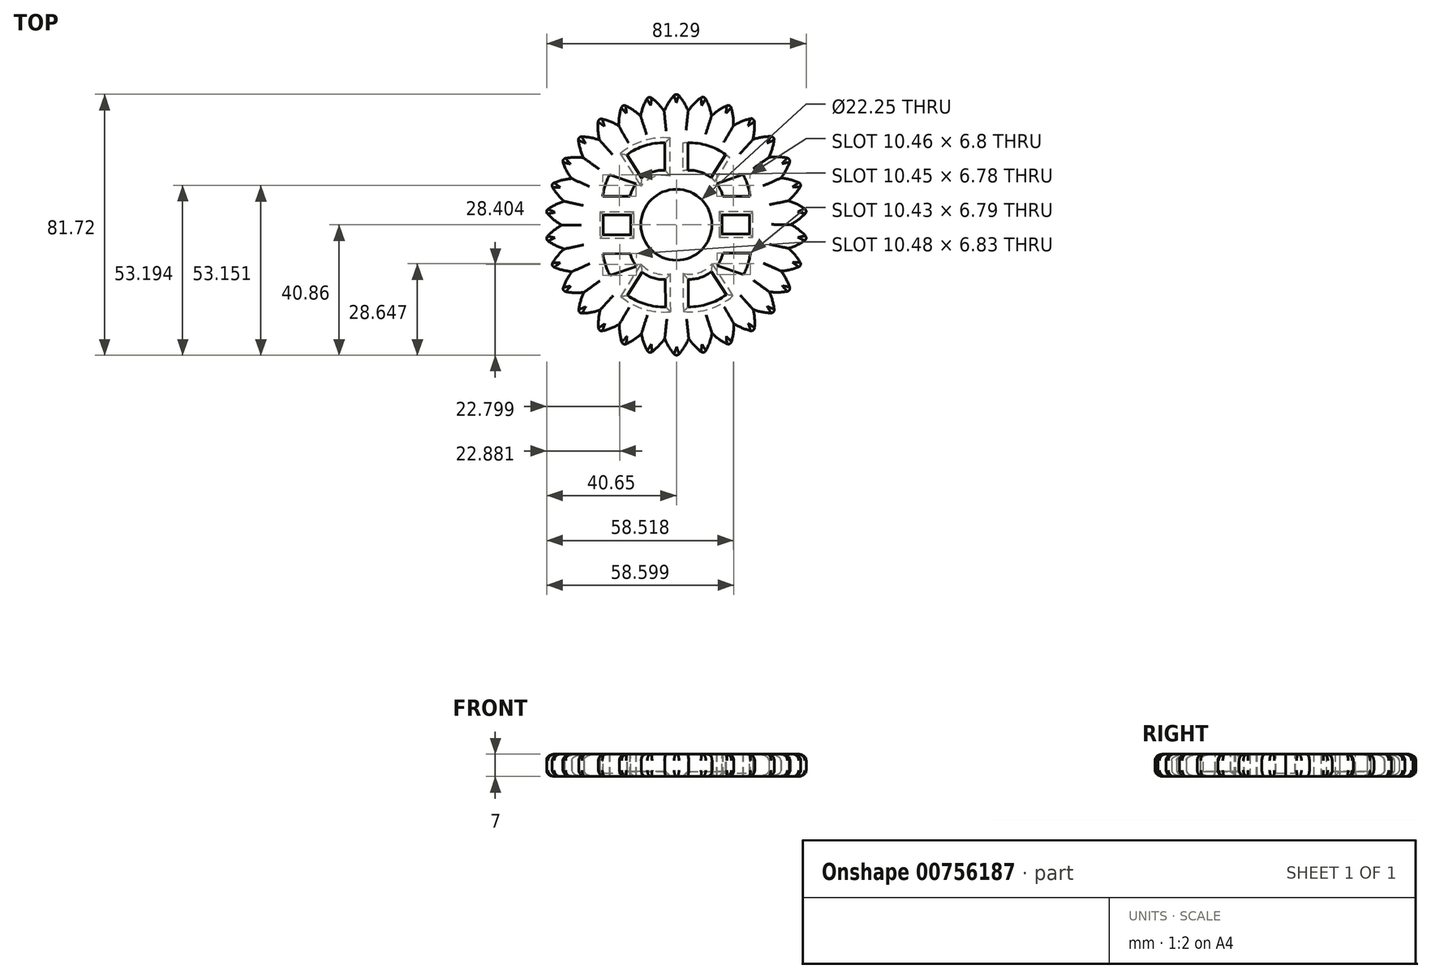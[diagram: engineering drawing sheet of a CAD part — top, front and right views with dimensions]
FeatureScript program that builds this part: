
annotation { "Feature Type Name" : "Feature", "Feature Type Description" : "" }
export const myFeature = defineFeature(function(context is Context, id is Id, definition is map)
    precondition{}
    {
        {
            var Q0;
            Q0=qCreatedBy(makeId("Top.planeOp"),FACE);
            var sketch = newSketch(context, id + "F0", { "sketchPlane" : qUnion([Q0])});
            skCircle(sketch, "E0", {"center": v(0, 0) * mm, "radius": 11.13 * mm});
            skCircle(sketch, "E1", {"center": v(0, 0) * mm, "radius": 28.07 * mm});
            skArc(sketch, "E2", {"start": v(0, 41.34) * mm, "mid": v(-4.06, 35.01) * mm, "end": v(-5.18, 27.59) * mm});
            skArc(sketch, "E3", {"start": v(5.02, 27.62) * mm, "mid": v(3.95, 35) * mm, "end": v(0, 41.34) * mm});
            skArc(sketch, "E4.1.0", {"start": v(8.6, 40.44) * mm, "mid": v(3.31, 35.1) * mm, "end": v(0.67, 28.06) * mm});
            skArc(sketch, "E4.1.1", {"start": v(10.65, 25.97) * mm, "mid": v(11.13, 33.42) * mm, "end": v(8.6, 40.44) * mm});
            skArc(sketch, "E4.2.0", {"start": v(16.8, 37.77) * mm, "mid": v(10.53, 33.64) * mm, "end": v(6.49, 27.3) * mm});
            skArc(sketch, "E4.2.1", {"start": v(15.81, 23.19) * mm, "mid": v(17.84, 30.37) * mm, "end": v(16.8, 37.77) * mm});
            skArc(sketch, "E4.3.0", {"start": v(24.3, 33.45) * mm, "mid": v(17.3, 30.71) * mm, "end": v(12.02, 25.36) * mm});
            skArc(sketch, "E4.3.1", {"start": v(20.29, 19.4) * mm, "mid": v(23.76, 26) * mm, "end": v(24.3, 33.45) * mm});
            skArc(sketch, "E4.4.0", {"start": v(30.71, 27.67) * mm, "mid": v(23.3, 26.45) * mm, "end": v(17.03, 22.31) * mm});
            skArc(sketch, "E4.4.1", {"start": v(23.88, 14.76) * mm, "mid": v(28.65, 20.5) * mm, "end": v(30.71, 27.67) * mm});
            skArc(sketch, "E4.5.0", {"start": v(35.8, 20.68) * mm, "mid": v(28.29, 21.03) * mm, "end": v(21.3, 18.29) * mm});
            skArc(sketch, "E4.5.1", {"start": v(26.42, 9.47) * mm, "mid": v(32.28, 14.1) * mm, "end": v(35.8, 20.68) * mm});
            skArc(sketch, "E4.6.0", {"start": v(39.3, 12.8) * mm, "mid": v(32.04, 14.7) * mm, "end": v(24.63, 13.46) * mm});
            skArc(sketch, "E4.6.1", {"start": v(27.81, 3.77) * mm, "mid": v(34.5, 7.08) * mm, "end": v(39.3, 12.8) * mm});
            skArc(sketch, "E4.7.0", {"start": v(41.1, 4.34) * mm, "mid": v(34.4, 7.71) * mm, "end": v(26.89, 8.05) * mm});
            skArc(sketch, "E4.7.1", {"start": v(27.99, -2.09) * mm, "mid": v(35.22, -0.25) * mm, "end": v(41.1, 4.34) * mm});
            skArc(sketch, "E4.8.0", {"start": v(41.11, -4.3) * mm, "mid": v(35.25, 0.4) * mm, "end": v(27.97, 2.28) * mm});
            skArc(sketch, "E4.8.1", {"start": v(26.94, -7.86) * mm, "mid": v(34.4, -7.56) * mm, "end": v(41.11, -4.3) * mm});
            skArc(sketch, "E4.9.0", {"start": v(39.32, -12.75) * mm, "mid": v(34.56, -6.94) * mm, "end": v(27.84, -3.58) * mm});
            skArc(sketch, "E4.9.1", {"start": v(24.72, -13.29) * mm, "mid": v(32.08, -14.55) * mm, "end": v(39.32, -12.75) * mm});
            skArc(sketch, "E4.10.0", {"start": v(35.82, -20.64) * mm, "mid": v(32.36, -13.97) * mm, "end": v(26.49, -9.29) * mm});
            skArc(sketch, "E4.10.1", {"start": v(21.42, -18.14) * mm, "mid": v(28.36, -20.9) * mm, "end": v(35.82, -20.64) * mm});
            skArc(sketch, "E4.11.0", {"start": v(30.74, -27.64) * mm, "mid": v(28.75, -20.4) * mm, "end": v(23.98, -14.6) * mm});
            skArc(sketch, "E4.11.1", {"start": v(17.18, -22.2) * mm, "mid": v(23.4, -26.33) * mm, "end": v(30.74, -27.64) * mm});
            skArc(sketch, "E4.12.0", {"start": v(24.33, -33.42) * mm, "mid": v(23.89, -25.92) * mm, "end": v(20.42, -19.26) * mm});
            skArc(sketch, "E4.12.1", {"start": v(12.2, -25.28) * mm, "mid": v(17.4, -30.62) * mm, "end": v(24.33, -33.42) * mm});
            skArc(sketch, "E4.13.0", {"start": v(16.85, -37.75) * mm, "mid": v(17.98, -30.32) * mm, "end": v(15.97, -23.08) * mm});
            skArc(sketch, "E4.13.1", {"start": v(6.67, -27.26) * mm, "mid": v(10.67, -33.57) * mm, "end": v(16.85, -37.75) * mm});
            skArc(sketch, "E4.14.0", {"start": v(8.64, -40.43) * mm, "mid": v(11.28, -33.4) * mm, "end": v(10.83, -25.9) * mm});
            skArc(sketch, "E4.14.1", {"start": v(0.86, -28.05) * mm, "mid": v(3.46, -35.05) * mm, "end": v(8.64, -40.43) * mm});
            skArc(sketch, "E4.15.0", {"start": v(0.05, -41.34) * mm, "mid": v(4.1, -35) * mm, "end": v(5.2, -27.58) * mm});
            skArc(sketch, "E4.15.1", {"start": v(-4.99, -27.62) * mm, "mid": v(-3.9, -35) * mm, "end": v(0.05, -41.34) * mm});
            skArc(sketch, "E4.16.0", {"start": v(-8.55, -40.45) * mm, "mid": v(-3.27, -35.1) * mm, "end": v(-0.64, -28.06) * mm});
            skArc(sketch, "E4.16.1", {"start": v(-10.62, -25.98) * mm, "mid": v(-11.1, -33.43) * mm, "end": v(-8.55, -40.45) * mm});
            skArc(sketch, "E4.17.0", {"start": v(-16.77, -37.79) * mm, "mid": v(-10.5, -33.65) * mm, "end": v(-6.45, -27.32) * mm});
            skArc(sketch, "E4.17.1", {"start": v(-15.79, -23.2) * mm, "mid": v(-17.8, -30.4) * mm, "end": v(-16.77, -37.79) * mm});
            skArc(sketch, "E4.18.0", {"start": v(-24.25, -33.48) * mm, "mid": v(-17.26, -30.73) * mm, "end": v(-12, -25.38) * mm});
            skArc(sketch, "E4.18.1", {"start": v(-20.27, -19.42) * mm, "mid": v(-23.73, -26.03) * mm, "end": v(-24.25, -33.48) * mm});
            skArc(sketch, "E4.19.0", {"start": v(-30.68, -27.7) * mm, "mid": v(-23.27, -26.48) * mm, "end": v(-17, -22.33) * mm});
            skArc(sketch, "E4.19.1", {"start": v(-23.86, -14.78) * mm, "mid": v(-28.62, -20.53) * mm, "end": v(-30.68, -27.7) * mm});
            skArc(sketch, "E4.20.0", {"start": v(-35.77, -20.72) * mm, "mid": v(-28.26, -21.06) * mm, "end": v(-21.27, -18.3) * mm});
            skArc(sketch, "E4.20.1", {"start": v(-26.41, -9.5) * mm, "mid": v(-32.26, -14.13) * mm, "end": v(-35.77, -20.72) * mm});
            skArc(sketch, "E4.21.0", {"start": v(-39.3, -12.84) * mm, "mid": v(-32.02, -14.73) * mm, "end": v(-24.61, -13.49) * mm});
            skArc(sketch, "E4.21.1", {"start": v(-27.8, -3.8) * mm, "mid": v(-34.5, -7.12) * mm, "end": v(-39.3, -12.84) * mm});
            skArc(sketch, "E4.22.0", {"start": v(-41.1, -4.39) * mm, "mid": v(-34.39, -7.75) * mm, "end": v(-26.88, -8.08) * mm});
            skArc(sketch, "E4.22.1", {"start": v(-28, 2.06) * mm, "mid": v(-35.22, 0.2) * mm, "end": v(-41.1, -4.39) * mm});
            skArc(sketch, "E4.23.0", {"start": v(-41.12, 4.25) * mm, "mid": v(-35.25, -0.43) * mm, "end": v(-27.97, -2.32) * mm});
            skArc(sketch, "E4.23.1", {"start": v(-26.95, 7.83) * mm, "mid": v(-34.41, 7.52) * mm, "end": v(-41.12, 4.25) * mm});
            skArc(sketch, "E4.24.0", {"start": v(-39.34, 12.7) * mm, "mid": v(-34.57, 6.9) * mm, "end": v(-27.84, 3.55) * mm});
            skArc(sketch, "E4.24.1", {"start": v(-24.74, 13.26) * mm, "mid": v(-32.1, 14.51) * mm, "end": v(-39.34, 12.7) * mm});
            skArc(sketch, "E4.25.0", {"start": v(-35.84, 20.6) * mm, "mid": v(-32.38, 13.93) * mm, "end": v(-26.5, 9.26) * mm});
            skArc(sketch, "E4.25.1", {"start": v(-21.44, 18.11) * mm, "mid": v(-28.38, 20.86) * mm, "end": v(-35.84, 20.6) * mm});
            skArc(sketch, "E4.26.0", {"start": v(-30.77, 27.6) * mm, "mid": v(-28.77, 20.36) * mm, "end": v(-24, 14.56) * mm});
            skArc(sketch, "E4.26.1", {"start": v(-17.2, 22.17) * mm, "mid": v(-23.42, 26.3) * mm, "end": v(-30.77, 27.6) * mm});
            skArc(sketch, "E4.27.0", {"start": v(-24.37, 33.4) * mm, "mid": v(-23.91, 25.9) * mm, "end": v(-20.44, 19.23) * mm});
            skArc(sketch, "E4.27.1", {"start": v(-12.22, 25.27) * mm, "mid": v(-17.44, 30.6) * mm, "end": v(-24.37, 33.4) * mm});
            skArc(sketch, "E4.28.0", {"start": v(-16.9, 37.73) * mm, "mid": v(-18.01, 30.3) * mm, "end": v(-16, 23.06) * mm});
            skArc(sketch, "E4.28.1", {"start": v(-6.7, 27.25) * mm, "mid": v(-10.7, 33.56) * mm, "end": v(-16.9, 37.73) * mm});
            skArc(sketch, "E4.29.0", {"start": v(-8.68, 40.42) * mm, "mid": v(-11.32, 33.38) * mm, "end": v(-10.86, 25.88) * mm});
            skArc(sketch, "E4.29.1", {"start": v(-0.9, 28.05) * mm, "mid": v(-3.5, 35.05) * mm, "end": v(-8.68, 40.42) * mm});
            skLineSegment(sketch, "E4.anchor1", {"start": v(0, 0) * mm, "end": v(-5.18, 27.59) * mm, "construction": true});
            skLineSegment(sketch, "E4.anchor2", {"start": v(0, 0) * mm, "end": v(-10.86, 25.88) * mm, "construction": true});
            skSolve(sketch);
        }
        {
            var Q0;
            Q0 = qSketchRegion(id + "F0", true);
            var Q1;
            Q1=makeQuery(id+"F0.imprint","IMPRINT",FACE,{"disambiguationData":[TD([[makeQuery(id+"F0.imprint","IMPRINT",EDGE,{"derivedFrom":sQuery(id+"F0.wireOp",EDGE,"E0")}),-1.0]])]});
            extrude(context, id + "F1", {"entities" : qUnion([Q0, Q1]), "depth" : 7 * mm, "offsetDistance" : 25 * mm});
        }
        {
            var Q0;
            Q0=makeQuery(id+"F1.opExtrude","CAP_EDGE",EDGE,{"disambiguationData":[OSD([sQuery(id+"F0.wireOp",EDGE,"E4.25.0")])],"isStart":false});
            var Q1;
            Q1=makeQuery(id+"F1.opExtrude","CAP_EDGE",EDGE,{"disambiguationData":[OSD([sQuery(id+"F0.wireOp",EDGE,"E4.25.1")])],"isStart":false});
            var Q2;
            Q2=makeQuery(id+"F1.opExtrude","CAP_EDGE",EDGE,{"disambiguationData":[OSD([sQuery(id+"F0.wireOp",EDGE,"E4.26.0")])],"isStart":false});
            var Q3;
            Q3=makeQuery(id+"F1.opExtrude","CAP_EDGE",EDGE,{"disambiguationData":[OSD([sQuery(id+"F0.wireOp",EDGE,"E4.26.1")])],"isStart":false});
            var Q4;
            Q4=makeQuery(id+"F1.opExtrude","CAP_EDGE",EDGE,{"disambiguationData":[OSD([sQuery(id+"F0.wireOp",EDGE,"E4.27.0")])],"isStart":false});
            var Q5;
            Q5=makeQuery(id+"F1.opExtrude","CAP_EDGE",EDGE,{"disambiguationData":[OSD([sQuery(id+"F0.wireOp",EDGE,"E4.27.1")])],"isStart":false});
            var Q6;
            Q6=makeQuery(id+"F1.opExtrude","CAP_EDGE",EDGE,{"disambiguationData":[OSD([sQuery(id+"F0.wireOp",EDGE,"E4.28.0")])],"isStart":false});
            var Q7;
            Q7=makeQuery(id+"F1.opExtrude","CAP_EDGE",EDGE,{"disambiguationData":[OSD([sQuery(id+"F0.wireOp",EDGE,"E4.28.1")])],"isStart":false});
            var Q8;
            Q8=makeQuery(id+"F1.opExtrude","CAP_EDGE",EDGE,{"disambiguationData":[OSD([sQuery(id+"F0.wireOp",EDGE,"E4.29.0")])],"isStart":false});
            var Q9;
            Q9=makeQuery(id+"F1.opExtrude","CAP_EDGE",EDGE,{"disambiguationData":[OSD([sQuery(id+"F0.wireOp",EDGE,"E4.29.1")])],"isStart":false});
            var Q10;
            Q10=makeQuery(id+"F1.opExtrude","CAP_EDGE",EDGE,{"disambiguationData":[OSD([sQuery(id+"F0.wireOp",EDGE,"E2")])],"isStart":false});
            var Q11;
            Q11=makeQuery(id+"F1.opExtrude","CAP_EDGE",EDGE,{"disambiguationData":[OSD([sQuery(id+"F0.wireOp",EDGE,"E3")])],"isStart":false});
            var Q12;
            Q12=makeQuery(id+"F1.opExtrude","CAP_EDGE",EDGE,{"disambiguationData":[OSD([sQuery(id+"F0.wireOp",EDGE,"E4.1.0")])],"isStart":false});
            var Q13;
            Q13=makeQuery(id+"F1.opExtrude","CAP_EDGE",EDGE,{"disambiguationData":[OSD([sQuery(id+"F0.wireOp",EDGE,"E4.1.1")])],"isStart":false});
            var Q14;
            Q14=makeQuery(id+"F1.opExtrude","CAP_EDGE",EDGE,{"disambiguationData":[OSD([sQuery(id+"F0.wireOp",EDGE,"E4.2.0")])],"isStart":false});
            var Q15;
            Q15=makeQuery(id+"F1.opExtrude","CAP_EDGE",EDGE,{"disambiguationData":[OSD([sQuery(id+"F0.wireOp",EDGE,"E4.2.1")])],"isStart":false});
            var Q16;
            Q16=makeQuery(id+"F1.opExtrude","CAP_EDGE",EDGE,{"disambiguationData":[OSD([sQuery(id+"F0.wireOp",EDGE,"E4.3.0")])],"isStart":false});
            var Q17;
            Q17=makeQuery(id+"F1.opExtrude","CAP_EDGE",EDGE,{"disambiguationData":[OSD([sQuery(id+"F0.wireOp",EDGE,"E4.3.1")])],"isStart":false});
            var Q18;
            Q18=makeQuery(id+"F1.opExtrude","CAP_EDGE",EDGE,{"disambiguationData":[OSD([sQuery(id+"F0.wireOp",EDGE,"E4.4.0")])],"isStart":false});
            var Q19;
            Q19=makeQuery(id+"F1.opExtrude","CAP_EDGE",EDGE,{"disambiguationData":[OSD([sQuery(id+"F0.wireOp",EDGE,"E4.4.1")])],"isStart":false});
            var Q20;
            Q20=makeQuery(id+"F1.opExtrude","CAP_EDGE",EDGE,{"disambiguationData":[OSD([sQuery(id+"F0.wireOp",EDGE,"E4.5.0")])],"isStart":false});
            var Q21;
            Q21=makeQuery(id+"F1.opExtrude","CAP_EDGE",EDGE,{"disambiguationData":[OSD([sQuery(id+"F0.wireOp",EDGE,"E4.5.1")])],"isStart":false});
            var Q22;
            Q22=makeQuery(id+"F1.opExtrude","CAP_EDGE",EDGE,{"disambiguationData":[OSD([sQuery(id+"F0.wireOp",EDGE,"E4.6.0")])],"isStart":false});
            var Q23;
            Q23=makeQuery(id+"F1.opExtrude","CAP_EDGE",EDGE,{"disambiguationData":[OSD([sQuery(id+"F0.wireOp",EDGE,"E4.6.1")])],"isStart":false});
            var Q24;
            Q24=makeQuery(id+"F1.opExtrude","CAP_EDGE",EDGE,{"disambiguationData":[OSD([sQuery(id+"F0.wireOp",EDGE,"E4.7.0")])],"isStart":false});
            var Q25;
            Q25=makeQuery(id+"F1.opExtrude","CAP_EDGE",EDGE,{"disambiguationData":[OSD([sQuery(id+"F0.wireOp",EDGE,"E4.7.1")])],"isStart":false});
            var Q26;
            Q26=makeQuery(id+"F1.opExtrude","CAP_EDGE",EDGE,{"disambiguationData":[OSD([sQuery(id+"F0.wireOp",EDGE,"E4.8.0")])],"isStart":false});
            var Q27;
            Q27=makeQuery(id+"F1.opExtrude","CAP_EDGE",EDGE,{"disambiguationData":[OSD([sQuery(id+"F0.wireOp",EDGE,"E4.8.1")])],"isStart":false});
            var Q28;
            Q28=makeQuery(id+"F1.opExtrude","CAP_EDGE",EDGE,{"disambiguationData":[OSD([sQuery(id+"F0.wireOp",EDGE,"E4.9.0")])],"isStart":false});
            var Q29;
            Q29=makeQuery(id+"F1.opExtrude","CAP_EDGE",EDGE,{"disambiguationData":[OSD([sQuery(id+"F0.wireOp",EDGE,"E4.9.1")])],"isStart":false});
            var Q30;
            Q30=makeQuery(id+"F1.opExtrude","CAP_EDGE",EDGE,{"disambiguationData":[OSD([sQuery(id+"F0.wireOp",EDGE,"E4.10.0")])],"isStart":false});
            var Q31;
            Q31=makeQuery(id+"F1.opExtrude","CAP_EDGE",EDGE,{"disambiguationData":[OSD([sQuery(id+"F0.wireOp",EDGE,"E4.10.1")])],"isStart":false});
            var Q32;
            Q32=makeQuery(id+"F1.opExtrude","CAP_EDGE",EDGE,{"disambiguationData":[OSD([sQuery(id+"F0.wireOp",EDGE,"E4.11.0")])],"isStart":false});
            var Q33;
            Q33=makeQuery(id+"F1.opExtrude","CAP_EDGE",EDGE,{"disambiguationData":[OSD([sQuery(id+"F0.wireOp",EDGE,"E4.11.1")])],"isStart":false});
            var Q34;
            Q34=makeQuery(id+"F1.opExtrude","CAP_EDGE",EDGE,{"disambiguationData":[OSD([sQuery(id+"F0.wireOp",EDGE,"E4.12.0")])],"isStart":false});
            var Q35;
            Q35=makeQuery(id+"F1.opExtrude","CAP_EDGE",EDGE,{"disambiguationData":[OSD([sQuery(id+"F0.wireOp",EDGE,"E4.12.1")])],"isStart":false});
            var Q36;
            Q36=makeQuery(id+"F1.opExtrude","CAP_EDGE",EDGE,{"disambiguationData":[OSD([sQuery(id+"F0.wireOp",EDGE,"E4.13.0")])],"isStart":false});
            var Q37;
            Q37=makeQuery(id+"F1.opExtrude","CAP_EDGE",EDGE,{"disambiguationData":[OSD([sQuery(id+"F0.wireOp",EDGE,"E4.13.1")])],"isStart":false});
            var Q38;
            Q38=makeQuery(id+"F1.opExtrude","CAP_EDGE",EDGE,{"disambiguationData":[OSD([sQuery(id+"F0.wireOp",EDGE,"E4.14.0")])],"isStart":false});
            var Q39;
            Q39=makeQuery(id+"F1.opExtrude","CAP_EDGE",EDGE,{"disambiguationData":[OSD([sQuery(id+"F0.wireOp",EDGE,"E4.14.1")])],"isStart":false});
            var Q40;
            Q40=makeQuery(id+"F1.opExtrude","CAP_EDGE",EDGE,{"disambiguationData":[OSD([sQuery(id+"F0.wireOp",EDGE,"E4.15.0")])],"isStart":false});
            var Q41;
            Q41=makeQuery(id+"F1.opExtrude","CAP_EDGE",EDGE,{"disambiguationData":[OSD([sQuery(id+"F0.wireOp",EDGE,"E4.15.1")])],"isStart":false});
            var Q42;
            Q42=makeQuery(id+"F1.opExtrude","CAP_EDGE",EDGE,{"disambiguationData":[OSD([sQuery(id+"F0.wireOp",EDGE,"E4.16.1")])],"isStart":false});
            var Q43;
            Q43=makeQuery(id+"F1.opExtrude","CAP_EDGE",EDGE,{"disambiguationData":[OSD([sQuery(id+"F0.wireOp",EDGE,"E4.17.0")])],"isStart":false});
            var Q44;
            Q44=makeQuery(id+"F1.opExtrude","CAP_EDGE",EDGE,{"disambiguationData":[OSD([sQuery(id+"F0.wireOp",EDGE,"E4.17.1")])],"isStart":false});
            var Q45;
            Q45=makeQuery(id+"F1.opExtrude","CAP_EDGE",EDGE,{"disambiguationData":[OSD([sQuery(id+"F0.wireOp",EDGE,"E4.18.0")])],"isStart":false});
            var Q46;
            Q46=makeQuery(id+"F1.opExtrude","CAP_EDGE",EDGE,{"disambiguationData":[OSD([sQuery(id+"F0.wireOp",EDGE,"E4.18.1")])],"isStart":false});
            var Q47;
            Q47=makeQuery(id+"F1.opExtrude","CAP_EDGE",EDGE,{"disambiguationData":[OSD([sQuery(id+"F0.wireOp",EDGE,"E4.19.0")])],"isStart":false});
            var Q48;
            Q48=makeQuery(id+"F1.opExtrude","CAP_EDGE",EDGE,{"disambiguationData":[OSD([sQuery(id+"F0.wireOp",EDGE,"E4.19.1")])],"isStart":false});
            var Q49;
            Q49=makeQuery(id+"F1.opExtrude","CAP_EDGE",EDGE,{"disambiguationData":[OSD([sQuery(id+"F0.wireOp",EDGE,"E4.20.0")])],"isStart":false});
            var Q50;
            Q50=makeQuery(id+"F1.opExtrude","CAP_EDGE",EDGE,{"disambiguationData":[OSD([sQuery(id+"F0.wireOp",EDGE,"E4.20.1")])],"isStart":false});
            var Q51;
            Q51=makeQuery(id+"F1.opExtrude","CAP_EDGE",EDGE,{"disambiguationData":[OSD([sQuery(id+"F0.wireOp",EDGE,"E4.21.0")])],"isStart":false});
            var Q52;
            Q52=makeQuery(id+"F1.opExtrude","CAP_EDGE",EDGE,{"disambiguationData":[OSD([sQuery(id+"F0.wireOp",EDGE,"E4.22.0")])],"isStart":false});
            var Q53;
            Q53=makeQuery(id+"F1.opExtrude","CAP_EDGE",EDGE,{"disambiguationData":[OSD([sQuery(id+"F0.wireOp",EDGE,"E4.22.1")])],"isStart":false});
            var Q54;
            Q54=makeQuery(id+"F1.opExtrude","CAP_EDGE",EDGE,{"disambiguationData":[OSD([sQuery(id+"F0.wireOp",EDGE,"E4.23.0")])],"isStart":false});
            var Q55;
            Q55=makeQuery(id+"F1.opExtrude","CAP_EDGE",EDGE,{"disambiguationData":[OSD([sQuery(id+"F0.wireOp",EDGE,"E4.23.1")])],"isStart":false});
            var Q56;
            Q56=makeQuery(id+"F1.opExtrude","CAP_EDGE",EDGE,{"disambiguationData":[OSD([sQuery(id+"F0.wireOp",EDGE,"E4.24.1")])],"isStart":false});
            var Q57;
            Q57=makeQuery(id+"F1.opExtrude","CAP_EDGE",EDGE,{"disambiguationData":[OSD([sQuery(id+"F0.wireOp",EDGE,"E4.24.0")])],"isStart":false});
            var Q58;
            Q58=makeQuery(id+"F1.opExtrude","CAP_EDGE",EDGE,{"disambiguationData":[OSD([sQuery(id+"F0.wireOp",EDGE,"E4.21.1")])],"isStart":false});
            var Q59;
            Q59=makeQuery(id+"F1.opExtrude","CAP_EDGE",EDGE,{"disambiguationData":[OSD([sQuery(id+"F0.wireOp",EDGE,"E4.16.0")])],"isStart":false});
            fillet(context, id + "F2", {"entities" : qUnion([Q0, Q1, Q2, Q3, Q4, Q5, Q6, Q7, Q8, Q9, Q10, Q11, Q12, Q13, Q14, Q15, Q16, Q17, Q18, Q19, Q20, Q21, Q22, Q23, Q24, Q25, Q26, Q27, Q28, Q29, Q30, Q31, Q32, Q33, Q34, Q35, Q36, Q37, Q38, Q39, Q40, Q41, Q42, Q43, Q44, Q45, Q46, Q47, Q48, Q49, Q50, Q51, Q52, Q53, Q54, Q55, Q56, Q57, Q58, Q59]), "radius" : 2 * mm, "tangentPropagation" : true, "allowEdgeOverflow" : false});
        }
        {
            var Q0;
            Q0=makeQuery(id+"F1.opExtrude","CAP_EDGE",EDGE,{"disambiguationData":[OSD([sQuery(id+"F0.wireOp",EDGE,"E4.17.0")])],"isStart":true});
            var Q1;
            Q1=makeQuery(id+"F1.opExtrude","CAP_EDGE",EDGE,{"disambiguationData":[OSD([sQuery(id+"F0.wireOp",EDGE,"E4.16.1")])],"isStart":true});
            var Q2;
            Q2=makeQuery(id+"F1.opExtrude","CAP_EDGE",EDGE,{"disambiguationData":[OSD([sQuery(id+"F0.wireOp",EDGE,"E4.16.0")])],"isStart":true});
            var Q3;
            Q3=makeQuery(id+"F1.opExtrude","CAP_EDGE",EDGE,{"disambiguationData":[OSD([sQuery(id+"F0.wireOp",EDGE,"E4.15.1")])],"isStart":true});
            var Q4;
            Q4=makeQuery(id+"F1.opExtrude","CAP_EDGE",EDGE,{"disambiguationData":[OSD([sQuery(id+"F0.wireOp",EDGE,"E4.15.0")])],"isStart":true});
            var Q5;
            Q5=makeQuery(id+"F1.opExtrude","CAP_EDGE",EDGE,{"disambiguationData":[OSD([sQuery(id+"F0.wireOp",EDGE,"E4.14.1")])],"isStart":true});
            var Q6;
            Q6=makeQuery(id+"F1.opExtrude","CAP_EDGE",EDGE,{"disambiguationData":[OSD([sQuery(id+"F0.wireOp",EDGE,"E4.14.0")])],"isStart":true});
            var Q7;
            Q7=makeQuery(id+"F1.opExtrude","CAP_EDGE",EDGE,{"disambiguationData":[OSD([sQuery(id+"F0.wireOp",EDGE,"E4.13.1")])],"isStart":true});
            var Q8;
            Q8=makeQuery(id+"F1.opExtrude","CAP_EDGE",EDGE,{"disambiguationData":[OSD([sQuery(id+"F0.wireOp",EDGE,"E4.13.0")])],"isStart":true});
            var Q9;
            Q9=makeQuery(id+"F1.opExtrude","CAP_EDGE",EDGE,{"disambiguationData":[OSD([sQuery(id+"F0.wireOp",EDGE,"E4.12.1")])],"isStart":true});
            var Q10;
            Q10=makeQuery(id+"F1.opExtrude","CAP_EDGE",EDGE,{"disambiguationData":[OSD([sQuery(id+"F0.wireOp",EDGE,"E4.12.0")])],"isStart":true});
            var Q11;
            Q11=makeQuery(id+"F1.opExtrude","CAP_EDGE",EDGE,{"disambiguationData":[OSD([sQuery(id+"F0.wireOp",EDGE,"E4.11.1")])],"isStart":true});
            var Q12;
            Q12=makeQuery(id+"F1.opExtrude","CAP_EDGE",EDGE,{"disambiguationData":[OSD([sQuery(id+"F0.wireOp",EDGE,"E4.11.0")])],"isStart":true});
            var Q13;
            Q13=makeQuery(id+"F1.opExtrude","CAP_EDGE",EDGE,{"disambiguationData":[OSD([sQuery(id+"F0.wireOp",EDGE,"E4.10.1")])],"isStart":true});
            var Q14;
            Q14=makeQuery(id+"F1.opExtrude","CAP_EDGE",EDGE,{"disambiguationData":[OSD([sQuery(id+"F0.wireOp",EDGE,"E4.10.0")])],"isStart":true});
            var Q15;
            Q15=makeQuery(id+"F1.opExtrude","CAP_EDGE",EDGE,{"disambiguationData":[OSD([sQuery(id+"F0.wireOp",EDGE,"E4.9.1")])],"isStart":true});
            var Q16;
            Q16=makeQuery(id+"F1.opExtrude","CAP_EDGE",EDGE,{"disambiguationData":[OSD([sQuery(id+"F0.wireOp",EDGE,"E4.9.0")])],"isStart":true});
            var Q17;
            Q17=makeQuery(id+"F1.opExtrude","CAP_EDGE",EDGE,{"disambiguationData":[OSD([sQuery(id+"F0.wireOp",EDGE,"E4.8.1")])],"isStart":true});
            var Q18;
            Q18=makeQuery(id+"F1.opExtrude","CAP_EDGE",EDGE,{"disambiguationData":[OSD([sQuery(id+"F0.wireOp",EDGE,"E4.8.0")])],"isStart":true});
            var Q19;
            Q19=makeQuery(id+"F1.opExtrude","CAP_EDGE",EDGE,{"disambiguationData":[OSD([sQuery(id+"F0.wireOp",EDGE,"E4.7.1")])],"isStart":true});
            var Q20;
            Q20=makeQuery(id+"F1.opExtrude","CAP_EDGE",EDGE,{"disambiguationData":[OSD([sQuery(id+"F0.wireOp",EDGE,"E4.7.0")])],"isStart":true});
            var Q21;
            Q21=makeQuery(id+"F1.opExtrude","CAP_EDGE",EDGE,{"disambiguationData":[OSD([sQuery(id+"F0.wireOp",EDGE,"E4.6.1")])],"isStart":true});
            var Q22;
            Q22=makeQuery(id+"F1.opExtrude","CAP_EDGE",EDGE,{"disambiguationData":[OSD([sQuery(id+"F0.wireOp",EDGE,"E4.6.0")])],"isStart":true});
            var Q23;
            Q23=makeQuery(id+"F1.opExtrude","CAP_EDGE",EDGE,{"disambiguationData":[OSD([sQuery(id+"F0.wireOp",EDGE,"E4.5.1")])],"isStart":true});
            var Q24;
            Q24=makeQuery(id+"F1.opExtrude","CAP_EDGE",EDGE,{"disambiguationData":[OSD([sQuery(id+"F0.wireOp",EDGE,"E4.5.0")])],"isStart":true});
            var Q25;
            Q25=makeQuery(id+"F1.opExtrude","CAP_EDGE",EDGE,{"disambiguationData":[OSD([sQuery(id+"F0.wireOp",EDGE,"E4.4.1")])],"isStart":true});
            var Q26;
            Q26=makeQuery(id+"F1.opExtrude","CAP_EDGE",EDGE,{"disambiguationData":[OSD([sQuery(id+"F0.wireOp",EDGE,"E4.4.0")])],"isStart":true});
            var Q27;
            Q27=makeQuery(id+"F1.opExtrude","CAP_EDGE",EDGE,{"disambiguationData":[OSD([sQuery(id+"F0.wireOp",EDGE,"E4.3.1")])],"isStart":true});
            var Q28;
            Q28=makeQuery(id+"F1.opExtrude","CAP_EDGE",EDGE,{"disambiguationData":[OSD([sQuery(id+"F0.wireOp",EDGE,"E4.3.0")])],"isStart":true});
            var Q29;
            Q29=makeQuery(id+"F1.opExtrude","CAP_EDGE",EDGE,{"disambiguationData":[OSD([sQuery(id+"F0.wireOp",EDGE,"E4.2.1")])],"isStart":true});
            var Q30;
            Q30=makeQuery(id+"F1.opExtrude","CAP_EDGE",EDGE,{"disambiguationData":[OSD([sQuery(id+"F0.wireOp",EDGE,"E4.2.0")])],"isStart":true});
            var Q31;
            Q31=makeQuery(id+"F1.opExtrude","CAP_EDGE",EDGE,{"disambiguationData":[OSD([sQuery(id+"F0.wireOp",EDGE,"E4.1.1")])],"isStart":true});
            var Q32;
            Q32=makeQuery(id+"F1.opExtrude","CAP_EDGE",EDGE,{"disambiguationData":[OSD([sQuery(id+"F0.wireOp",EDGE,"E4.1.0")])],"isStart":true});
            var Q33;
            Q33=makeQuery(id+"F1.opExtrude","CAP_EDGE",EDGE,{"disambiguationData":[OSD([sQuery(id+"F0.wireOp",EDGE,"E3")])],"isStart":true});
            var Q34;
            Q34=makeQuery(id+"F1.opExtrude","CAP_EDGE",EDGE,{"disambiguationData":[OSD([sQuery(id+"F0.wireOp",EDGE,"E2")])],"isStart":true});
            var Q35;
            Q35=makeQuery(id+"F1.opExtrude","CAP_EDGE",EDGE,{"disambiguationData":[OSD([sQuery(id+"F0.wireOp",EDGE,"E4.29.1")])],"isStart":true});
            var Q36;
            Q36=makeQuery(id+"F1.opExtrude","CAP_EDGE",EDGE,{"disambiguationData":[OSD([sQuery(id+"F0.wireOp",EDGE,"E4.29.0")])],"isStart":true});
            var Q37;
            Q37=makeQuery(id+"F1.opExtrude","CAP_EDGE",EDGE,{"disambiguationData":[OSD([sQuery(id+"F0.wireOp",EDGE,"E4.28.1")])],"isStart":true});
            var Q38;
            Q38=makeQuery(id+"F1.opExtrude","CAP_EDGE",EDGE,{"disambiguationData":[OSD([sQuery(id+"F0.wireOp",EDGE,"E4.28.0")])],"isStart":true});
            var Q39;
            Q39=makeQuery(id+"F1.opExtrude","CAP_EDGE",EDGE,{"disambiguationData":[OSD([sQuery(id+"F0.wireOp",EDGE,"E4.27.1")])],"isStart":true});
            var Q40;
            Q40=makeQuery(id+"F1.opExtrude","CAP_EDGE",EDGE,{"disambiguationData":[OSD([sQuery(id+"F0.wireOp",EDGE,"E4.27.0")])],"isStart":true});
            var Q41;
            Q41=makeQuery(id+"F1.opExtrude","CAP_EDGE",EDGE,{"disambiguationData":[OSD([sQuery(id+"F0.wireOp",EDGE,"E4.26.1")])],"isStart":true});
            var Q42;
            Q42=makeQuery(id+"F1.opExtrude","CAP_EDGE",EDGE,{"disambiguationData":[OSD([sQuery(id+"F0.wireOp",EDGE,"E4.26.0")])],"isStart":true});
            var Q43;
            Q43=makeQuery(id+"F1.opExtrude","CAP_EDGE",EDGE,{"disambiguationData":[OSD([sQuery(id+"F0.wireOp",EDGE,"E4.25.1")])],"isStart":true});
            var Q44;
            Q44=makeQuery(id+"F1.opExtrude","CAP_EDGE",EDGE,{"disambiguationData":[OSD([sQuery(id+"F0.wireOp",EDGE,"E4.25.0")])],"isStart":true});
            var Q45;
            Q45=makeQuery(id+"F1.opExtrude","CAP_EDGE",EDGE,{"disambiguationData":[OSD([sQuery(id+"F0.wireOp",EDGE,"E4.24.1")])],"isStart":true});
            var Q46;
            Q46=makeQuery(id+"F1.opExtrude","CAP_EDGE",EDGE,{"disambiguationData":[OSD([sQuery(id+"F0.wireOp",EDGE,"E4.24.0")])],"isStart":true});
            var Q47;
            Q47=makeQuery(id+"F1.opExtrude","CAP_EDGE",EDGE,{"disambiguationData":[OSD([sQuery(id+"F0.wireOp",EDGE,"E4.23.1")])],"isStart":true});
            var Q48;
            Q48=makeQuery(id+"F1.opExtrude","CAP_EDGE",EDGE,{"disambiguationData":[OSD([sQuery(id+"F0.wireOp",EDGE,"E4.23.0")])],"isStart":true});
            var Q49;
            Q49=makeQuery(id+"F1.opExtrude","CAP_EDGE",EDGE,{"disambiguationData":[OSD([sQuery(id+"F0.wireOp",EDGE,"E4.22.1")])],"isStart":true});
            var Q50;
            Q50=makeQuery(id+"F1.opExtrude","CAP_EDGE",EDGE,{"disambiguationData":[OSD([sQuery(id+"F0.wireOp",EDGE,"E4.22.0")])],"isStart":true});
            var Q51;
            Q51=makeQuery(id+"F1.opExtrude","CAP_EDGE",EDGE,{"disambiguationData":[OSD([sQuery(id+"F0.wireOp",EDGE,"E4.21.1")])],"isStart":true});
            var Q52;
            Q52=makeQuery(id+"F1.opExtrude","CAP_EDGE",EDGE,{"disambiguationData":[OSD([sQuery(id+"F0.wireOp",EDGE,"E4.21.0")])],"isStart":true});
            var Q53;
            Q53=makeQuery(id+"F1.opExtrude","CAP_EDGE",EDGE,{"disambiguationData":[OSD([sQuery(id+"F0.wireOp",EDGE,"E4.20.1")])],"isStart":true});
            var Q54;
            Q54=makeQuery(id+"F1.opExtrude","CAP_EDGE",EDGE,{"disambiguationData":[OSD([sQuery(id+"F0.wireOp",EDGE,"E4.20.0")])],"isStart":true});
            var Q55;
            Q55=makeQuery(id+"F1.opExtrude","CAP_EDGE",EDGE,{"disambiguationData":[OSD([sQuery(id+"F0.wireOp",EDGE,"E4.19.1")])],"isStart":true});
            var Q56;
            Q56=makeQuery(id+"F1.opExtrude","CAP_EDGE",EDGE,{"disambiguationData":[OSD([sQuery(id+"F0.wireOp",EDGE,"E4.19.0")])],"isStart":true});
            var Q57;
            Q57=makeQuery(id+"F1.opExtrude","CAP_EDGE",EDGE,{"disambiguationData":[OSD([sQuery(id+"F0.wireOp",EDGE,"E4.18.1")])],"isStart":true});
            var Q58;
            Q58=makeQuery(id+"F1.opExtrude","CAP_EDGE",EDGE,{"disambiguationData":[OSD([sQuery(id+"F0.wireOp",EDGE,"E4.18.0")])],"isStart":true});
            var Q59;
            Q59=makeQuery(id+"F1.opExtrude","CAP_EDGE",EDGE,{"disambiguationData":[OSD([sQuery(id+"F0.wireOp",EDGE,"E4.17.1")])],"isStart":true});
            fillet(context, id + "F3", {"entities" : qUnion([Q0, Q1, Q2, Q3, Q4, Q5, Q6, Q7, Q8, Q9, Q10, Q11, Q12, Q13, Q14, Q15, Q16, Q17, Q18, Q19, Q20, Q21, Q22, Q23, Q24, Q25, Q26, Q27, Q28, Q29, Q30, Q31, Q32, Q33, Q34, Q35, Q36, Q37, Q38, Q39, Q40, Q41, Q42, Q43, Q44, Q45, Q46, Q47, Q48, Q49, Q50, Q51, Q52, Q53, Q54, Q55, Q56, Q57, Q58, Q59]), "radius" : 2 * mm, "tangentPropagation" : true, "allowEdgeOverflow" : false});
        }
        {
            var Q0;
            Q0=makeQuery(id+"F1.opExtrude","CAP_FACE",FACE,{"disambiguationData":[OSD([sQuery(id+"F0.wireOp",EDGE,"E0"),sQuery(id+"F0.wireOp",EDGE,"E2"),sQuery(id+"F0.wireOp",EDGE,"E3"),sQuery(id+"F0.wireOp",EDGE,"E4.1.0"),sQuery(id+"F0.wireOp",EDGE,"E4.1.1"),sQuery(id+"F0.wireOp",EDGE,"E4.2.0"),sQuery(id+"F0.wireOp",EDGE,"E4.2.1"),sQuery(id+"F0.wireOp",EDGE,"E4.3.0"),sQuery(id+"F0.wireOp",EDGE,"E4.3.1"),sQuery(id+"F0.wireOp",EDGE,"E4.4.0"),sQuery(id+"F0.wireOp",EDGE,"E4.4.1"),sQuery(id+"F0.wireOp",EDGE,"E4.5.0"),sQuery(id+"F0.wireOp",EDGE,"E4.5.1"),sQuery(id+"F0.wireOp",EDGE,"E4.6.0"),sQuery(id+"F0.wireOp",EDGE,"E4.6.1"),sQuery(id+"F0.wireOp",EDGE,"E4.7.0"),sQuery(id+"F0.wireOp",EDGE,"E4.7.1"),sQuery(id+"F0.wireOp",EDGE,"E4.8.0"),sQuery(id+"F0.wireOp",EDGE,"E4.8.1"),sQuery(id+"F0.wireOp",EDGE,"E4.9.0"),sQuery(id+"F0.wireOp",EDGE,"E4.9.1"),sQuery(id+"F0.wireOp",EDGE,"E4.10.0"),sQuery(id+"F0.wireOp",EDGE,"E4.10.1"),sQuery(id+"F0.wireOp",EDGE,"E4.11.0"),sQuery(id+"F0.wireOp",EDGE,"E4.11.1"),sQuery(id+"F0.wireOp",EDGE,"E4.12.0"),sQuery(id+"F0.wireOp",EDGE,"E4.12.1"),sQuery(id+"F0.wireOp",EDGE,"E4.13.0"),sQuery(id+"F0.wireOp",EDGE,"E4.13.1"),sQuery(id+"F0.wireOp",EDGE,"E4.14.0"),sQuery(id+"F0.wireOp",EDGE,"E4.14.1"),sQuery(id+"F0.wireOp",EDGE,"E4.15.0"),sQuery(id+"F0.wireOp",EDGE,"E4.15.1"),sQuery(id+"F0.wireOp",EDGE,"E4.16.0"),sQuery(id+"F0.wireOp",EDGE,"E4.16.1"),sQuery(id+"F0.wireOp",EDGE,"E4.17.0"),sQuery(id+"F0.wireOp",EDGE,"E4.17.1"),sQuery(id+"F0.wireOp",EDGE,"E4.18.0"),sQuery(id+"F0.wireOp",EDGE,"E4.18.1"),sQuery(id+"F0.wireOp",EDGE,"E4.19.0"),sQuery(id+"F0.wireOp",EDGE,"E4.19.1"),sQuery(id+"F0.wireOp",EDGE,"E4.20.0"),sQuery(id+"F0.wireOp",EDGE,"E4.20.1"),sQuery(id+"F0.wireOp",EDGE,"E4.21.0"),sQuery(id+"F0.wireOp",EDGE,"E4.21.1"),sQuery(id+"F0.wireOp",EDGE,"E4.22.0"),sQuery(id+"F0.wireOp",EDGE,"E4.22.1"),sQuery(id+"F0.wireOp",EDGE,"E4.23.0"),sQuery(id+"F0.wireOp",EDGE,"E4.23.1"),sQuery(id+"F0.wireOp",EDGE,"E4.24.0"),sQuery(id+"F0.wireOp",EDGE,"E4.24.1"),sQuery(id+"F0.wireOp",EDGE,"E4.25.0"),sQuery(id+"F0.wireOp",EDGE,"E4.25.1"),sQuery(id+"F0.wireOp",EDGE,"E4.26.0"),sQuery(id+"F0.wireOp",EDGE,"E4.26.1"),sQuery(id+"F0.wireOp",EDGE,"E4.27.0"),sQuery(id+"F0.wireOp",EDGE,"E4.27.1"),sQuery(id+"F0.wireOp",EDGE,"E4.28.0"),sQuery(id+"F0.wireOp",EDGE,"E4.28.1"),sQuery(id+"F0.wireOp",EDGE,"E4.29.0"),sQuery(id+"F0.wireOp",EDGE,"E4.29.1")])],"isStart":false});
            var sketch = newSketch(context, id + "F4", { "sketchPlane" : qUnion([Q0])});
            skLineSegment(sketch, "E5", {"start": v(-3.57, 25.67) * mm, "end": v(-3.57, 17.07) * mm});
            skLineSegment(sketch, "E6", {"start": v(-0.02, 38.25) * mm, "end": v(0.07, -38.25) * mm, "construction": true});
            skLineSegment(sketch, "E7.MirrorCS", {"start": v(3.55, 25.68) * mm, "end": v(3.57, 17.08) * mm});
            skLineSegment(sketch, "E8", {"start": v(-14.3, 3.02) * mm, "end": v(-22.9, 3.02) * mm});
            skLineSegment(sketch, "E9.MirrorCS", {"start": v(14.33, 3.05) * mm, "end": v(22.93, 3.08) * mm});
            skLineSegment(sketch, "E10", {"start": v(-29.75, -0.13) * mm, "end": v(29.75, 0.1) * mm, "construction": true});
            skLineSegment(sketch, "E11.MirrorCS", {"start": v(14.36, -2.98) * mm, "end": v(22.96, -2.94) * mm});
            skLineSegment(sketch, "E12.MirrorCS", {"start": v(3.74, -25.69) * mm, "end": v(3.7, -17.09) * mm});
            skLineSegment(sketch, "E13.MirrorCS", {"start": v(-14.27, -3.16) * mm, "end": v(-22.87, -3.22) * mm});
            skLineSegment(sketch, "E14.MirrorCS", {"start": v(-3.38, -25.73) * mm, "end": v(-3.44, -17.13) * mm});
            skArc(sketch, "E15", {"start": v(-3.57, 25.67) * mm, "mid": v(-18.65, 18.96) * mm, "end": v(-22.9, 3.02) * mm});
            skArc(sketch, "E16", {"start": v(-3.57, 17.07) * mm, "mid": v(-12.62, 12.86) * mm, "end": v(-14.3, 3.02) * mm});
            skArc(sketch, "E17.MirrorCS", {"start": v(3.57, 17.08) * mm, "mid": v(12.64, 12.9) * mm, "end": v(14.33, 3.05) * mm});
            skArc(sketch, "E18.MirrorCS", {"start": v(3.55, 25.68) * mm, "mid": v(18.64, 19) * mm, "end": v(22.93, 3.08) * mm});
            skArc(sketch, "E19.MirrorCS", {"start": v(3.74, -25.69) * mm, "mid": v(18.78, -18.9) * mm, "end": v(22.96, -2.94) * mm});
            skArc(sketch, "E20.MirrorCS", {"start": v(3.7, -17.09) * mm, "mid": v(12.73, -12.83) * mm, "end": v(14.36, -2.98) * mm});
            skArc(sketch, "E21.MirrorCS", {"start": v(-3.44, -17.13) * mm, "mid": v(-12.53, -13) * mm, "end": v(-14.27, -3.16) * mm});
            skArc(sketch, "E22.MirrorCS", {"start": v(-3.38, -25.73) * mm, "mid": v(-18.5, -19.14) * mm, "end": v(-22.87, -3.22) * mm});
            skLineSegment(sketch, "E23", {"start": v(-23.08, 8.9) * mm, "end": v(-14.52, 8.9) * mm});
            skLineSegment(sketch, "E24", {"start": v(-20.9, 15.68) * mm, "end": v(-12.62, 12.86) * mm});
            skLineSegment(sketch, "E25", {"start": v(-15.47, 21.93) * mm, "end": v(-10.87, 14.68) * mm});
            skLineSegment(sketch, "E26", {"start": v(-9.35, 24.94) * mm, "end": v(-6.47, 16.82) * mm});
            skLineSegment(sketch, "E27.MirrorCS", {"start": v(23.1, 8.96) * mm, "end": v(14.54, 8.94) * mm});
            skLineSegment(sketch, "E28.MirrorCS", {"start": v(20.9, 15.73) * mm, "end": v(12.64, 12.9) * mm});
            skLineSegment(sketch, "E29.MirrorCS", {"start": v(15.46, 21.96) * mm, "end": v(10.87, 14.7) * mm});
            skLineSegment(sketch, "E30.MirrorCS", {"start": v(9.33, 24.97) * mm, "end": v(6.47, 16.83) * mm});
            skLineSegment(sketch, "E31.MirrorCS", {"start": v(-9.17, -25.05) * mm, "end": v(-6.35, -16.9) * mm});
            skLineSegment(sketch, "E32.MirrorCS", {"start": v(-15.3, -22.07) * mm, "end": v(-10.76, -14.8) * mm});
            skLineSegment(sketch, "E33.MirrorCS", {"start": v(-20.78, -15.87) * mm, "end": v(-12.53, -13) * mm});
            skLineSegment(sketch, "E34.MirrorCS", {"start": v(-23.01, -9.1) * mm, "end": v(-14.45, -9.04) * mm});
            skLineSegment(sketch, "E35.MirrorCS", {"start": v(23.17, -8.82) * mm, "end": v(14.6, -8.86) * mm});
            skLineSegment(sketch, "E36.MirrorCS", {"start": v(21.02, -15.6) * mm, "end": v(12.73, -12.83) * mm});
            skLineSegment(sketch, "E37.MirrorCS", {"start": v(15.63, -21.88) * mm, "end": v(10.98, -14.65) * mm});
            skLineSegment(sketch, "E38.MirrorCS", {"start": v(9.52, -24.93) * mm, "end": v(6.6, -16.82) * mm});
            skLineSegment(sketch, "E39.bottom", {"start": v(-22.9, 3.02) * mm, "end": v(-14.27, 3.02) * mm});
            skLineSegment(sketch, "E39.top", {"start": v(-22.9, -3.16) * mm, "end": v(-14.27, -3.16) * mm});
            skLineSegment(sketch, "E39.left", {"start": v(-22.9, 3.02) * mm, "end": v(-22.9, -3.16) * mm});
            skLineSegment(sketch, "E39.right", {"start": v(-14.27, 3.02) * mm, "end": v(-14.27, -3.16) * mm});
            skLineSegment(sketch, "E40.bottom", {"start": v(14.33, 3.05) * mm, "end": v(22.96, 3.05) * mm});
            skLineSegment(sketch, "E40.top", {"start": v(14.33, -2.94) * mm, "end": v(22.96, -2.94) * mm});
            skLineSegment(sketch, "E40.left", {"start": v(14.33, 3.05) * mm, "end": v(14.33, -2.94) * mm});
            skLineSegment(sketch, "E40.right", {"start": v(22.96, 3.05) * mm, "end": v(22.96, -2.94) * mm});
            skSolve(sketch);
        }
        {
            var Q0;
            {var subQ0=sQuery(id+"F4.wireOp",EDGE,"E25");Q0=makeQuery(id+"F4.imprint","IMPRINT",FACE,{"disambiguationData":[TD([[makeQuery(id+"F4.imprint","IMPRINT",EDGE,{"derivedFrom":subQ0}),1.0]])]});}
            var Q1;
            {var subQ0=sQuery(id+"F4.wireOp",EDGE,"E23");Q1=makeQuery(id+"F4.imprint","IMPRINT",FACE,{"disambiguationData":[TD([[makeQuery(id+"F4.imprint","IMPRINT",EDGE,{"derivedFrom":subQ0}),1.0]])]});}
            var Q2;
            {var subQ0=sQuery(id+"F4.wireOp",EDGE,"E29.MirrorCS");Q2=makeQuery(id+"F4.imprint","IMPRINT",FACE,{"disambiguationData":[TD([[makeQuery(id+"F4.imprint","IMPRINT",EDGE,{"derivedFrom":subQ0}),-1.0]])]});}
            var Q3;
            {var subQ0=sQuery(id+"F4.wireOp",EDGE,"E27.MirrorCS");Q3=makeQuery(id+"F4.imprint","IMPRINT",FACE,{"disambiguationData":[TD([[makeQuery(id+"F4.imprint","IMPRINT",EDGE,{"derivedFrom":subQ0}),-1.0]])]});}
            var Q4;
            {var subQ0=sQuery(id+"F4.wireOp",EDGE,"E37.MirrorCS");Q4=makeQuery(id+"F4.imprint","IMPRINT",FACE,{"disambiguationData":[TD([[makeQuery(id+"F4.imprint","IMPRINT",EDGE,{"derivedFrom":subQ0}),1.0]])]});}
            var Q5;
            {var subQ0=sQuery(id+"F4.wireOp",EDGE,"E31.MirrorCS");Q5=makeQuery(id+"F4.imprint","IMPRINT",FACE,{"disambiguationData":[TD([[makeQuery(id+"F4.imprint","IMPRINT",EDGE,{"derivedFrom":subQ0}),1.0]])]});}
            var Q6;
            {var subQ0=sQuery(id+"F4.wireOp",EDGE,"E33.MirrorCS");Q6=makeQuery(id+"F4.imprint","IMPRINT",FACE,{"disambiguationData":[TD([[makeQuery(id+"F4.imprint","IMPRINT",EDGE,{"derivedFrom":subQ0}),1.0]])]});}
            var Q7;
            {var subQ0=sQuery(id+"F4.wireOp",EDGE,"E35.MirrorCS");Q7=makeQuery(id+"F4.imprint","IMPRINT",FACE,{"disambiguationData":[TD([[makeQuery(id+"F4.imprint","IMPRINT",EDGE,{"derivedFrom":subQ0}),1.0]])]});}
            var Q8;
            Q8=makeQuery(id+"F4.imprint","IMPRINT",FACE,{"disambiguationData":[TD([[makeQuery(id+"F4.imprint","IMPRINT",EDGE,{"derivedFrom":sQuery(id+"F4.wireOp",EDGE,"E39.top")}),1.0]])]});
            var Q9;
            Q9=makeQuery(id+"F4.imprint","IMPRINT",FACE,{"disambiguationData":[TD([[makeQuery(id+"F4.imprint","IMPRINT",EDGE,{"derivedFrom":sQuery(id+"F4.wireOp",EDGE,"E40.bottom")}),-1.0]])]});
            var Q10;
            {var subQ0=sQuery(id+"F4.wireOp",EDGE,"E14.MirrorCS");Q10=makeQuery(id+"F4.imprint","IMPRINT",FACE,{"disambiguationData":[TD([[makeQuery(id+"F4.imprint","IMPRINT",EDGE,{"derivedFrom":subQ0}),1.0]])]});}
            var Q11;
            {var subQ0=sQuery(id+"F4.wireOp",EDGE,"E12.MirrorCS");Q11=makeQuery(id+"F4.imprint","IMPRINT",FACE,{"disambiguationData":[TD([[makeQuery(id+"F4.imprint","IMPRINT",EDGE,{"derivedFrom":subQ0}),-1.0]])]});}
            var Q12;
            {var subQ0=sQuery(id+"F4.wireOp",EDGE,"E7.MirrorCS");Q12=makeQuery(id+"F4.imprint","IMPRINT",FACE,{"disambiguationData":[TD([[makeQuery(id+"F4.imprint","IMPRINT",EDGE,{"derivedFrom":subQ0}),1.0]])]});}
            var Q13;
            {var subQ0=sQuery(id+"F4.wireOp",EDGE,"E5");Q13=makeQuery(id+"F4.imprint","IMPRINT",FACE,{"disambiguationData":[TD([[makeQuery(id+"F4.imprint","IMPRINT",EDGE,{"derivedFrom":subQ0}),-1.0]])]});}
            extrude(context, id + "F5", {"entities" : qUnion([Q0, Q1, Q2, Q3, Q4, Q5, Q6, Q7, Q8, Q9, Q10, Q11, Q12, Q13]), "operationType" : NewBodyOperationType.REMOVE, "oppositeDirection" : true, "depth" : 25 * mm, "offsetDistance" : 25 * mm});
        }
        {
            var Q0;
            Q0=makeQuery(id+"F1.opExtrude","SWEPT_EDGE",EDGE,{"disambiguationData":[OSD([sQuery(id+"F0.wireOp",EDGE,"E4.15.0"),sQuery(id+"F0.wireOp",EDGE,"E4.15.1")])]});
            var Q1;
            Q1=makeQuery(id+"F1.opExtrude","SWEPT_EDGE",EDGE,{"disambiguationData":[OSD([sQuery(id+"F0.wireOp",EDGE,"E4.16.0"),sQuery(id+"F0.wireOp",EDGE,"E4.16.1")])]});
            var Q2;
            Q2=makeQuery(id+"F1.opExtrude","SWEPT_EDGE",EDGE,{"disambiguationData":[OSD([sQuery(id+"F0.wireOp",EDGE,"E4.17.0"),sQuery(id+"F0.wireOp",EDGE,"E4.17.1")])]});
            var Q3;
            Q3=makeQuery(id+"F1.opExtrude","SWEPT_EDGE",EDGE,{"disambiguationData":[OSD([sQuery(id+"F0.wireOp",EDGE,"E4.18.0"),sQuery(id+"F0.wireOp",EDGE,"E4.18.1")])]});
            var Q4;
            Q4=makeQuery(id+"F1.opExtrude","SWEPT_EDGE",EDGE,{"disambiguationData":[OSD([sQuery(id+"F0.wireOp",EDGE,"E4.19.0"),sQuery(id+"F0.wireOp",EDGE,"E4.19.1")])]});
            var Q5;
            Q5=makeQuery(id+"F1.opExtrude","SWEPT_EDGE",EDGE,{"disambiguationData":[OSD([sQuery(id+"F0.wireOp",EDGE,"E4.20.0"),sQuery(id+"F0.wireOp",EDGE,"E4.20.1")])]});
            var Q6;
            Q6=makeQuery(id+"F1.opExtrude","SWEPT_EDGE",EDGE,{"disambiguationData":[OSD([sQuery(id+"F0.wireOp",EDGE,"E4.21.0"),sQuery(id+"F0.wireOp",EDGE,"E4.21.1")])]});
            var Q7;
            Q7=makeQuery(id+"F1.opExtrude","SWEPT_EDGE",EDGE,{"disambiguationData":[OSD([sQuery(id+"F0.wireOp",EDGE,"E4.22.0"),sQuery(id+"F0.wireOp",EDGE,"E4.22.1")])]});
            var Q8;
            Q8=makeQuery(id+"F1.opExtrude","SWEPT_EDGE",EDGE,{"disambiguationData":[OSD([sQuery(id+"F0.wireOp",EDGE,"E4.23.0"),sQuery(id+"F0.wireOp",EDGE,"E4.23.1")])]});
            var Q9;
            Q9=makeQuery(id+"F1.opExtrude","SWEPT_EDGE",EDGE,{"disambiguationData":[OSD([sQuery(id+"F0.wireOp",EDGE,"E4.24.0"),sQuery(id+"F0.wireOp",EDGE,"E4.24.1")])]});
            var Q10;
            Q10=makeQuery(id+"F1.opExtrude","SWEPT_EDGE",EDGE,{"disambiguationData":[OSD([sQuery(id+"F0.wireOp",EDGE,"E4.25.0"),sQuery(id+"F0.wireOp",EDGE,"E4.25.1")])]});
            var Q11;
            Q11=makeQuery(id+"F1.opExtrude","SWEPT_EDGE",EDGE,{"disambiguationData":[OSD([sQuery(id+"F0.wireOp",EDGE,"E4.26.0"),sQuery(id+"F0.wireOp",EDGE,"E4.26.1")])]});
            var Q12;
            Q12=makeQuery(id+"F1.opExtrude","SWEPT_EDGE",EDGE,{"disambiguationData":[OSD([sQuery(id+"F0.wireOp",EDGE,"E4.27.0"),sQuery(id+"F0.wireOp",EDGE,"E4.27.1")])]});
            var Q13;
            Q13=makeQuery(id+"F1.opExtrude","SWEPT_EDGE",EDGE,{"disambiguationData":[OSD([sQuery(id+"F0.wireOp",EDGE,"E4.28.0"),sQuery(id+"F0.wireOp",EDGE,"E4.28.1")])]});
            var Q14;
            Q14=makeQuery(id+"F1.opExtrude","SWEPT_EDGE",EDGE,{"disambiguationData":[OSD([sQuery(id+"F0.wireOp",EDGE,"E4.29.0"),sQuery(id+"F0.wireOp",EDGE,"E4.29.1")])]});
            var Q15;
            Q15=makeQuery(id+"F1.opExtrude","SWEPT_EDGE",EDGE,{"disambiguationData":[OSD([sQuery(id+"F0.wireOp",EDGE,"E2"),sQuery(id+"F0.wireOp",EDGE,"E3")])]});
            var Q16;
            Q16=makeQuery(id+"F1.opExtrude","SWEPT_EDGE",EDGE,{"disambiguationData":[OSD([sQuery(id+"F0.wireOp",EDGE,"E4.1.0"),sQuery(id+"F0.wireOp",EDGE,"E4.1.1")])]});
            var Q17;
            Q17=makeQuery(id+"F1.opExtrude","SWEPT_EDGE",EDGE,{"disambiguationData":[OSD([sQuery(id+"F0.wireOp",EDGE,"E4.2.0"),sQuery(id+"F0.wireOp",EDGE,"E4.2.1")])]});
            var Q18;
            Q18=makeQuery(id+"F1.opExtrude","SWEPT_EDGE",EDGE,{"disambiguationData":[OSD([sQuery(id+"F0.wireOp",EDGE,"E4.3.0"),sQuery(id+"F0.wireOp",EDGE,"E4.3.1")])]});
            var Q19;
            Q19=makeQuery(id+"F1.opExtrude","SWEPT_EDGE",EDGE,{"disambiguationData":[OSD([sQuery(id+"F0.wireOp",EDGE,"E4.4.0"),sQuery(id+"F0.wireOp",EDGE,"E4.4.1")])]});
            var Q20;
            Q20=makeQuery(id+"F1.opExtrude","SWEPT_EDGE",EDGE,{"disambiguationData":[OSD([sQuery(id+"F0.wireOp",EDGE,"E4.5.0"),sQuery(id+"F0.wireOp",EDGE,"E4.5.1")])]});
            var Q21;
            Q21=makeQuery(id+"F1.opExtrude","SWEPT_EDGE",EDGE,{"disambiguationData":[OSD([sQuery(id+"F0.wireOp",EDGE,"E4.6.0"),sQuery(id+"F0.wireOp",EDGE,"E4.6.1")])]});
            var Q22;
            Q22=makeQuery(id+"F1.opExtrude","SWEPT_EDGE",EDGE,{"disambiguationData":[OSD([sQuery(id+"F0.wireOp",EDGE,"E4.7.0"),sQuery(id+"F0.wireOp",EDGE,"E4.7.1")])]});
            var Q23;
            Q23=makeQuery(id+"F1.opExtrude","SWEPT_EDGE",EDGE,{"disambiguationData":[OSD([sQuery(id+"F0.wireOp",EDGE,"E4.8.0"),sQuery(id+"F0.wireOp",EDGE,"E4.8.1")])]});
            var Q24;
            Q24=makeQuery(id+"F1.opExtrude","SWEPT_EDGE",EDGE,{"disambiguationData":[OSD([sQuery(id+"F0.wireOp",EDGE,"E4.9.0"),sQuery(id+"F0.wireOp",EDGE,"E4.9.1")])]});
            var Q25;
            Q25=makeQuery(id+"F1.opExtrude","SWEPT_EDGE",EDGE,{"disambiguationData":[OSD([sQuery(id+"F0.wireOp",EDGE,"E4.10.0"),sQuery(id+"F0.wireOp",EDGE,"E4.10.1")])]});
            var Q26;
            Q26=makeQuery(id+"F1.opExtrude","SWEPT_EDGE",EDGE,{"disambiguationData":[OSD([sQuery(id+"F0.wireOp",EDGE,"E4.11.0"),sQuery(id+"F0.wireOp",EDGE,"E4.11.1")])]});
            var Q27;
            Q27=makeQuery(id+"F1.opExtrude","SWEPT_EDGE",EDGE,{"disambiguationData":[OSD([sQuery(id+"F0.wireOp",EDGE,"E4.13.0"),sQuery(id+"F0.wireOp",EDGE,"E4.13.1")])]});
            var Q28;
            Q28=makeQuery(id+"F1.opExtrude","SWEPT_EDGE",EDGE,{"disambiguationData":[OSD([sQuery(id+"F0.wireOp",EDGE,"E4.14.0"),sQuery(id+"F0.wireOp",EDGE,"E4.14.1")])]});
            fillet(context, id + "F6", {"entities" : qUnion([Q0, Q1, Q2, Q3, Q4, Q5, Q6, Q7, Q8, Q9, Q10, Q11, Q12, Q13, Q14, Q15, Q16, Q17, Q18, Q19, Q20, Q21, Q22, Q23, Q24, Q25, Q26, Q27, Q28]), "radius" : 1 * mm, "tangentPropagation" : true, "allowEdgeOverflow" : false});
        }
        {
            var Q0;
            Q0=makeQuery(id+"F1.opExtrude","SWEPT_EDGE",EDGE,{"disambiguationData":[OSD([sQuery(id+"F0.wireOp",EDGE,"E4.12.0"),sQuery(id+"F0.wireOp",EDGE,"E4.12.1")])]});
            fillet(context, id + "F7", {"entities" : qUnion([Q0]), "radius" : 1 * mm, "tangentPropagation" : true, "allowEdgeOverflow" : false});
        }
        {
            var Q0;
            {var subQ0=sQuery(id+"F4.wireOp",EDGE,"E18.MirrorCS");Q0=makeQuery(id+"F5.boolean.opBoolean","COPY",EDGE,{"derivedFrom":makeQuery(id+"F5.opExtrude","CAP_EDGE",EDGE,{"disambiguationData":[OSD([subQ0]),TDD([makeQuery(id+"F4.imprint","IMPRINT",EDGE,{"disambiguationData":[TD([[makeQuery(id+"F4.imprint","INTERSECT",VERTEX,{"derivedFrom":[sQuery(id+"F4.wireOp",EDGE,"E7.MirrorCS"),subQ0]}),-1.0]])],"derivedFrom":subQ0}),makeQuery(id+"F4.imprint","IMPRINT",EDGE,{"disambiguationData":[TD([[makeQuery(id+"F4.imprint","INTERSECT",VERTEX,{"derivedFrom":[subQ0,sQuery(id+"F4.wireOp",EDGE,"E29.MirrorCS")]}),1.0]])],"derivedFrom":subQ0})])],"isStart":true})});}
            var Q1;
            Q1=makeQuery(id+"F5.boolean.opBoolean","COPY",EDGE,{"derivedFrom":makeQuery(id+"F5.opExtrude","CAP_EDGE",EDGE,{"disambiguationData":[OSD([sQuery(id+"F4.wireOp",EDGE,"E29.MirrorCS")])],"isStart":true})});
            var Q2;
            {var subQ0=sQuery(id+"F4.wireOp",EDGE,"E17.MirrorCS");Q2=makeQuery(id+"F5.boolean.opBoolean","COPY",EDGE,{"derivedFrom":makeQuery(id+"F5.opExtrude","CAP_EDGE",EDGE,{"disambiguationData":[OSD([subQ0]),TDD([makeQuery(id+"F4.imprint","IMPRINT",EDGE,{"disambiguationData":[TD([[makeQuery(id+"F4.imprint","INTERSECT",VERTEX,{"derivedFrom":[sQuery(id+"F4.wireOp",EDGE,"E7.MirrorCS"),subQ0]}),-1.0]])],"derivedFrom":subQ0}),makeQuery(id+"F4.imprint","IMPRINT",EDGE,{"disambiguationData":[TD([[makeQuery(id+"F4.imprint","INTERSECT",VERTEX,{"derivedFrom":[subQ0,sQuery(id+"F4.wireOp",EDGE,"E29.MirrorCS")]}),1.0]])],"derivedFrom":subQ0})])],"isStart":true})});}
            var Q3;
            Q3=makeQuery(id+"F5.boolean.opBoolean","COPY",EDGE,{"derivedFrom":makeQuery(id+"F5.opExtrude","CAP_EDGE",EDGE,{"disambiguationData":[OSD([sQuery(id+"F4.wireOp",EDGE,"E7.MirrorCS")])],"isStart":true})});
            var Q4;
            {var subQ0=sQuery(id+"F4.wireOp",EDGE,"E21.MirrorCS");var subQ1=makeQuery(id+"F4.imprint","INTERSECT",VERTEX,{"derivedFrom":[subQ0,sQuery(id+"F4.wireOp",EDGE,"E31.MirrorCS")]});Q4=makeQuery(id+"F5.boolean.opBoolean","COPY",EDGE,{"derivedFrom":makeQuery(id+"F5.opExtrude","CAP_EDGE",EDGE,{"disambiguationData":[OSD([subQ0]),TDD([makeQuery(id+"F4.imprint","IMPRINT",EDGE,{"disambiguationData":[TD([[makeQuery(id+"F4.imprint","INTERSECT",VERTEX,{"derivedFrom":[sQuery(id+"F4.wireOp",EDGE,"E14.MirrorCS"),subQ0]}),-1.0]])],"derivedFrom":subQ0}),makeQuery(id+"F4.imprint","IMPRINT",EDGE,{"disambiguationData":[TD([[subQ1,-1.0]])],"derivedFrom":subQ0})])],"isStart":true})});}
            var Q5;
            Q5=makeQuery(id+"F5.boolean.opBoolean","COPY",EDGE,{"derivedFrom":makeQuery(id+"F5.opExtrude","CAP_EDGE",EDGE,{"disambiguationData":[OSD([sQuery(id+"F4.wireOp",EDGE,"E32.MirrorCS")])],"isStart":true})});
            var Q6;
            {var subQ0=sQuery(id+"F4.wireOp",EDGE,"E22.MirrorCS");var subQ1=makeQuery(id+"F4.imprint","INTERSECT",VERTEX,{"derivedFrom":[subQ0,sQuery(id+"F4.wireOp",EDGE,"E31.MirrorCS")]});Q6=makeQuery(id+"F5.boolean.opBoolean","COPY",EDGE,{"derivedFrom":makeQuery(id+"F5.opExtrude","CAP_EDGE",EDGE,{"disambiguationData":[OSD([subQ0]),TDD([makeQuery(id+"F4.imprint","IMPRINT",EDGE,{"disambiguationData":[TD([[makeQuery(id+"F4.imprint","INTERSECT",VERTEX,{"derivedFrom":[sQuery(id+"F4.wireOp",EDGE,"E14.MirrorCS"),subQ0]}),-1.0]])],"derivedFrom":subQ0}),makeQuery(id+"F4.imprint","IMPRINT",EDGE,{"disambiguationData":[TD([[subQ1,-1.0]])],"derivedFrom":subQ0})])],"isStart":true})});}
            var Q7;
            Q7=makeQuery(id+"F5.boolean.opBoolean","COPY",EDGE,{"derivedFrom":makeQuery(id+"F5.opExtrude","CAP_EDGE",EDGE,{"disambiguationData":[OSD([sQuery(id+"F4.wireOp",EDGE,"E14.MirrorCS")])],"isStart":true})});
            var Q8;
            {var subQ0=sQuery(id+"F4.wireOp",EDGE,"E20.MirrorCS");Q8=makeQuery(id+"F5.boolean.opBoolean","COPY",EDGE,{"derivedFrom":makeQuery(id+"F5.opExtrude","CAP_EDGE",EDGE,{"disambiguationData":[OSD([subQ0]),TDD([makeQuery(id+"F4.imprint","IMPRINT",EDGE,{"disambiguationData":[TD([[makeQuery(id+"F4.imprint","INTERSECT",VERTEX,{"derivedFrom":[sQuery(id+"F4.wireOp",EDGE,"E12.MirrorCS"),subQ0]}),-1.0]])],"derivedFrom":subQ0}),makeQuery(id+"F4.imprint","IMPRINT",EDGE,{"disambiguationData":[TD([[makeQuery(id+"F4.imprint","INTERSECT",VERTEX,{"derivedFrom":[subQ0,sQuery(id+"F4.wireOp",EDGE,"E37.MirrorCS")]}),1.0]])],"derivedFrom":subQ0})])],"isStart":true})});}
            var Q9;
            {var subQ0=sQuery(id+"F4.wireOp",EDGE,"E19.MirrorCS");Q9=makeQuery(id+"F5.boolean.opBoolean","COPY",EDGE,{"derivedFrom":makeQuery(id+"F5.opExtrude","CAP_EDGE",EDGE,{"disambiguationData":[OSD([subQ0]),TDD([makeQuery(id+"F4.imprint","IMPRINT",EDGE,{"disambiguationData":[TD([[makeQuery(id+"F4.imprint","INTERSECT",VERTEX,{"derivedFrom":[sQuery(id+"F4.wireOp",EDGE,"E12.MirrorCS"),subQ0]}),-1.0]])],"derivedFrom":subQ0}),makeQuery(id+"F4.imprint","IMPRINT",EDGE,{"disambiguationData":[TD([[makeQuery(id+"F4.imprint","INTERSECT",VERTEX,{"derivedFrom":[subQ0,sQuery(id+"F4.wireOp",EDGE,"E37.MirrorCS")]}),1.0]])],"derivedFrom":subQ0})])],"isStart":true})});}
            var Q10;
            Q10=makeQuery(id+"F5.boolean.opBoolean","COPY",EDGE,{"derivedFrom":makeQuery(id+"F5.opExtrude","CAP_EDGE",EDGE,{"disambiguationData":[OSD([sQuery(id+"F4.wireOp",EDGE,"E37.MirrorCS")])],"isStart":true})});
            var Q11;
            {var subQ0=sQuery(id+"F4.wireOp",EDGE,"E16");Q11=makeQuery(id+"F5.boolean.opBoolean","COPY",EDGE,{"derivedFrom":makeQuery(id+"F5.opExtrude","CAP_EDGE",EDGE,{"disambiguationData":[OSD([subQ0]),TDD([makeQuery(id+"F4.imprint","IMPRINT",EDGE,{"disambiguationData":[TD([[makeQuery(id+"F4.imprint","INTERSECT",VERTEX,{"derivedFrom":[sQuery(id+"F4.wireOp",EDGE,"E5"),subQ0]}),-1.0]])],"derivedFrom":subQ0}),makeQuery(id+"F4.imprint","IMPRINT",EDGE,{"disambiguationData":[TD([[makeQuery(id+"F4.imprint","INTERSECT",VERTEX,{"derivedFrom":[subQ0,sQuery(id+"F4.wireOp",EDGE,"E25")]}),1.0]])],"derivedFrom":subQ0})])],"isStart":true})});}
            var Q12;
            {var subQ0=sQuery(id+"F4.wireOp",EDGE,"E15");Q12=makeQuery(id+"F5.boolean.opBoolean","COPY",EDGE,{"derivedFrom":makeQuery(id+"F5.opExtrude","CAP_EDGE",EDGE,{"disambiguationData":[OSD([subQ0]),TDD([makeQuery(id+"F4.imprint","IMPRINT",EDGE,{"disambiguationData":[TD([[makeQuery(id+"F4.imprint","INTERSECT",VERTEX,{"derivedFrom":[sQuery(id+"F4.wireOp",EDGE,"E5"),subQ0]}),-1.0]])],"derivedFrom":subQ0}),makeQuery(id+"F4.imprint","IMPRINT",EDGE,{"disambiguationData":[TD([[makeQuery(id+"F4.imprint","INTERSECT",VERTEX,{"derivedFrom":[subQ0,sQuery(id+"F4.wireOp",EDGE,"E25")]}),1.0]])],"derivedFrom":subQ0})])],"isStart":true})});}
            var Q13;
            Q13=makeQuery(id+"F5.boolean.opBoolean","COPY",EDGE,{"derivedFrom":makeQuery(id+"F5.opExtrude","CAP_EDGE",EDGE,{"disambiguationData":[OSD([sQuery(id+"F4.wireOp",EDGE,"E25")])],"isStart":true})});
            var Q14;
            Q14=makeQuery(id+"F5.boolean.opBoolean","COPY",EDGE,{"derivedFrom":makeQuery(id+"F5.opExtrude","CAP_EDGE",EDGE,{"disambiguationData":[OSD([sQuery(id+"F4.wireOp",EDGE,"E5")])],"isStart":true})});
            var Q15;
            Q15=makeQuery(id+"F5.boolean.opBoolean","COPY",EDGE,{"derivedFrom":makeQuery(id+"F5.opExtrude","CAP_EDGE",EDGE,{"disambiguationData":[OSD([sQuery(id+"F4.wireOp",EDGE,"E12.MirrorCS")])],"isStart":true})});
            var Q16;
            {var subQ0=sQuery(id+"F4.wireOp",EDGE,"E20.MirrorCS");Q16=makeQuery(id+"F5.boolean.opBoolean","INTERSECT",EDGE,{"derivedFrom":[makeQuery(id+"F1.opExtrude","CAP_FACE",FACE,{"disambiguationData":[OSD([sQuery(id+"F0.wireOp",EDGE,"E0"),sQuery(id+"F0.wireOp",EDGE,"E2"),sQuery(id+"F0.wireOp",EDGE,"E3"),sQuery(id+"F0.wireOp",EDGE,"E4.1.0"),sQuery(id+"F0.wireOp",EDGE,"E4.1.1"),sQuery(id+"F0.wireOp",EDGE,"E4.2.0"),sQuery(id+"F0.wireOp",EDGE,"E4.2.1"),sQuery(id+"F0.wireOp",EDGE,"E4.3.0"),sQuery(id+"F0.wireOp",EDGE,"E4.3.1"),sQuery(id+"F0.wireOp",EDGE,"E4.4.0"),sQuery(id+"F0.wireOp",EDGE,"E4.4.1"),sQuery(id+"F0.wireOp",EDGE,"E4.5.0"),sQuery(id+"F0.wireOp",EDGE,"E4.5.1"),sQuery(id+"F0.wireOp",EDGE,"E4.6.0"),sQuery(id+"F0.wireOp",EDGE,"E4.6.1"),sQuery(id+"F0.wireOp",EDGE,"E4.7.0"),sQuery(id+"F0.wireOp",EDGE,"E4.7.1"),sQuery(id+"F0.wireOp",EDGE,"E4.8.0"),sQuery(id+"F0.wireOp",EDGE,"E4.8.1"),sQuery(id+"F0.wireOp",EDGE,"E4.9.0"),sQuery(id+"F0.wireOp",EDGE,"E4.9.1"),sQuery(id+"F0.wireOp",EDGE,"E4.10.0"),sQuery(id+"F0.wireOp",EDGE,"E4.10.1"),sQuery(id+"F0.wireOp",EDGE,"E4.11.0"),sQuery(id+"F0.wireOp",EDGE,"E4.11.1"),sQuery(id+"F0.wireOp",EDGE,"E4.12.0"),sQuery(id+"F0.wireOp",EDGE,"E4.12.1"),sQuery(id+"F0.wireOp",EDGE,"E4.13.0"),sQuery(id+"F0.wireOp",EDGE,"E4.13.1"),sQuery(id+"F0.wireOp",EDGE,"E4.14.0"),sQuery(id+"F0.wireOp",EDGE,"E4.14.1"),sQuery(id+"F0.wireOp",EDGE,"E4.15.0"),sQuery(id+"F0.wireOp",EDGE,"E4.15.1"),sQuery(id+"F0.wireOp",EDGE,"E4.16.0"),sQuery(id+"F0.wireOp",EDGE,"E4.16.1"),sQuery(id+"F0.wireOp",EDGE,"E4.17.0"),sQuery(id+"F0.wireOp",EDGE,"E4.17.1"),sQuery(id+"F0.wireOp",EDGE,"E4.18.0"),sQuery(id+"F0.wireOp",EDGE,"E4.18.1"),sQuery(id+"F0.wireOp",EDGE,"E4.19.0"),sQuery(id+"F0.wireOp",EDGE,"E4.19.1"),sQuery(id+"F0.wireOp",EDGE,"E4.20.0"),sQuery(id+"F0.wireOp",EDGE,"E4.20.1"),sQuery(id+"F0.wireOp",EDGE,"E4.21.0"),sQuery(id+"F0.wireOp",EDGE,"E4.21.1"),sQuery(id+"F0.wireOp",EDGE,"E4.22.0"),sQuery(id+"F0.wireOp",EDGE,"E4.22.1"),sQuery(id+"F0.wireOp",EDGE,"E4.23.0"),sQuery(id+"F0.wireOp",EDGE,"E4.23.1"),sQuery(id+"F0.wireOp",EDGE,"E4.24.0"),sQuery(id+"F0.wireOp",EDGE,"E4.24.1"),sQuery(id+"F0.wireOp",EDGE,"E4.25.0"),sQuery(id+"F0.wireOp",EDGE,"E4.25.1"),sQuery(id+"F0.wireOp",EDGE,"E4.26.0"),sQuery(id+"F0.wireOp",EDGE,"E4.26.1"),sQuery(id+"F0.wireOp",EDGE,"E4.27.0"),sQuery(id+"F0.wireOp",EDGE,"E4.27.1"),sQuery(id+"F0.wireOp",EDGE,"E4.28.0"),sQuery(id+"F0.wireOp",EDGE,"E4.28.1"),sQuery(id+"F0.wireOp",EDGE,"E4.29.0"),sQuery(id+"F0.wireOp",EDGE,"E4.29.1")])],"isStart":true}),makeQuery(id+"F5.opExtrude","SWEPT_FACE",FACE,{"disambiguationData":[OSD([subQ0]),TDD([makeQuery(id+"F4.imprint","IMPRINT",EDGE,{"disambiguationData":[TD([[makeQuery(id+"F4.imprint","INTERSECT",VERTEX,{"derivedFrom":[sQuery(id+"F4.wireOp",EDGE,"E12.MirrorCS"),subQ0]}),-1.0]])],"derivedFrom":subQ0}),makeQuery(id+"F4.imprint","IMPRINT",EDGE,{"disambiguationData":[TD([[makeQuery(id+"F4.imprint","INTERSECT",VERTEX,{"derivedFrom":[subQ0,sQuery(id+"F4.wireOp",EDGE,"E37.MirrorCS")]}),1.0]])],"derivedFrom":subQ0})])]})]});}
            var Q17;
            Q17=makeQuery(id+"F5.boolean.opBoolean","INTERSECT",EDGE,{"derivedFrom":[makeQuery(id+"F1.opExtrude","CAP_FACE",FACE,{"disambiguationData":[OSD([sQuery(id+"F0.wireOp",EDGE,"E0"),sQuery(id+"F0.wireOp",EDGE,"E2"),sQuery(id+"F0.wireOp",EDGE,"E3"),sQuery(id+"F0.wireOp",EDGE,"E4.1.0"),sQuery(id+"F0.wireOp",EDGE,"E4.1.1"),sQuery(id+"F0.wireOp",EDGE,"E4.2.0"),sQuery(id+"F0.wireOp",EDGE,"E4.2.1"),sQuery(id+"F0.wireOp",EDGE,"E4.3.0"),sQuery(id+"F0.wireOp",EDGE,"E4.3.1"),sQuery(id+"F0.wireOp",EDGE,"E4.4.0"),sQuery(id+"F0.wireOp",EDGE,"E4.4.1"),sQuery(id+"F0.wireOp",EDGE,"E4.5.0"),sQuery(id+"F0.wireOp",EDGE,"E4.5.1"),sQuery(id+"F0.wireOp",EDGE,"E4.6.0"),sQuery(id+"F0.wireOp",EDGE,"E4.6.1"),sQuery(id+"F0.wireOp",EDGE,"E4.7.0"),sQuery(id+"F0.wireOp",EDGE,"E4.7.1"),sQuery(id+"F0.wireOp",EDGE,"E4.8.0"),sQuery(id+"F0.wireOp",EDGE,"E4.8.1"),sQuery(id+"F0.wireOp",EDGE,"E4.9.0"),sQuery(id+"F0.wireOp",EDGE,"E4.9.1"),sQuery(id+"F0.wireOp",EDGE,"E4.10.0"),sQuery(id+"F0.wireOp",EDGE,"E4.10.1"),sQuery(id+"F0.wireOp",EDGE,"E4.11.0"),sQuery(id+"F0.wireOp",EDGE,"E4.11.1"),sQuery(id+"F0.wireOp",EDGE,"E4.12.0"),sQuery(id+"F0.wireOp",EDGE,"E4.12.1"),sQuery(id+"F0.wireOp",EDGE,"E4.13.0"),sQuery(id+"F0.wireOp",EDGE,"E4.13.1"),sQuery(id+"F0.wireOp",EDGE,"E4.14.0"),sQuery(id+"F0.wireOp",EDGE,"E4.14.1"),sQuery(id+"F0.wireOp",EDGE,"E4.15.0"),sQuery(id+"F0.wireOp",EDGE,"E4.15.1"),sQuery(id+"F0.wireOp",EDGE,"E4.16.0"),sQuery(id+"F0.wireOp",EDGE,"E4.16.1"),sQuery(id+"F0.wireOp",EDGE,"E4.17.0"),sQuery(id+"F0.wireOp",EDGE,"E4.17.1"),sQuery(id+"F0.wireOp",EDGE,"E4.18.0"),sQuery(id+"F0.wireOp",EDGE,"E4.18.1"),sQuery(id+"F0.wireOp",EDGE,"E4.19.0"),sQuery(id+"F0.wireOp",EDGE,"E4.19.1"),sQuery(id+"F0.wireOp",EDGE,"E4.20.0"),sQuery(id+"F0.wireOp",EDGE,"E4.20.1"),sQuery(id+"F0.wireOp",EDGE,"E4.21.0"),sQuery(id+"F0.wireOp",EDGE,"E4.21.1"),sQuery(id+"F0.wireOp",EDGE,"E4.22.0"),sQuery(id+"F0.wireOp",EDGE,"E4.22.1"),sQuery(id+"F0.wireOp",EDGE,"E4.23.0"),sQuery(id+"F0.wireOp",EDGE,"E4.23.1"),sQuery(id+"F0.wireOp",EDGE,"E4.24.0"),sQuery(id+"F0.wireOp",EDGE,"E4.24.1"),sQuery(id+"F0.wireOp",EDGE,"E4.25.0"),sQuery(id+"F0.wireOp",EDGE,"E4.25.1"),sQuery(id+"F0.wireOp",EDGE,"E4.26.0"),sQuery(id+"F0.wireOp",EDGE,"E4.26.1"),sQuery(id+"F0.wireOp",EDGE,"E4.27.0"),sQuery(id+"F0.wireOp",EDGE,"E4.27.1"),sQuery(id+"F0.wireOp",EDGE,"E4.28.0"),sQuery(id+"F0.wireOp",EDGE,"E4.28.1"),sQuery(id+"F0.wireOp",EDGE,"E4.29.0"),sQuery(id+"F0.wireOp",EDGE,"E4.29.1")])],"isStart":true}),makeQuery(id+"F5.opExtrude","SWEPT_FACE",FACE,{"disambiguationData":[OSD([sQuery(id+"F4.wireOp",EDGE,"E37.MirrorCS")])]})]});
            var Q18;
            {var subQ0=sQuery(id+"F4.wireOp",EDGE,"E19.MirrorCS");Q18=makeQuery(id+"F5.boolean.opBoolean","INTERSECT",EDGE,{"derivedFrom":[makeQuery(id+"F1.opExtrude","CAP_FACE",FACE,{"disambiguationData":[OSD([sQuery(id+"F0.wireOp",EDGE,"E0"),sQuery(id+"F0.wireOp",EDGE,"E2"),sQuery(id+"F0.wireOp",EDGE,"E3"),sQuery(id+"F0.wireOp",EDGE,"E4.1.0"),sQuery(id+"F0.wireOp",EDGE,"E4.1.1"),sQuery(id+"F0.wireOp",EDGE,"E4.2.0"),sQuery(id+"F0.wireOp",EDGE,"E4.2.1"),sQuery(id+"F0.wireOp",EDGE,"E4.3.0"),sQuery(id+"F0.wireOp",EDGE,"E4.3.1"),sQuery(id+"F0.wireOp",EDGE,"E4.4.0"),sQuery(id+"F0.wireOp",EDGE,"E4.4.1"),sQuery(id+"F0.wireOp",EDGE,"E4.5.0"),sQuery(id+"F0.wireOp",EDGE,"E4.5.1"),sQuery(id+"F0.wireOp",EDGE,"E4.6.0"),sQuery(id+"F0.wireOp",EDGE,"E4.6.1"),sQuery(id+"F0.wireOp",EDGE,"E4.7.0"),sQuery(id+"F0.wireOp",EDGE,"E4.7.1"),sQuery(id+"F0.wireOp",EDGE,"E4.8.0"),sQuery(id+"F0.wireOp",EDGE,"E4.8.1"),sQuery(id+"F0.wireOp",EDGE,"E4.9.0"),sQuery(id+"F0.wireOp",EDGE,"E4.9.1"),sQuery(id+"F0.wireOp",EDGE,"E4.10.0"),sQuery(id+"F0.wireOp",EDGE,"E4.10.1"),sQuery(id+"F0.wireOp",EDGE,"E4.11.0"),sQuery(id+"F0.wireOp",EDGE,"E4.11.1"),sQuery(id+"F0.wireOp",EDGE,"E4.12.0"),sQuery(id+"F0.wireOp",EDGE,"E4.12.1"),sQuery(id+"F0.wireOp",EDGE,"E4.13.0"),sQuery(id+"F0.wireOp",EDGE,"E4.13.1"),sQuery(id+"F0.wireOp",EDGE,"E4.14.0"),sQuery(id+"F0.wireOp",EDGE,"E4.14.1"),sQuery(id+"F0.wireOp",EDGE,"E4.15.0"),sQuery(id+"F0.wireOp",EDGE,"E4.15.1"),sQuery(id+"F0.wireOp",EDGE,"E4.16.0"),sQuery(id+"F0.wireOp",EDGE,"E4.16.1"),sQuery(id+"F0.wireOp",EDGE,"E4.17.0"),sQuery(id+"F0.wireOp",EDGE,"E4.17.1"),sQuery(id+"F0.wireOp",EDGE,"E4.18.0"),sQuery(id+"F0.wireOp",EDGE,"E4.18.1"),sQuery(id+"F0.wireOp",EDGE,"E4.19.0"),sQuery(id+"F0.wireOp",EDGE,"E4.19.1"),sQuery(id+"F0.wireOp",EDGE,"E4.20.0"),sQuery(id+"F0.wireOp",EDGE,"E4.20.1"),sQuery(id+"F0.wireOp",EDGE,"E4.21.0"),sQuery(id+"F0.wireOp",EDGE,"E4.21.1"),sQuery(id+"F0.wireOp",EDGE,"E4.22.0"),sQuery(id+"F0.wireOp",EDGE,"E4.22.1"),sQuery(id+"F0.wireOp",EDGE,"E4.23.0"),sQuery(id+"F0.wireOp",EDGE,"E4.23.1"),sQuery(id+"F0.wireOp",EDGE,"E4.24.0"),sQuery(id+"F0.wireOp",EDGE,"E4.24.1"),sQuery(id+"F0.wireOp",EDGE,"E4.25.0"),sQuery(id+"F0.wireOp",EDGE,"E4.25.1"),sQuery(id+"F0.wireOp",EDGE,"E4.26.0"),sQuery(id+"F0.wireOp",EDGE,"E4.26.1"),sQuery(id+"F0.wireOp",EDGE,"E4.27.0"),sQuery(id+"F0.wireOp",EDGE,"E4.27.1"),sQuery(id+"F0.wireOp",EDGE,"E4.28.0"),sQuery(id+"F0.wireOp",EDGE,"E4.28.1"),sQuery(id+"F0.wireOp",EDGE,"E4.29.0"),sQuery(id+"F0.wireOp",EDGE,"E4.29.1")])],"isStart":true}),makeQuery(id+"F5.opExtrude","SWEPT_FACE",FACE,{"disambiguationData":[OSD([subQ0]),TDD([makeQuery(id+"F4.imprint","IMPRINT",EDGE,{"disambiguationData":[TD([[makeQuery(id+"F4.imprint","INTERSECT",VERTEX,{"derivedFrom":[sQuery(id+"F4.wireOp",EDGE,"E12.MirrorCS"),subQ0]}),-1.0]])],"derivedFrom":subQ0}),makeQuery(id+"F4.imprint","IMPRINT",EDGE,{"disambiguationData":[TD([[makeQuery(id+"F4.imprint","INTERSECT",VERTEX,{"derivedFrom":[subQ0,sQuery(id+"F4.wireOp",EDGE,"E37.MirrorCS")]}),1.0]])],"derivedFrom":subQ0})])]})]});}
            var Q19;
            Q19=makeQuery(id+"F5.boolean.opBoolean","INTERSECT",EDGE,{"derivedFrom":[makeQuery(id+"F1.opExtrude","CAP_FACE",FACE,{"disambiguationData":[OSD([sQuery(id+"F0.wireOp",EDGE,"E0"),sQuery(id+"F0.wireOp",EDGE,"E2"),sQuery(id+"F0.wireOp",EDGE,"E3"),sQuery(id+"F0.wireOp",EDGE,"E4.1.0"),sQuery(id+"F0.wireOp",EDGE,"E4.1.1"),sQuery(id+"F0.wireOp",EDGE,"E4.2.0"),sQuery(id+"F0.wireOp",EDGE,"E4.2.1"),sQuery(id+"F0.wireOp",EDGE,"E4.3.0"),sQuery(id+"F0.wireOp",EDGE,"E4.3.1"),sQuery(id+"F0.wireOp",EDGE,"E4.4.0"),sQuery(id+"F0.wireOp",EDGE,"E4.4.1"),sQuery(id+"F0.wireOp",EDGE,"E4.5.0"),sQuery(id+"F0.wireOp",EDGE,"E4.5.1"),sQuery(id+"F0.wireOp",EDGE,"E4.6.0"),sQuery(id+"F0.wireOp",EDGE,"E4.6.1"),sQuery(id+"F0.wireOp",EDGE,"E4.7.0"),sQuery(id+"F0.wireOp",EDGE,"E4.7.1"),sQuery(id+"F0.wireOp",EDGE,"E4.8.0"),sQuery(id+"F0.wireOp",EDGE,"E4.8.1"),sQuery(id+"F0.wireOp",EDGE,"E4.9.0"),sQuery(id+"F0.wireOp",EDGE,"E4.9.1"),sQuery(id+"F0.wireOp",EDGE,"E4.10.0"),sQuery(id+"F0.wireOp",EDGE,"E4.10.1"),sQuery(id+"F0.wireOp",EDGE,"E4.11.0"),sQuery(id+"F0.wireOp",EDGE,"E4.11.1"),sQuery(id+"F0.wireOp",EDGE,"E4.12.0"),sQuery(id+"F0.wireOp",EDGE,"E4.12.1"),sQuery(id+"F0.wireOp",EDGE,"E4.13.0"),sQuery(id+"F0.wireOp",EDGE,"E4.13.1"),sQuery(id+"F0.wireOp",EDGE,"E4.14.0"),sQuery(id+"F0.wireOp",EDGE,"E4.14.1"),sQuery(id+"F0.wireOp",EDGE,"E4.15.0"),sQuery(id+"F0.wireOp",EDGE,"E4.15.1"),sQuery(id+"F0.wireOp",EDGE,"E4.16.0"),sQuery(id+"F0.wireOp",EDGE,"E4.16.1"),sQuery(id+"F0.wireOp",EDGE,"E4.17.0"),sQuery(id+"F0.wireOp",EDGE,"E4.17.1"),sQuery(id+"F0.wireOp",EDGE,"E4.18.0"),sQuery(id+"F0.wireOp",EDGE,"E4.18.1"),sQuery(id+"F0.wireOp",EDGE,"E4.19.0"),sQuery(id+"F0.wireOp",EDGE,"E4.19.1"),sQuery(id+"F0.wireOp",EDGE,"E4.20.0"),sQuery(id+"F0.wireOp",EDGE,"E4.20.1"),sQuery(id+"F0.wireOp",EDGE,"E4.21.0"),sQuery(id+"F0.wireOp",EDGE,"E4.21.1"),sQuery(id+"F0.wireOp",EDGE,"E4.22.0"),sQuery(id+"F0.wireOp",EDGE,"E4.22.1"),sQuery(id+"F0.wireOp",EDGE,"E4.23.0"),sQuery(id+"F0.wireOp",EDGE,"E4.23.1"),sQuery(id+"F0.wireOp",EDGE,"E4.24.0"),sQuery(id+"F0.wireOp",EDGE,"E4.24.1"),sQuery(id+"F0.wireOp",EDGE,"E4.25.0"),sQuery(id+"F0.wireOp",EDGE,"E4.25.1"),sQuery(id+"F0.wireOp",EDGE,"E4.26.0"),sQuery(id+"F0.wireOp",EDGE,"E4.26.1"),sQuery(id+"F0.wireOp",EDGE,"E4.27.0"),sQuery(id+"F0.wireOp",EDGE,"E4.27.1"),sQuery(id+"F0.wireOp",EDGE,"E4.28.0"),sQuery(id+"F0.wireOp",EDGE,"E4.28.1"),sQuery(id+"F0.wireOp",EDGE,"E4.29.0"),sQuery(id+"F0.wireOp",EDGE,"E4.29.1")])],"isStart":true}),makeQuery(id+"F5.opExtrude","SWEPT_FACE",FACE,{"disambiguationData":[OSD([sQuery(id+"F4.wireOp",EDGE,"E12.MirrorCS")])]})]});
            var Q20;
            {var subQ0=sQuery(id+"F4.wireOp",EDGE,"E22.MirrorCS");var subQ1=makeQuery(id+"F4.imprint","INTERSECT",VERTEX,{"derivedFrom":[subQ0,sQuery(id+"F4.wireOp",EDGE,"E31.MirrorCS")]});Q20=makeQuery(id+"F5.boolean.opBoolean","INTERSECT",EDGE,{"derivedFrom":[makeQuery(id+"F1.opExtrude","CAP_FACE",FACE,{"disambiguationData":[OSD([sQuery(id+"F0.wireOp",EDGE,"E0"),sQuery(id+"F0.wireOp",EDGE,"E2"),sQuery(id+"F0.wireOp",EDGE,"E3"),sQuery(id+"F0.wireOp",EDGE,"E4.1.0"),sQuery(id+"F0.wireOp",EDGE,"E4.1.1"),sQuery(id+"F0.wireOp",EDGE,"E4.2.0"),sQuery(id+"F0.wireOp",EDGE,"E4.2.1"),sQuery(id+"F0.wireOp",EDGE,"E4.3.0"),sQuery(id+"F0.wireOp",EDGE,"E4.3.1"),sQuery(id+"F0.wireOp",EDGE,"E4.4.0"),sQuery(id+"F0.wireOp",EDGE,"E4.4.1"),sQuery(id+"F0.wireOp",EDGE,"E4.5.0"),sQuery(id+"F0.wireOp",EDGE,"E4.5.1"),sQuery(id+"F0.wireOp",EDGE,"E4.6.0"),sQuery(id+"F0.wireOp",EDGE,"E4.6.1"),sQuery(id+"F0.wireOp",EDGE,"E4.7.0"),sQuery(id+"F0.wireOp",EDGE,"E4.7.1"),sQuery(id+"F0.wireOp",EDGE,"E4.8.0"),sQuery(id+"F0.wireOp",EDGE,"E4.8.1"),sQuery(id+"F0.wireOp",EDGE,"E4.9.0"),sQuery(id+"F0.wireOp",EDGE,"E4.9.1"),sQuery(id+"F0.wireOp",EDGE,"E4.10.0"),sQuery(id+"F0.wireOp",EDGE,"E4.10.1"),sQuery(id+"F0.wireOp",EDGE,"E4.11.0"),sQuery(id+"F0.wireOp",EDGE,"E4.11.1"),sQuery(id+"F0.wireOp",EDGE,"E4.12.0"),sQuery(id+"F0.wireOp",EDGE,"E4.12.1"),sQuery(id+"F0.wireOp",EDGE,"E4.13.0"),sQuery(id+"F0.wireOp",EDGE,"E4.13.1"),sQuery(id+"F0.wireOp",EDGE,"E4.14.0"),sQuery(id+"F0.wireOp",EDGE,"E4.14.1"),sQuery(id+"F0.wireOp",EDGE,"E4.15.0"),sQuery(id+"F0.wireOp",EDGE,"E4.15.1"),sQuery(id+"F0.wireOp",EDGE,"E4.16.0"),sQuery(id+"F0.wireOp",EDGE,"E4.16.1"),sQuery(id+"F0.wireOp",EDGE,"E4.17.0"),sQuery(id+"F0.wireOp",EDGE,"E4.17.1"),sQuery(id+"F0.wireOp",EDGE,"E4.18.0"),sQuery(id+"F0.wireOp",EDGE,"E4.18.1"),sQuery(id+"F0.wireOp",EDGE,"E4.19.0"),sQuery(id+"F0.wireOp",EDGE,"E4.19.1"),sQuery(id+"F0.wireOp",EDGE,"E4.20.0"),sQuery(id+"F0.wireOp",EDGE,"E4.20.1"),sQuery(id+"F0.wireOp",EDGE,"E4.21.0"),sQuery(id+"F0.wireOp",EDGE,"E4.21.1"),sQuery(id+"F0.wireOp",EDGE,"E4.22.0"),sQuery(id+"F0.wireOp",EDGE,"E4.22.1"),sQuery(id+"F0.wireOp",EDGE,"E4.23.0"),sQuery(id+"F0.wireOp",EDGE,"E4.23.1"),sQuery(id+"F0.wireOp",EDGE,"E4.24.0"),sQuery(id+"F0.wireOp",EDGE,"E4.24.1"),sQuery(id+"F0.wireOp",EDGE,"E4.25.0"),sQuery(id+"F0.wireOp",EDGE,"E4.25.1"),sQuery(id+"F0.wireOp",EDGE,"E4.26.0"),sQuery(id+"F0.wireOp",EDGE,"E4.26.1"),sQuery(id+"F0.wireOp",EDGE,"E4.27.0"),sQuery(id+"F0.wireOp",EDGE,"E4.27.1"),sQuery(id+"F0.wireOp",EDGE,"E4.28.0"),sQuery(id+"F0.wireOp",EDGE,"E4.28.1"),sQuery(id+"F0.wireOp",EDGE,"E4.29.0"),sQuery(id+"F0.wireOp",EDGE,"E4.29.1")])],"isStart":true}),makeQuery(id+"F5.opExtrude","SWEPT_FACE",FACE,{"disambiguationData":[OSD([subQ0]),TDD([makeQuery(id+"F4.imprint","IMPRINT",EDGE,{"disambiguationData":[TD([[makeQuery(id+"F4.imprint","INTERSECT",VERTEX,{"derivedFrom":[sQuery(id+"F4.wireOp",EDGE,"E14.MirrorCS"),subQ0]}),-1.0]])],"derivedFrom":subQ0}),makeQuery(id+"F4.imprint","IMPRINT",EDGE,{"disambiguationData":[TD([[subQ1,-1.0]])],"derivedFrom":subQ0})])]})]});}
            var Q21;
            Q21=makeQuery(id+"F5.boolean.opBoolean","INTERSECT",EDGE,{"derivedFrom":[makeQuery(id+"F1.opExtrude","CAP_FACE",FACE,{"disambiguationData":[OSD([sQuery(id+"F0.wireOp",EDGE,"E0"),sQuery(id+"F0.wireOp",EDGE,"E2"),sQuery(id+"F0.wireOp",EDGE,"E3"),sQuery(id+"F0.wireOp",EDGE,"E4.1.0"),sQuery(id+"F0.wireOp",EDGE,"E4.1.1"),sQuery(id+"F0.wireOp",EDGE,"E4.2.0"),sQuery(id+"F0.wireOp",EDGE,"E4.2.1"),sQuery(id+"F0.wireOp",EDGE,"E4.3.0"),sQuery(id+"F0.wireOp",EDGE,"E4.3.1"),sQuery(id+"F0.wireOp",EDGE,"E4.4.0"),sQuery(id+"F0.wireOp",EDGE,"E4.4.1"),sQuery(id+"F0.wireOp",EDGE,"E4.5.0"),sQuery(id+"F0.wireOp",EDGE,"E4.5.1"),sQuery(id+"F0.wireOp",EDGE,"E4.6.0"),sQuery(id+"F0.wireOp",EDGE,"E4.6.1"),sQuery(id+"F0.wireOp",EDGE,"E4.7.0"),sQuery(id+"F0.wireOp",EDGE,"E4.7.1"),sQuery(id+"F0.wireOp",EDGE,"E4.8.0"),sQuery(id+"F0.wireOp",EDGE,"E4.8.1"),sQuery(id+"F0.wireOp",EDGE,"E4.9.0"),sQuery(id+"F0.wireOp",EDGE,"E4.9.1"),sQuery(id+"F0.wireOp",EDGE,"E4.10.0"),sQuery(id+"F0.wireOp",EDGE,"E4.10.1"),sQuery(id+"F0.wireOp",EDGE,"E4.11.0"),sQuery(id+"F0.wireOp",EDGE,"E4.11.1"),sQuery(id+"F0.wireOp",EDGE,"E4.12.0"),sQuery(id+"F0.wireOp",EDGE,"E4.12.1"),sQuery(id+"F0.wireOp",EDGE,"E4.13.0"),sQuery(id+"F0.wireOp",EDGE,"E4.13.1"),sQuery(id+"F0.wireOp",EDGE,"E4.14.0"),sQuery(id+"F0.wireOp",EDGE,"E4.14.1"),sQuery(id+"F0.wireOp",EDGE,"E4.15.0"),sQuery(id+"F0.wireOp",EDGE,"E4.15.1"),sQuery(id+"F0.wireOp",EDGE,"E4.16.0"),sQuery(id+"F0.wireOp",EDGE,"E4.16.1"),sQuery(id+"F0.wireOp",EDGE,"E4.17.0"),sQuery(id+"F0.wireOp",EDGE,"E4.17.1"),sQuery(id+"F0.wireOp",EDGE,"E4.18.0"),sQuery(id+"F0.wireOp",EDGE,"E4.18.1"),sQuery(id+"F0.wireOp",EDGE,"E4.19.0"),sQuery(id+"F0.wireOp",EDGE,"E4.19.1"),sQuery(id+"F0.wireOp",EDGE,"E4.20.0"),sQuery(id+"F0.wireOp",EDGE,"E4.20.1"),sQuery(id+"F0.wireOp",EDGE,"E4.21.0"),sQuery(id+"F0.wireOp",EDGE,"E4.21.1"),sQuery(id+"F0.wireOp",EDGE,"E4.22.0"),sQuery(id+"F0.wireOp",EDGE,"E4.22.1"),sQuery(id+"F0.wireOp",EDGE,"E4.23.0"),sQuery(id+"F0.wireOp",EDGE,"E4.23.1"),sQuery(id+"F0.wireOp",EDGE,"E4.24.0"),sQuery(id+"F0.wireOp",EDGE,"E4.24.1"),sQuery(id+"F0.wireOp",EDGE,"E4.25.0"),sQuery(id+"F0.wireOp",EDGE,"E4.25.1"),sQuery(id+"F0.wireOp",EDGE,"E4.26.0"),sQuery(id+"F0.wireOp",EDGE,"E4.26.1"),sQuery(id+"F0.wireOp",EDGE,"E4.27.0"),sQuery(id+"F0.wireOp",EDGE,"E4.27.1"),sQuery(id+"F0.wireOp",EDGE,"E4.28.0"),sQuery(id+"F0.wireOp",EDGE,"E4.28.1"),sQuery(id+"F0.wireOp",EDGE,"E4.29.0"),sQuery(id+"F0.wireOp",EDGE,"E4.29.1")])],"isStart":true}),makeQuery(id+"F5.opExtrude","SWEPT_FACE",FACE,{"disambiguationData":[OSD([sQuery(id+"F4.wireOp",EDGE,"E14.MirrorCS")])]})]});
            var Q22;
            {var subQ0=sQuery(id+"F4.wireOp",EDGE,"E21.MirrorCS");var subQ1=makeQuery(id+"F4.imprint","INTERSECT",VERTEX,{"derivedFrom":[subQ0,sQuery(id+"F4.wireOp",EDGE,"E31.MirrorCS")]});Q22=makeQuery(id+"F5.boolean.opBoolean","INTERSECT",EDGE,{"derivedFrom":[makeQuery(id+"F1.opExtrude","CAP_FACE",FACE,{"disambiguationData":[OSD([sQuery(id+"F0.wireOp",EDGE,"E0"),sQuery(id+"F0.wireOp",EDGE,"E2"),sQuery(id+"F0.wireOp",EDGE,"E3"),sQuery(id+"F0.wireOp",EDGE,"E4.1.0"),sQuery(id+"F0.wireOp",EDGE,"E4.1.1"),sQuery(id+"F0.wireOp",EDGE,"E4.2.0"),sQuery(id+"F0.wireOp",EDGE,"E4.2.1"),sQuery(id+"F0.wireOp",EDGE,"E4.3.0"),sQuery(id+"F0.wireOp",EDGE,"E4.3.1"),sQuery(id+"F0.wireOp",EDGE,"E4.4.0"),sQuery(id+"F0.wireOp",EDGE,"E4.4.1"),sQuery(id+"F0.wireOp",EDGE,"E4.5.0"),sQuery(id+"F0.wireOp",EDGE,"E4.5.1"),sQuery(id+"F0.wireOp",EDGE,"E4.6.0"),sQuery(id+"F0.wireOp",EDGE,"E4.6.1"),sQuery(id+"F0.wireOp",EDGE,"E4.7.0"),sQuery(id+"F0.wireOp",EDGE,"E4.7.1"),sQuery(id+"F0.wireOp",EDGE,"E4.8.0"),sQuery(id+"F0.wireOp",EDGE,"E4.8.1"),sQuery(id+"F0.wireOp",EDGE,"E4.9.0"),sQuery(id+"F0.wireOp",EDGE,"E4.9.1"),sQuery(id+"F0.wireOp",EDGE,"E4.10.0"),sQuery(id+"F0.wireOp",EDGE,"E4.10.1"),sQuery(id+"F0.wireOp",EDGE,"E4.11.0"),sQuery(id+"F0.wireOp",EDGE,"E4.11.1"),sQuery(id+"F0.wireOp",EDGE,"E4.12.0"),sQuery(id+"F0.wireOp",EDGE,"E4.12.1"),sQuery(id+"F0.wireOp",EDGE,"E4.13.0"),sQuery(id+"F0.wireOp",EDGE,"E4.13.1"),sQuery(id+"F0.wireOp",EDGE,"E4.14.0"),sQuery(id+"F0.wireOp",EDGE,"E4.14.1"),sQuery(id+"F0.wireOp",EDGE,"E4.15.0"),sQuery(id+"F0.wireOp",EDGE,"E4.15.1"),sQuery(id+"F0.wireOp",EDGE,"E4.16.0"),sQuery(id+"F0.wireOp",EDGE,"E4.16.1"),sQuery(id+"F0.wireOp",EDGE,"E4.17.0"),sQuery(id+"F0.wireOp",EDGE,"E4.17.1"),sQuery(id+"F0.wireOp",EDGE,"E4.18.0"),sQuery(id+"F0.wireOp",EDGE,"E4.18.1"),sQuery(id+"F0.wireOp",EDGE,"E4.19.0"),sQuery(id+"F0.wireOp",EDGE,"E4.19.1"),sQuery(id+"F0.wireOp",EDGE,"E4.20.0"),sQuery(id+"F0.wireOp",EDGE,"E4.20.1"),sQuery(id+"F0.wireOp",EDGE,"E4.21.0"),sQuery(id+"F0.wireOp",EDGE,"E4.21.1"),sQuery(id+"F0.wireOp",EDGE,"E4.22.0"),sQuery(id+"F0.wireOp",EDGE,"E4.22.1"),sQuery(id+"F0.wireOp",EDGE,"E4.23.0"),sQuery(id+"F0.wireOp",EDGE,"E4.23.1"),sQuery(id+"F0.wireOp",EDGE,"E4.24.0"),sQuery(id+"F0.wireOp",EDGE,"E4.24.1"),sQuery(id+"F0.wireOp",EDGE,"E4.25.0"),sQuery(id+"F0.wireOp",EDGE,"E4.25.1"),sQuery(id+"F0.wireOp",EDGE,"E4.26.0"),sQuery(id+"F0.wireOp",EDGE,"E4.26.1"),sQuery(id+"F0.wireOp",EDGE,"E4.27.0"),sQuery(id+"F0.wireOp",EDGE,"E4.27.1"),sQuery(id+"F0.wireOp",EDGE,"E4.28.0"),sQuery(id+"F0.wireOp",EDGE,"E4.28.1"),sQuery(id+"F0.wireOp",EDGE,"E4.29.0"),sQuery(id+"F0.wireOp",EDGE,"E4.29.1")])],"isStart":true}),makeQuery(id+"F5.opExtrude","SWEPT_FACE",FACE,{"disambiguationData":[OSD([subQ0]),TDD([makeQuery(id+"F4.imprint","IMPRINT",EDGE,{"disambiguationData":[TD([[makeQuery(id+"F4.imprint","INTERSECT",VERTEX,{"derivedFrom":[sQuery(id+"F4.wireOp",EDGE,"E14.MirrorCS"),subQ0]}),-1.0]])],"derivedFrom":subQ0}),makeQuery(id+"F4.imprint","IMPRINT",EDGE,{"disambiguationData":[TD([[subQ1,-1.0]])],"derivedFrom":subQ0})])]})]});}
            var Q23;
            Q23=makeQuery(id+"F5.boolean.opBoolean","INTERSECT",EDGE,{"derivedFrom":[makeQuery(id+"F1.opExtrude","CAP_FACE",FACE,{"disambiguationData":[OSD([sQuery(id+"F0.wireOp",EDGE,"E0"),sQuery(id+"F0.wireOp",EDGE,"E2"),sQuery(id+"F0.wireOp",EDGE,"E3"),sQuery(id+"F0.wireOp",EDGE,"E4.1.0"),sQuery(id+"F0.wireOp",EDGE,"E4.1.1"),sQuery(id+"F0.wireOp",EDGE,"E4.2.0"),sQuery(id+"F0.wireOp",EDGE,"E4.2.1"),sQuery(id+"F0.wireOp",EDGE,"E4.3.0"),sQuery(id+"F0.wireOp",EDGE,"E4.3.1"),sQuery(id+"F0.wireOp",EDGE,"E4.4.0"),sQuery(id+"F0.wireOp",EDGE,"E4.4.1"),sQuery(id+"F0.wireOp",EDGE,"E4.5.0"),sQuery(id+"F0.wireOp",EDGE,"E4.5.1"),sQuery(id+"F0.wireOp",EDGE,"E4.6.0"),sQuery(id+"F0.wireOp",EDGE,"E4.6.1"),sQuery(id+"F0.wireOp",EDGE,"E4.7.0"),sQuery(id+"F0.wireOp",EDGE,"E4.7.1"),sQuery(id+"F0.wireOp",EDGE,"E4.8.0"),sQuery(id+"F0.wireOp",EDGE,"E4.8.1"),sQuery(id+"F0.wireOp",EDGE,"E4.9.0"),sQuery(id+"F0.wireOp",EDGE,"E4.9.1"),sQuery(id+"F0.wireOp",EDGE,"E4.10.0"),sQuery(id+"F0.wireOp",EDGE,"E4.10.1"),sQuery(id+"F0.wireOp",EDGE,"E4.11.0"),sQuery(id+"F0.wireOp",EDGE,"E4.11.1"),sQuery(id+"F0.wireOp",EDGE,"E4.12.0"),sQuery(id+"F0.wireOp",EDGE,"E4.12.1"),sQuery(id+"F0.wireOp",EDGE,"E4.13.0"),sQuery(id+"F0.wireOp",EDGE,"E4.13.1"),sQuery(id+"F0.wireOp",EDGE,"E4.14.0"),sQuery(id+"F0.wireOp",EDGE,"E4.14.1"),sQuery(id+"F0.wireOp",EDGE,"E4.15.0"),sQuery(id+"F0.wireOp",EDGE,"E4.15.1"),sQuery(id+"F0.wireOp",EDGE,"E4.16.0"),sQuery(id+"F0.wireOp",EDGE,"E4.16.1"),sQuery(id+"F0.wireOp",EDGE,"E4.17.0"),sQuery(id+"F0.wireOp",EDGE,"E4.17.1"),sQuery(id+"F0.wireOp",EDGE,"E4.18.0"),sQuery(id+"F0.wireOp",EDGE,"E4.18.1"),sQuery(id+"F0.wireOp",EDGE,"E4.19.0"),sQuery(id+"F0.wireOp",EDGE,"E4.19.1"),sQuery(id+"F0.wireOp",EDGE,"E4.20.0"),sQuery(id+"F0.wireOp",EDGE,"E4.20.1"),sQuery(id+"F0.wireOp",EDGE,"E4.21.0"),sQuery(id+"F0.wireOp",EDGE,"E4.21.1"),sQuery(id+"F0.wireOp",EDGE,"E4.22.0"),sQuery(id+"F0.wireOp",EDGE,"E4.22.1"),sQuery(id+"F0.wireOp",EDGE,"E4.23.0"),sQuery(id+"F0.wireOp",EDGE,"E4.23.1"),sQuery(id+"F0.wireOp",EDGE,"E4.24.0"),sQuery(id+"F0.wireOp",EDGE,"E4.24.1"),sQuery(id+"F0.wireOp",EDGE,"E4.25.0"),sQuery(id+"F0.wireOp",EDGE,"E4.25.1"),sQuery(id+"F0.wireOp",EDGE,"E4.26.0"),sQuery(id+"F0.wireOp",EDGE,"E4.26.1"),sQuery(id+"F0.wireOp",EDGE,"E4.27.0"),sQuery(id+"F0.wireOp",EDGE,"E4.27.1"),sQuery(id+"F0.wireOp",EDGE,"E4.28.0"),sQuery(id+"F0.wireOp",EDGE,"E4.28.1"),sQuery(id+"F0.wireOp",EDGE,"E4.29.0"),sQuery(id+"F0.wireOp",EDGE,"E4.29.1")])],"isStart":true}),makeQuery(id+"F5.opExtrude","SWEPT_FACE",FACE,{"disambiguationData":[OSD([sQuery(id+"F4.wireOp",EDGE,"E32.MirrorCS")])]})]});
            var Q24;
            {var subQ0=sQuery(id+"F4.wireOp",EDGE,"E17.MirrorCS");Q24=makeQuery(id+"F5.boolean.opBoolean","INTERSECT",EDGE,{"derivedFrom":[makeQuery(id+"F1.opExtrude","CAP_FACE",FACE,{"disambiguationData":[OSD([sQuery(id+"F0.wireOp",EDGE,"E0"),sQuery(id+"F0.wireOp",EDGE,"E2"),sQuery(id+"F0.wireOp",EDGE,"E3"),sQuery(id+"F0.wireOp",EDGE,"E4.1.0"),sQuery(id+"F0.wireOp",EDGE,"E4.1.1"),sQuery(id+"F0.wireOp",EDGE,"E4.2.0"),sQuery(id+"F0.wireOp",EDGE,"E4.2.1"),sQuery(id+"F0.wireOp",EDGE,"E4.3.0"),sQuery(id+"F0.wireOp",EDGE,"E4.3.1"),sQuery(id+"F0.wireOp",EDGE,"E4.4.0"),sQuery(id+"F0.wireOp",EDGE,"E4.4.1"),sQuery(id+"F0.wireOp",EDGE,"E4.5.0"),sQuery(id+"F0.wireOp",EDGE,"E4.5.1"),sQuery(id+"F0.wireOp",EDGE,"E4.6.0"),sQuery(id+"F0.wireOp",EDGE,"E4.6.1"),sQuery(id+"F0.wireOp",EDGE,"E4.7.0"),sQuery(id+"F0.wireOp",EDGE,"E4.7.1"),sQuery(id+"F0.wireOp",EDGE,"E4.8.0"),sQuery(id+"F0.wireOp",EDGE,"E4.8.1"),sQuery(id+"F0.wireOp",EDGE,"E4.9.0"),sQuery(id+"F0.wireOp",EDGE,"E4.9.1"),sQuery(id+"F0.wireOp",EDGE,"E4.10.0"),sQuery(id+"F0.wireOp",EDGE,"E4.10.1"),sQuery(id+"F0.wireOp",EDGE,"E4.11.0"),sQuery(id+"F0.wireOp",EDGE,"E4.11.1"),sQuery(id+"F0.wireOp",EDGE,"E4.12.0"),sQuery(id+"F0.wireOp",EDGE,"E4.12.1"),sQuery(id+"F0.wireOp",EDGE,"E4.13.0"),sQuery(id+"F0.wireOp",EDGE,"E4.13.1"),sQuery(id+"F0.wireOp",EDGE,"E4.14.0"),sQuery(id+"F0.wireOp",EDGE,"E4.14.1"),sQuery(id+"F0.wireOp",EDGE,"E4.15.0"),sQuery(id+"F0.wireOp",EDGE,"E4.15.1"),sQuery(id+"F0.wireOp",EDGE,"E4.16.0"),sQuery(id+"F0.wireOp",EDGE,"E4.16.1"),sQuery(id+"F0.wireOp",EDGE,"E4.17.0"),sQuery(id+"F0.wireOp",EDGE,"E4.17.1"),sQuery(id+"F0.wireOp",EDGE,"E4.18.0"),sQuery(id+"F0.wireOp",EDGE,"E4.18.1"),sQuery(id+"F0.wireOp",EDGE,"E4.19.0"),sQuery(id+"F0.wireOp",EDGE,"E4.19.1"),sQuery(id+"F0.wireOp",EDGE,"E4.20.0"),sQuery(id+"F0.wireOp",EDGE,"E4.20.1"),sQuery(id+"F0.wireOp",EDGE,"E4.21.0"),sQuery(id+"F0.wireOp",EDGE,"E4.21.1"),sQuery(id+"F0.wireOp",EDGE,"E4.22.0"),sQuery(id+"F0.wireOp",EDGE,"E4.22.1"),sQuery(id+"F0.wireOp",EDGE,"E4.23.0"),sQuery(id+"F0.wireOp",EDGE,"E4.23.1"),sQuery(id+"F0.wireOp",EDGE,"E4.24.0"),sQuery(id+"F0.wireOp",EDGE,"E4.24.1"),sQuery(id+"F0.wireOp",EDGE,"E4.25.0"),sQuery(id+"F0.wireOp",EDGE,"E4.25.1"),sQuery(id+"F0.wireOp",EDGE,"E4.26.0"),sQuery(id+"F0.wireOp",EDGE,"E4.26.1"),sQuery(id+"F0.wireOp",EDGE,"E4.27.0"),sQuery(id+"F0.wireOp",EDGE,"E4.27.1"),sQuery(id+"F0.wireOp",EDGE,"E4.28.0"),sQuery(id+"F0.wireOp",EDGE,"E4.28.1"),sQuery(id+"F0.wireOp",EDGE,"E4.29.0"),sQuery(id+"F0.wireOp",EDGE,"E4.29.1")])],"isStart":true}),makeQuery(id+"F5.opExtrude","SWEPT_FACE",FACE,{"disambiguationData":[OSD([subQ0]),TDD([makeQuery(id+"F4.imprint","IMPRINT",EDGE,{"disambiguationData":[TD([[makeQuery(id+"F4.imprint","INTERSECT",VERTEX,{"derivedFrom":[sQuery(id+"F4.wireOp",EDGE,"E7.MirrorCS"),subQ0]}),-1.0]])],"derivedFrom":subQ0}),makeQuery(id+"F4.imprint","IMPRINT",EDGE,{"disambiguationData":[TD([[makeQuery(id+"F4.imprint","INTERSECT",VERTEX,{"derivedFrom":[subQ0,sQuery(id+"F4.wireOp",EDGE,"E29.MirrorCS")]}),1.0]])],"derivedFrom":subQ0})])]})]});}
            var Q25;
            Q25=makeQuery(id+"F5.boolean.opBoolean","INTERSECT",EDGE,{"derivedFrom":[makeQuery(id+"F1.opExtrude","CAP_FACE",FACE,{"disambiguationData":[OSD([sQuery(id+"F0.wireOp",EDGE,"E0"),sQuery(id+"F0.wireOp",EDGE,"E2"),sQuery(id+"F0.wireOp",EDGE,"E3"),sQuery(id+"F0.wireOp",EDGE,"E4.1.0"),sQuery(id+"F0.wireOp",EDGE,"E4.1.1"),sQuery(id+"F0.wireOp",EDGE,"E4.2.0"),sQuery(id+"F0.wireOp",EDGE,"E4.2.1"),sQuery(id+"F0.wireOp",EDGE,"E4.3.0"),sQuery(id+"F0.wireOp",EDGE,"E4.3.1"),sQuery(id+"F0.wireOp",EDGE,"E4.4.0"),sQuery(id+"F0.wireOp",EDGE,"E4.4.1"),sQuery(id+"F0.wireOp",EDGE,"E4.5.0"),sQuery(id+"F0.wireOp",EDGE,"E4.5.1"),sQuery(id+"F0.wireOp",EDGE,"E4.6.0"),sQuery(id+"F0.wireOp",EDGE,"E4.6.1"),sQuery(id+"F0.wireOp",EDGE,"E4.7.0"),sQuery(id+"F0.wireOp",EDGE,"E4.7.1"),sQuery(id+"F0.wireOp",EDGE,"E4.8.0"),sQuery(id+"F0.wireOp",EDGE,"E4.8.1"),sQuery(id+"F0.wireOp",EDGE,"E4.9.0"),sQuery(id+"F0.wireOp",EDGE,"E4.9.1"),sQuery(id+"F0.wireOp",EDGE,"E4.10.0"),sQuery(id+"F0.wireOp",EDGE,"E4.10.1"),sQuery(id+"F0.wireOp",EDGE,"E4.11.0"),sQuery(id+"F0.wireOp",EDGE,"E4.11.1"),sQuery(id+"F0.wireOp",EDGE,"E4.12.0"),sQuery(id+"F0.wireOp",EDGE,"E4.12.1"),sQuery(id+"F0.wireOp",EDGE,"E4.13.0"),sQuery(id+"F0.wireOp",EDGE,"E4.13.1"),sQuery(id+"F0.wireOp",EDGE,"E4.14.0"),sQuery(id+"F0.wireOp",EDGE,"E4.14.1"),sQuery(id+"F0.wireOp",EDGE,"E4.15.0"),sQuery(id+"F0.wireOp",EDGE,"E4.15.1"),sQuery(id+"F0.wireOp",EDGE,"E4.16.0"),sQuery(id+"F0.wireOp",EDGE,"E4.16.1"),sQuery(id+"F0.wireOp",EDGE,"E4.17.0"),sQuery(id+"F0.wireOp",EDGE,"E4.17.1"),sQuery(id+"F0.wireOp",EDGE,"E4.18.0"),sQuery(id+"F0.wireOp",EDGE,"E4.18.1"),sQuery(id+"F0.wireOp",EDGE,"E4.19.0"),sQuery(id+"F0.wireOp",EDGE,"E4.19.1"),sQuery(id+"F0.wireOp",EDGE,"E4.20.0"),sQuery(id+"F0.wireOp",EDGE,"E4.20.1"),sQuery(id+"F0.wireOp",EDGE,"E4.21.0"),sQuery(id+"F0.wireOp",EDGE,"E4.21.1"),sQuery(id+"F0.wireOp",EDGE,"E4.22.0"),sQuery(id+"F0.wireOp",EDGE,"E4.22.1"),sQuery(id+"F0.wireOp",EDGE,"E4.23.0"),sQuery(id+"F0.wireOp",EDGE,"E4.23.1"),sQuery(id+"F0.wireOp",EDGE,"E4.24.0"),sQuery(id+"F0.wireOp",EDGE,"E4.24.1"),sQuery(id+"F0.wireOp",EDGE,"E4.25.0"),sQuery(id+"F0.wireOp",EDGE,"E4.25.1"),sQuery(id+"F0.wireOp",EDGE,"E4.26.0"),sQuery(id+"F0.wireOp",EDGE,"E4.26.1"),sQuery(id+"F0.wireOp",EDGE,"E4.27.0"),sQuery(id+"F0.wireOp",EDGE,"E4.27.1"),sQuery(id+"F0.wireOp",EDGE,"E4.28.0"),sQuery(id+"F0.wireOp",EDGE,"E4.28.1"),sQuery(id+"F0.wireOp",EDGE,"E4.29.0"),sQuery(id+"F0.wireOp",EDGE,"E4.29.1")])],"isStart":true}),makeQuery(id+"F5.opExtrude","SWEPT_FACE",FACE,{"disambiguationData":[OSD([sQuery(id+"F4.wireOp",EDGE,"E7.MirrorCS")])]})]});
            var Q26;
            Q26=makeQuery(id+"F5.boolean.opBoolean","INTERSECT",EDGE,{"derivedFrom":[makeQuery(id+"F1.opExtrude","CAP_FACE",FACE,{"disambiguationData":[OSD([sQuery(id+"F0.wireOp",EDGE,"E0"),sQuery(id+"F0.wireOp",EDGE,"E2"),sQuery(id+"F0.wireOp",EDGE,"E3"),sQuery(id+"F0.wireOp",EDGE,"E4.1.0"),sQuery(id+"F0.wireOp",EDGE,"E4.1.1"),sQuery(id+"F0.wireOp",EDGE,"E4.2.0"),sQuery(id+"F0.wireOp",EDGE,"E4.2.1"),sQuery(id+"F0.wireOp",EDGE,"E4.3.0"),sQuery(id+"F0.wireOp",EDGE,"E4.3.1"),sQuery(id+"F0.wireOp",EDGE,"E4.4.0"),sQuery(id+"F0.wireOp",EDGE,"E4.4.1"),sQuery(id+"F0.wireOp",EDGE,"E4.5.0"),sQuery(id+"F0.wireOp",EDGE,"E4.5.1"),sQuery(id+"F0.wireOp",EDGE,"E4.6.0"),sQuery(id+"F0.wireOp",EDGE,"E4.6.1"),sQuery(id+"F0.wireOp",EDGE,"E4.7.0"),sQuery(id+"F0.wireOp",EDGE,"E4.7.1"),sQuery(id+"F0.wireOp",EDGE,"E4.8.0"),sQuery(id+"F0.wireOp",EDGE,"E4.8.1"),sQuery(id+"F0.wireOp",EDGE,"E4.9.0"),sQuery(id+"F0.wireOp",EDGE,"E4.9.1"),sQuery(id+"F0.wireOp",EDGE,"E4.10.0"),sQuery(id+"F0.wireOp",EDGE,"E4.10.1"),sQuery(id+"F0.wireOp",EDGE,"E4.11.0"),sQuery(id+"F0.wireOp",EDGE,"E4.11.1"),sQuery(id+"F0.wireOp",EDGE,"E4.12.0"),sQuery(id+"F0.wireOp",EDGE,"E4.12.1"),sQuery(id+"F0.wireOp",EDGE,"E4.13.0"),sQuery(id+"F0.wireOp",EDGE,"E4.13.1"),sQuery(id+"F0.wireOp",EDGE,"E4.14.0"),sQuery(id+"F0.wireOp",EDGE,"E4.14.1"),sQuery(id+"F0.wireOp",EDGE,"E4.15.0"),sQuery(id+"F0.wireOp",EDGE,"E4.15.1"),sQuery(id+"F0.wireOp",EDGE,"E4.16.0"),sQuery(id+"F0.wireOp",EDGE,"E4.16.1"),sQuery(id+"F0.wireOp",EDGE,"E4.17.0"),sQuery(id+"F0.wireOp",EDGE,"E4.17.1"),sQuery(id+"F0.wireOp",EDGE,"E4.18.0"),sQuery(id+"F0.wireOp",EDGE,"E4.18.1"),sQuery(id+"F0.wireOp",EDGE,"E4.19.0"),sQuery(id+"F0.wireOp",EDGE,"E4.19.1"),sQuery(id+"F0.wireOp",EDGE,"E4.20.0"),sQuery(id+"F0.wireOp",EDGE,"E4.20.1"),sQuery(id+"F0.wireOp",EDGE,"E4.21.0"),sQuery(id+"F0.wireOp",EDGE,"E4.21.1"),sQuery(id+"F0.wireOp",EDGE,"E4.22.0"),sQuery(id+"F0.wireOp",EDGE,"E4.22.1"),sQuery(id+"F0.wireOp",EDGE,"E4.23.0"),sQuery(id+"F0.wireOp",EDGE,"E4.23.1"),sQuery(id+"F0.wireOp",EDGE,"E4.24.0"),sQuery(id+"F0.wireOp",EDGE,"E4.24.1"),sQuery(id+"F0.wireOp",EDGE,"E4.25.0"),sQuery(id+"F0.wireOp",EDGE,"E4.25.1"),sQuery(id+"F0.wireOp",EDGE,"E4.26.0"),sQuery(id+"F0.wireOp",EDGE,"E4.26.1"),sQuery(id+"F0.wireOp",EDGE,"E4.27.0"),sQuery(id+"F0.wireOp",EDGE,"E4.27.1"),sQuery(id+"F0.wireOp",EDGE,"E4.28.0"),sQuery(id+"F0.wireOp",EDGE,"E4.28.1"),sQuery(id+"F0.wireOp",EDGE,"E4.29.0"),sQuery(id+"F0.wireOp",EDGE,"E4.29.1")])],"isStart":true}),makeQuery(id+"F5.opExtrude","SWEPT_FACE",FACE,{"disambiguationData":[OSD([sQuery(id+"F4.wireOp",EDGE,"E29.MirrorCS")])]})]});
            var Q27;
            {var subQ0=sQuery(id+"F4.wireOp",EDGE,"E18.MirrorCS");Q27=makeQuery(id+"F5.boolean.opBoolean","INTERSECT",EDGE,{"derivedFrom":[makeQuery(id+"F1.opExtrude","CAP_FACE",FACE,{"disambiguationData":[OSD([sQuery(id+"F0.wireOp",EDGE,"E0"),sQuery(id+"F0.wireOp",EDGE,"E2"),sQuery(id+"F0.wireOp",EDGE,"E3"),sQuery(id+"F0.wireOp",EDGE,"E4.1.0"),sQuery(id+"F0.wireOp",EDGE,"E4.1.1"),sQuery(id+"F0.wireOp",EDGE,"E4.2.0"),sQuery(id+"F0.wireOp",EDGE,"E4.2.1"),sQuery(id+"F0.wireOp",EDGE,"E4.3.0"),sQuery(id+"F0.wireOp",EDGE,"E4.3.1"),sQuery(id+"F0.wireOp",EDGE,"E4.4.0"),sQuery(id+"F0.wireOp",EDGE,"E4.4.1"),sQuery(id+"F0.wireOp",EDGE,"E4.5.0"),sQuery(id+"F0.wireOp",EDGE,"E4.5.1"),sQuery(id+"F0.wireOp",EDGE,"E4.6.0"),sQuery(id+"F0.wireOp",EDGE,"E4.6.1"),sQuery(id+"F0.wireOp",EDGE,"E4.7.0"),sQuery(id+"F0.wireOp",EDGE,"E4.7.1"),sQuery(id+"F0.wireOp",EDGE,"E4.8.0"),sQuery(id+"F0.wireOp",EDGE,"E4.8.1"),sQuery(id+"F0.wireOp",EDGE,"E4.9.0"),sQuery(id+"F0.wireOp",EDGE,"E4.9.1"),sQuery(id+"F0.wireOp",EDGE,"E4.10.0"),sQuery(id+"F0.wireOp",EDGE,"E4.10.1"),sQuery(id+"F0.wireOp",EDGE,"E4.11.0"),sQuery(id+"F0.wireOp",EDGE,"E4.11.1"),sQuery(id+"F0.wireOp",EDGE,"E4.12.0"),sQuery(id+"F0.wireOp",EDGE,"E4.12.1"),sQuery(id+"F0.wireOp",EDGE,"E4.13.0"),sQuery(id+"F0.wireOp",EDGE,"E4.13.1"),sQuery(id+"F0.wireOp",EDGE,"E4.14.0"),sQuery(id+"F0.wireOp",EDGE,"E4.14.1"),sQuery(id+"F0.wireOp",EDGE,"E4.15.0"),sQuery(id+"F0.wireOp",EDGE,"E4.15.1"),sQuery(id+"F0.wireOp",EDGE,"E4.16.0"),sQuery(id+"F0.wireOp",EDGE,"E4.16.1"),sQuery(id+"F0.wireOp",EDGE,"E4.17.0"),sQuery(id+"F0.wireOp",EDGE,"E4.17.1"),sQuery(id+"F0.wireOp",EDGE,"E4.18.0"),sQuery(id+"F0.wireOp",EDGE,"E4.18.1"),sQuery(id+"F0.wireOp",EDGE,"E4.19.0"),sQuery(id+"F0.wireOp",EDGE,"E4.19.1"),sQuery(id+"F0.wireOp",EDGE,"E4.20.0"),sQuery(id+"F0.wireOp",EDGE,"E4.20.1"),sQuery(id+"F0.wireOp",EDGE,"E4.21.0"),sQuery(id+"F0.wireOp",EDGE,"E4.21.1"),sQuery(id+"F0.wireOp",EDGE,"E4.22.0"),sQuery(id+"F0.wireOp",EDGE,"E4.22.1"),sQuery(id+"F0.wireOp",EDGE,"E4.23.0"),sQuery(id+"F0.wireOp",EDGE,"E4.23.1"),sQuery(id+"F0.wireOp",EDGE,"E4.24.0"),sQuery(id+"F0.wireOp",EDGE,"E4.24.1"),sQuery(id+"F0.wireOp",EDGE,"E4.25.0"),sQuery(id+"F0.wireOp",EDGE,"E4.25.1"),sQuery(id+"F0.wireOp",EDGE,"E4.26.0"),sQuery(id+"F0.wireOp",EDGE,"E4.26.1"),sQuery(id+"F0.wireOp",EDGE,"E4.27.0"),sQuery(id+"F0.wireOp",EDGE,"E4.27.1"),sQuery(id+"F0.wireOp",EDGE,"E4.28.0"),sQuery(id+"F0.wireOp",EDGE,"E4.28.1"),sQuery(id+"F0.wireOp",EDGE,"E4.29.0"),sQuery(id+"F0.wireOp",EDGE,"E4.29.1")])],"isStart":true}),makeQuery(id+"F5.opExtrude","SWEPT_FACE",FACE,{"disambiguationData":[OSD([subQ0]),TDD([makeQuery(id+"F4.imprint","IMPRINT",EDGE,{"disambiguationData":[TD([[makeQuery(id+"F4.imprint","INTERSECT",VERTEX,{"derivedFrom":[sQuery(id+"F4.wireOp",EDGE,"E7.MirrorCS"),subQ0]}),-1.0]])],"derivedFrom":subQ0}),makeQuery(id+"F4.imprint","IMPRINT",EDGE,{"disambiguationData":[TD([[makeQuery(id+"F4.imprint","INTERSECT",VERTEX,{"derivedFrom":[subQ0,sQuery(id+"F4.wireOp",EDGE,"E29.MirrorCS")]}),1.0]])],"derivedFrom":subQ0})])]})]});}
            var Q28;
            {var subQ0=sQuery(id+"F4.wireOp",EDGE,"E16");Q28=makeQuery(id+"F5.boolean.opBoolean","INTERSECT",EDGE,{"derivedFrom":[makeQuery(id+"F1.opExtrude","CAP_FACE",FACE,{"disambiguationData":[OSD([sQuery(id+"F0.wireOp",EDGE,"E0"),sQuery(id+"F0.wireOp",EDGE,"E2"),sQuery(id+"F0.wireOp",EDGE,"E3"),sQuery(id+"F0.wireOp",EDGE,"E4.1.0"),sQuery(id+"F0.wireOp",EDGE,"E4.1.1"),sQuery(id+"F0.wireOp",EDGE,"E4.2.0"),sQuery(id+"F0.wireOp",EDGE,"E4.2.1"),sQuery(id+"F0.wireOp",EDGE,"E4.3.0"),sQuery(id+"F0.wireOp",EDGE,"E4.3.1"),sQuery(id+"F0.wireOp",EDGE,"E4.4.0"),sQuery(id+"F0.wireOp",EDGE,"E4.4.1"),sQuery(id+"F0.wireOp",EDGE,"E4.5.0"),sQuery(id+"F0.wireOp",EDGE,"E4.5.1"),sQuery(id+"F0.wireOp",EDGE,"E4.6.0"),sQuery(id+"F0.wireOp",EDGE,"E4.6.1"),sQuery(id+"F0.wireOp",EDGE,"E4.7.0"),sQuery(id+"F0.wireOp",EDGE,"E4.7.1"),sQuery(id+"F0.wireOp",EDGE,"E4.8.0"),sQuery(id+"F0.wireOp",EDGE,"E4.8.1"),sQuery(id+"F0.wireOp",EDGE,"E4.9.0"),sQuery(id+"F0.wireOp",EDGE,"E4.9.1"),sQuery(id+"F0.wireOp",EDGE,"E4.10.0"),sQuery(id+"F0.wireOp",EDGE,"E4.10.1"),sQuery(id+"F0.wireOp",EDGE,"E4.11.0"),sQuery(id+"F0.wireOp",EDGE,"E4.11.1"),sQuery(id+"F0.wireOp",EDGE,"E4.12.0"),sQuery(id+"F0.wireOp",EDGE,"E4.12.1"),sQuery(id+"F0.wireOp",EDGE,"E4.13.0"),sQuery(id+"F0.wireOp",EDGE,"E4.13.1"),sQuery(id+"F0.wireOp",EDGE,"E4.14.0"),sQuery(id+"F0.wireOp",EDGE,"E4.14.1"),sQuery(id+"F0.wireOp",EDGE,"E4.15.0"),sQuery(id+"F0.wireOp",EDGE,"E4.15.1"),sQuery(id+"F0.wireOp",EDGE,"E4.16.0"),sQuery(id+"F0.wireOp",EDGE,"E4.16.1"),sQuery(id+"F0.wireOp",EDGE,"E4.17.0"),sQuery(id+"F0.wireOp",EDGE,"E4.17.1"),sQuery(id+"F0.wireOp",EDGE,"E4.18.0"),sQuery(id+"F0.wireOp",EDGE,"E4.18.1"),sQuery(id+"F0.wireOp",EDGE,"E4.19.0"),sQuery(id+"F0.wireOp",EDGE,"E4.19.1"),sQuery(id+"F0.wireOp",EDGE,"E4.20.0"),sQuery(id+"F0.wireOp",EDGE,"E4.20.1"),sQuery(id+"F0.wireOp",EDGE,"E4.21.0"),sQuery(id+"F0.wireOp",EDGE,"E4.21.1"),sQuery(id+"F0.wireOp",EDGE,"E4.22.0"),sQuery(id+"F0.wireOp",EDGE,"E4.22.1"),sQuery(id+"F0.wireOp",EDGE,"E4.23.0"),sQuery(id+"F0.wireOp",EDGE,"E4.23.1"),sQuery(id+"F0.wireOp",EDGE,"E4.24.0"),sQuery(id+"F0.wireOp",EDGE,"E4.24.1"),sQuery(id+"F0.wireOp",EDGE,"E4.25.0"),sQuery(id+"F0.wireOp",EDGE,"E4.25.1"),sQuery(id+"F0.wireOp",EDGE,"E4.26.0"),sQuery(id+"F0.wireOp",EDGE,"E4.26.1"),sQuery(id+"F0.wireOp",EDGE,"E4.27.0"),sQuery(id+"F0.wireOp",EDGE,"E4.27.1"),sQuery(id+"F0.wireOp",EDGE,"E4.28.0"),sQuery(id+"F0.wireOp",EDGE,"E4.28.1"),sQuery(id+"F0.wireOp",EDGE,"E4.29.0"),sQuery(id+"F0.wireOp",EDGE,"E4.29.1")])],"isStart":true}),makeQuery(id+"F5.opExtrude","SWEPT_FACE",FACE,{"disambiguationData":[OSD([subQ0]),TDD([makeQuery(id+"F4.imprint","IMPRINT",EDGE,{"disambiguationData":[TD([[makeQuery(id+"F4.imprint","INTERSECT",VERTEX,{"derivedFrom":[sQuery(id+"F4.wireOp",EDGE,"E5"),subQ0]}),-1.0]])],"derivedFrom":subQ0}),makeQuery(id+"F4.imprint","IMPRINT",EDGE,{"disambiguationData":[TD([[makeQuery(id+"F4.imprint","INTERSECT",VERTEX,{"derivedFrom":[subQ0,sQuery(id+"F4.wireOp",EDGE,"E25")]}),1.0]])],"derivedFrom":subQ0})])]})]});}
            var Q29;
            Q29=makeQuery(id+"F5.boolean.opBoolean","INTERSECT",EDGE,{"derivedFrom":[makeQuery(id+"F1.opExtrude","CAP_FACE",FACE,{"disambiguationData":[OSD([sQuery(id+"F0.wireOp",EDGE,"E0"),sQuery(id+"F0.wireOp",EDGE,"E2"),sQuery(id+"F0.wireOp",EDGE,"E3"),sQuery(id+"F0.wireOp",EDGE,"E4.1.0"),sQuery(id+"F0.wireOp",EDGE,"E4.1.1"),sQuery(id+"F0.wireOp",EDGE,"E4.2.0"),sQuery(id+"F0.wireOp",EDGE,"E4.2.1"),sQuery(id+"F0.wireOp",EDGE,"E4.3.0"),sQuery(id+"F0.wireOp",EDGE,"E4.3.1"),sQuery(id+"F0.wireOp",EDGE,"E4.4.0"),sQuery(id+"F0.wireOp",EDGE,"E4.4.1"),sQuery(id+"F0.wireOp",EDGE,"E4.5.0"),sQuery(id+"F0.wireOp",EDGE,"E4.5.1"),sQuery(id+"F0.wireOp",EDGE,"E4.6.0"),sQuery(id+"F0.wireOp",EDGE,"E4.6.1"),sQuery(id+"F0.wireOp",EDGE,"E4.7.0"),sQuery(id+"F0.wireOp",EDGE,"E4.7.1"),sQuery(id+"F0.wireOp",EDGE,"E4.8.0"),sQuery(id+"F0.wireOp",EDGE,"E4.8.1"),sQuery(id+"F0.wireOp",EDGE,"E4.9.0"),sQuery(id+"F0.wireOp",EDGE,"E4.9.1"),sQuery(id+"F0.wireOp",EDGE,"E4.10.0"),sQuery(id+"F0.wireOp",EDGE,"E4.10.1"),sQuery(id+"F0.wireOp",EDGE,"E4.11.0"),sQuery(id+"F0.wireOp",EDGE,"E4.11.1"),sQuery(id+"F0.wireOp",EDGE,"E4.12.0"),sQuery(id+"F0.wireOp",EDGE,"E4.12.1"),sQuery(id+"F0.wireOp",EDGE,"E4.13.0"),sQuery(id+"F0.wireOp",EDGE,"E4.13.1"),sQuery(id+"F0.wireOp",EDGE,"E4.14.0"),sQuery(id+"F0.wireOp",EDGE,"E4.14.1"),sQuery(id+"F0.wireOp",EDGE,"E4.15.0"),sQuery(id+"F0.wireOp",EDGE,"E4.15.1"),sQuery(id+"F0.wireOp",EDGE,"E4.16.0"),sQuery(id+"F0.wireOp",EDGE,"E4.16.1"),sQuery(id+"F0.wireOp",EDGE,"E4.17.0"),sQuery(id+"F0.wireOp",EDGE,"E4.17.1"),sQuery(id+"F0.wireOp",EDGE,"E4.18.0"),sQuery(id+"F0.wireOp",EDGE,"E4.18.1"),sQuery(id+"F0.wireOp",EDGE,"E4.19.0"),sQuery(id+"F0.wireOp",EDGE,"E4.19.1"),sQuery(id+"F0.wireOp",EDGE,"E4.20.0"),sQuery(id+"F0.wireOp",EDGE,"E4.20.1"),sQuery(id+"F0.wireOp",EDGE,"E4.21.0"),sQuery(id+"F0.wireOp",EDGE,"E4.21.1"),sQuery(id+"F0.wireOp",EDGE,"E4.22.0"),sQuery(id+"F0.wireOp",EDGE,"E4.22.1"),sQuery(id+"F0.wireOp",EDGE,"E4.23.0"),sQuery(id+"F0.wireOp",EDGE,"E4.23.1"),sQuery(id+"F0.wireOp",EDGE,"E4.24.0"),sQuery(id+"F0.wireOp",EDGE,"E4.24.1"),sQuery(id+"F0.wireOp",EDGE,"E4.25.0"),sQuery(id+"F0.wireOp",EDGE,"E4.25.1"),sQuery(id+"F0.wireOp",EDGE,"E4.26.0"),sQuery(id+"F0.wireOp",EDGE,"E4.26.1"),sQuery(id+"F0.wireOp",EDGE,"E4.27.0"),sQuery(id+"F0.wireOp",EDGE,"E4.27.1"),sQuery(id+"F0.wireOp",EDGE,"E4.28.0"),sQuery(id+"F0.wireOp",EDGE,"E4.28.1"),sQuery(id+"F0.wireOp",EDGE,"E4.29.0"),sQuery(id+"F0.wireOp",EDGE,"E4.29.1")])],"isStart":true}),makeQuery(id+"F5.opExtrude","SWEPT_FACE",FACE,{"disambiguationData":[OSD([sQuery(id+"F4.wireOp",EDGE,"E5")])]})]});
            var Q30;
            {var subQ0=sQuery(id+"F4.wireOp",EDGE,"E15");Q30=makeQuery(id+"F5.boolean.opBoolean","INTERSECT",EDGE,{"derivedFrom":[makeQuery(id+"F1.opExtrude","CAP_FACE",FACE,{"disambiguationData":[OSD([sQuery(id+"F0.wireOp",EDGE,"E0"),sQuery(id+"F0.wireOp",EDGE,"E2"),sQuery(id+"F0.wireOp",EDGE,"E3"),sQuery(id+"F0.wireOp",EDGE,"E4.1.0"),sQuery(id+"F0.wireOp",EDGE,"E4.1.1"),sQuery(id+"F0.wireOp",EDGE,"E4.2.0"),sQuery(id+"F0.wireOp",EDGE,"E4.2.1"),sQuery(id+"F0.wireOp",EDGE,"E4.3.0"),sQuery(id+"F0.wireOp",EDGE,"E4.3.1"),sQuery(id+"F0.wireOp",EDGE,"E4.4.0"),sQuery(id+"F0.wireOp",EDGE,"E4.4.1"),sQuery(id+"F0.wireOp",EDGE,"E4.5.0"),sQuery(id+"F0.wireOp",EDGE,"E4.5.1"),sQuery(id+"F0.wireOp",EDGE,"E4.6.0"),sQuery(id+"F0.wireOp",EDGE,"E4.6.1"),sQuery(id+"F0.wireOp",EDGE,"E4.7.0"),sQuery(id+"F0.wireOp",EDGE,"E4.7.1"),sQuery(id+"F0.wireOp",EDGE,"E4.8.0"),sQuery(id+"F0.wireOp",EDGE,"E4.8.1"),sQuery(id+"F0.wireOp",EDGE,"E4.9.0"),sQuery(id+"F0.wireOp",EDGE,"E4.9.1"),sQuery(id+"F0.wireOp",EDGE,"E4.10.0"),sQuery(id+"F0.wireOp",EDGE,"E4.10.1"),sQuery(id+"F0.wireOp",EDGE,"E4.11.0"),sQuery(id+"F0.wireOp",EDGE,"E4.11.1"),sQuery(id+"F0.wireOp",EDGE,"E4.12.0"),sQuery(id+"F0.wireOp",EDGE,"E4.12.1"),sQuery(id+"F0.wireOp",EDGE,"E4.13.0"),sQuery(id+"F0.wireOp",EDGE,"E4.13.1"),sQuery(id+"F0.wireOp",EDGE,"E4.14.0"),sQuery(id+"F0.wireOp",EDGE,"E4.14.1"),sQuery(id+"F0.wireOp",EDGE,"E4.15.0"),sQuery(id+"F0.wireOp",EDGE,"E4.15.1"),sQuery(id+"F0.wireOp",EDGE,"E4.16.0"),sQuery(id+"F0.wireOp",EDGE,"E4.16.1"),sQuery(id+"F0.wireOp",EDGE,"E4.17.0"),sQuery(id+"F0.wireOp",EDGE,"E4.17.1"),sQuery(id+"F0.wireOp",EDGE,"E4.18.0"),sQuery(id+"F0.wireOp",EDGE,"E4.18.1"),sQuery(id+"F0.wireOp",EDGE,"E4.19.0"),sQuery(id+"F0.wireOp",EDGE,"E4.19.1"),sQuery(id+"F0.wireOp",EDGE,"E4.20.0"),sQuery(id+"F0.wireOp",EDGE,"E4.20.1"),sQuery(id+"F0.wireOp",EDGE,"E4.21.0"),sQuery(id+"F0.wireOp",EDGE,"E4.21.1"),sQuery(id+"F0.wireOp",EDGE,"E4.22.0"),sQuery(id+"F0.wireOp",EDGE,"E4.22.1"),sQuery(id+"F0.wireOp",EDGE,"E4.23.0"),sQuery(id+"F0.wireOp",EDGE,"E4.23.1"),sQuery(id+"F0.wireOp",EDGE,"E4.24.0"),sQuery(id+"F0.wireOp",EDGE,"E4.24.1"),sQuery(id+"F0.wireOp",EDGE,"E4.25.0"),sQuery(id+"F0.wireOp",EDGE,"E4.25.1"),sQuery(id+"F0.wireOp",EDGE,"E4.26.0"),sQuery(id+"F0.wireOp",EDGE,"E4.26.1"),sQuery(id+"F0.wireOp",EDGE,"E4.27.0"),sQuery(id+"F0.wireOp",EDGE,"E4.27.1"),sQuery(id+"F0.wireOp",EDGE,"E4.28.0"),sQuery(id+"F0.wireOp",EDGE,"E4.28.1"),sQuery(id+"F0.wireOp",EDGE,"E4.29.0"),sQuery(id+"F0.wireOp",EDGE,"E4.29.1")])],"isStart":true}),makeQuery(id+"F5.opExtrude","SWEPT_FACE",FACE,{"disambiguationData":[OSD([subQ0]),TDD([makeQuery(id+"F4.imprint","IMPRINT",EDGE,{"disambiguationData":[TD([[makeQuery(id+"F4.imprint","INTERSECT",VERTEX,{"derivedFrom":[sQuery(id+"F4.wireOp",EDGE,"E5"),subQ0]}),-1.0]])],"derivedFrom":subQ0}),makeQuery(id+"F4.imprint","IMPRINT",EDGE,{"disambiguationData":[TD([[makeQuery(id+"F4.imprint","INTERSECT",VERTEX,{"derivedFrom":[subQ0,sQuery(id+"F4.wireOp",EDGE,"E25")]}),1.0]])],"derivedFrom":subQ0})])]})]});}
            var Q31;
            Q31=makeQuery(id+"F5.boolean.opBoolean","INTERSECT",EDGE,{"derivedFrom":[makeQuery(id+"F1.opExtrude","CAP_FACE",FACE,{"disambiguationData":[OSD([sQuery(id+"F0.wireOp",EDGE,"E0"),sQuery(id+"F0.wireOp",EDGE,"E2"),sQuery(id+"F0.wireOp",EDGE,"E3"),sQuery(id+"F0.wireOp",EDGE,"E4.1.0"),sQuery(id+"F0.wireOp",EDGE,"E4.1.1"),sQuery(id+"F0.wireOp",EDGE,"E4.2.0"),sQuery(id+"F0.wireOp",EDGE,"E4.2.1"),sQuery(id+"F0.wireOp",EDGE,"E4.3.0"),sQuery(id+"F0.wireOp",EDGE,"E4.3.1"),sQuery(id+"F0.wireOp",EDGE,"E4.4.0"),sQuery(id+"F0.wireOp",EDGE,"E4.4.1"),sQuery(id+"F0.wireOp",EDGE,"E4.5.0"),sQuery(id+"F0.wireOp",EDGE,"E4.5.1"),sQuery(id+"F0.wireOp",EDGE,"E4.6.0"),sQuery(id+"F0.wireOp",EDGE,"E4.6.1"),sQuery(id+"F0.wireOp",EDGE,"E4.7.0"),sQuery(id+"F0.wireOp",EDGE,"E4.7.1"),sQuery(id+"F0.wireOp",EDGE,"E4.8.0"),sQuery(id+"F0.wireOp",EDGE,"E4.8.1"),sQuery(id+"F0.wireOp",EDGE,"E4.9.0"),sQuery(id+"F0.wireOp",EDGE,"E4.9.1"),sQuery(id+"F0.wireOp",EDGE,"E4.10.0"),sQuery(id+"F0.wireOp",EDGE,"E4.10.1"),sQuery(id+"F0.wireOp",EDGE,"E4.11.0"),sQuery(id+"F0.wireOp",EDGE,"E4.11.1"),sQuery(id+"F0.wireOp",EDGE,"E4.12.0"),sQuery(id+"F0.wireOp",EDGE,"E4.12.1"),sQuery(id+"F0.wireOp",EDGE,"E4.13.0"),sQuery(id+"F0.wireOp",EDGE,"E4.13.1"),sQuery(id+"F0.wireOp",EDGE,"E4.14.0"),sQuery(id+"F0.wireOp",EDGE,"E4.14.1"),sQuery(id+"F0.wireOp",EDGE,"E4.15.0"),sQuery(id+"F0.wireOp",EDGE,"E4.15.1"),sQuery(id+"F0.wireOp",EDGE,"E4.16.0"),sQuery(id+"F0.wireOp",EDGE,"E4.16.1"),sQuery(id+"F0.wireOp",EDGE,"E4.17.0"),sQuery(id+"F0.wireOp",EDGE,"E4.17.1"),sQuery(id+"F0.wireOp",EDGE,"E4.18.0"),sQuery(id+"F0.wireOp",EDGE,"E4.18.1"),sQuery(id+"F0.wireOp",EDGE,"E4.19.0"),sQuery(id+"F0.wireOp",EDGE,"E4.19.1"),sQuery(id+"F0.wireOp",EDGE,"E4.20.0"),sQuery(id+"F0.wireOp",EDGE,"E4.20.1"),sQuery(id+"F0.wireOp",EDGE,"E4.21.0"),sQuery(id+"F0.wireOp",EDGE,"E4.21.1"),sQuery(id+"F0.wireOp",EDGE,"E4.22.0"),sQuery(id+"F0.wireOp",EDGE,"E4.22.1"),sQuery(id+"F0.wireOp",EDGE,"E4.23.0"),sQuery(id+"F0.wireOp",EDGE,"E4.23.1"),sQuery(id+"F0.wireOp",EDGE,"E4.24.0"),sQuery(id+"F0.wireOp",EDGE,"E4.24.1"),sQuery(id+"F0.wireOp",EDGE,"E4.25.0"),sQuery(id+"F0.wireOp",EDGE,"E4.25.1"),sQuery(id+"F0.wireOp",EDGE,"E4.26.0"),sQuery(id+"F0.wireOp",EDGE,"E4.26.1"),sQuery(id+"F0.wireOp",EDGE,"E4.27.0"),sQuery(id+"F0.wireOp",EDGE,"E4.27.1"),sQuery(id+"F0.wireOp",EDGE,"E4.28.0"),sQuery(id+"F0.wireOp",EDGE,"E4.28.1"),sQuery(id+"F0.wireOp",EDGE,"E4.29.0"),sQuery(id+"F0.wireOp",EDGE,"E4.29.1")])],"isStart":true}),makeQuery(id+"F5.opExtrude","SWEPT_FACE",FACE,{"disambiguationData":[OSD([sQuery(id+"F4.wireOp",EDGE,"E25")])]})]});
            chamfer(context, id + "F8", {"entities" : qUnion([Q0, Q1, Q2, Q3, Q4, Q5, Q6, Q7, Q8, Q9, Q10, Q11, Q12, Q13, Q14, Q15, Q16, Q17, Q18, Q19, Q20, Q21, Q22, Q23, Q24, Q25, Q26, Q27, Q28, Q29, Q30, Q31]), "width" : 1.6 * mm, "tangentPropagation" : true});
        }
        {
            var Q0;
            Q0=makeQuery(id+"F5.boolean.opBoolean","COPY",EDGE,{"derivedFrom":makeQuery(id+"F5.opExtrude","CAP_EDGE",EDGE,{"disambiguationData":[OSD([sQuery(id+"F4.wireOp",EDGE,"E39.bottom")])],"isStart":true})});
            var Q1;
            Q1=makeQuery(id+"F5.boolean.opBoolean","COPY",EDGE,{"derivedFrom":makeQuery(id+"F5.opExtrude","CAP_EDGE",EDGE,{"disambiguationData":[OSD([sQuery(id+"F4.wireOp",EDGE,"E39.left")])],"isStart":true})});
            var Q2;
            Q2=makeQuery(id+"F5.boolean.opBoolean","COPY",EDGE,{"derivedFrom":makeQuery(id+"F5.opExtrude","CAP_EDGE",EDGE,{"disambiguationData":[OSD([sQuery(id+"F4.wireOp",EDGE,"E39.top")])],"isStart":true})});
            var Q3;
            Q3=makeQuery(id+"F5.boolean.opBoolean","COPY",EDGE,{"derivedFrom":makeQuery(id+"F5.opExtrude","CAP_EDGE",EDGE,{"disambiguationData":[OSD([sQuery(id+"F4.wireOp",EDGE,"E39.right")])],"isStart":true})});
            var Q4;
            Q4=makeQuery(id+"F5.boolean.opBoolean","COPY",EDGE,{"derivedFrom":makeQuery(id+"F5.opExtrude","CAP_EDGE",EDGE,{"disambiguationData":[OSD([sQuery(id+"F4.wireOp",EDGE,"E40.bottom")])],"isStart":true})});
            var Q5;
            Q5=makeQuery(id+"F5.boolean.opBoolean","COPY",EDGE,{"derivedFrom":makeQuery(id+"F5.opExtrude","CAP_EDGE",EDGE,{"disambiguationData":[OSD([sQuery(id+"F4.wireOp",EDGE,"E40.top")])],"isStart":true})});
            var Q6;
            Q6=makeQuery(id+"F5.boolean.opBoolean","COPY",EDGE,{"derivedFrom":makeQuery(id+"F5.opExtrude","CAP_EDGE",EDGE,{"disambiguationData":[OSD([sQuery(id+"F4.wireOp",EDGE,"E40.right")])],"isStart":true})});
            var Q7;
            Q7=makeQuery(id+"F5.boolean.opBoolean","COPY",EDGE,{"derivedFrom":makeQuery(id+"F5.opExtrude","CAP_EDGE",EDGE,{"disambiguationData":[OSD([sQuery(id+"F4.wireOp",EDGE,"E40.left")])],"isStart":true})});
            var Q8;
            Q8=makeQuery(id+"F5.boolean.opBoolean","INTERSECT",EDGE,{"derivedFrom":[makeQuery(id+"F1.opExtrude","CAP_FACE",FACE,{"disambiguationData":[OSD([sQuery(id+"F0.wireOp",EDGE,"E0"),sQuery(id+"F0.wireOp",EDGE,"E2"),sQuery(id+"F0.wireOp",EDGE,"E3"),sQuery(id+"F0.wireOp",EDGE,"E4.1.0"),sQuery(id+"F0.wireOp",EDGE,"E4.1.1"),sQuery(id+"F0.wireOp",EDGE,"E4.2.0"),sQuery(id+"F0.wireOp",EDGE,"E4.2.1"),sQuery(id+"F0.wireOp",EDGE,"E4.3.0"),sQuery(id+"F0.wireOp",EDGE,"E4.3.1"),sQuery(id+"F0.wireOp",EDGE,"E4.4.0"),sQuery(id+"F0.wireOp",EDGE,"E4.4.1"),sQuery(id+"F0.wireOp",EDGE,"E4.5.0"),sQuery(id+"F0.wireOp",EDGE,"E4.5.1"),sQuery(id+"F0.wireOp",EDGE,"E4.6.0"),sQuery(id+"F0.wireOp",EDGE,"E4.6.1"),sQuery(id+"F0.wireOp",EDGE,"E4.7.0"),sQuery(id+"F0.wireOp",EDGE,"E4.7.1"),sQuery(id+"F0.wireOp",EDGE,"E4.8.0"),sQuery(id+"F0.wireOp",EDGE,"E4.8.1"),sQuery(id+"F0.wireOp",EDGE,"E4.9.0"),sQuery(id+"F0.wireOp",EDGE,"E4.9.1"),sQuery(id+"F0.wireOp",EDGE,"E4.10.0"),sQuery(id+"F0.wireOp",EDGE,"E4.10.1"),sQuery(id+"F0.wireOp",EDGE,"E4.11.0"),sQuery(id+"F0.wireOp",EDGE,"E4.11.1"),sQuery(id+"F0.wireOp",EDGE,"E4.12.0"),sQuery(id+"F0.wireOp",EDGE,"E4.12.1"),sQuery(id+"F0.wireOp",EDGE,"E4.13.0"),sQuery(id+"F0.wireOp",EDGE,"E4.13.1"),sQuery(id+"F0.wireOp",EDGE,"E4.14.0"),sQuery(id+"F0.wireOp",EDGE,"E4.14.1"),sQuery(id+"F0.wireOp",EDGE,"E4.15.0"),sQuery(id+"F0.wireOp",EDGE,"E4.15.1"),sQuery(id+"F0.wireOp",EDGE,"E4.16.0"),sQuery(id+"F0.wireOp",EDGE,"E4.16.1"),sQuery(id+"F0.wireOp",EDGE,"E4.17.0"),sQuery(id+"F0.wireOp",EDGE,"E4.17.1"),sQuery(id+"F0.wireOp",EDGE,"E4.18.0"),sQuery(id+"F0.wireOp",EDGE,"E4.18.1"),sQuery(id+"F0.wireOp",EDGE,"E4.19.0"),sQuery(id+"F0.wireOp",EDGE,"E4.19.1"),sQuery(id+"F0.wireOp",EDGE,"E4.20.0"),sQuery(id+"F0.wireOp",EDGE,"E4.20.1"),sQuery(id+"F0.wireOp",EDGE,"E4.21.0"),sQuery(id+"F0.wireOp",EDGE,"E4.21.1"),sQuery(id+"F0.wireOp",EDGE,"E4.22.0"),sQuery(id+"F0.wireOp",EDGE,"E4.22.1"),sQuery(id+"F0.wireOp",EDGE,"E4.23.0"),sQuery(id+"F0.wireOp",EDGE,"E4.23.1"),sQuery(id+"F0.wireOp",EDGE,"E4.24.0"),sQuery(id+"F0.wireOp",EDGE,"E4.24.1"),sQuery(id+"F0.wireOp",EDGE,"E4.25.0"),sQuery(id+"F0.wireOp",EDGE,"E4.25.1"),sQuery(id+"F0.wireOp",EDGE,"E4.26.0"),sQuery(id+"F0.wireOp",EDGE,"E4.26.1"),sQuery(id+"F0.wireOp",EDGE,"E4.27.0"),sQuery(id+"F0.wireOp",EDGE,"E4.27.1"),sQuery(id+"F0.wireOp",EDGE,"E4.28.0"),sQuery(id+"F0.wireOp",EDGE,"E4.28.1"),sQuery(id+"F0.wireOp",EDGE,"E4.29.0"),sQuery(id+"F0.wireOp",EDGE,"E4.29.1")])],"isStart":true}),makeQuery(id+"F5.opExtrude","SWEPT_FACE",FACE,{"disambiguationData":[OSD([sQuery(id+"F4.wireOp",EDGE,"E40.left")])]})]});
            var Q9;
            Q9=makeQuery(id+"F5.boolean.opBoolean","INTERSECT",EDGE,{"derivedFrom":[makeQuery(id+"F1.opExtrude","CAP_FACE",FACE,{"disambiguationData":[OSD([sQuery(id+"F0.wireOp",EDGE,"E0"),sQuery(id+"F0.wireOp",EDGE,"E2"),sQuery(id+"F0.wireOp",EDGE,"E3"),sQuery(id+"F0.wireOp",EDGE,"E4.1.0"),sQuery(id+"F0.wireOp",EDGE,"E4.1.1"),sQuery(id+"F0.wireOp",EDGE,"E4.2.0"),sQuery(id+"F0.wireOp",EDGE,"E4.2.1"),sQuery(id+"F0.wireOp",EDGE,"E4.3.0"),sQuery(id+"F0.wireOp",EDGE,"E4.3.1"),sQuery(id+"F0.wireOp",EDGE,"E4.4.0"),sQuery(id+"F0.wireOp",EDGE,"E4.4.1"),sQuery(id+"F0.wireOp",EDGE,"E4.5.0"),sQuery(id+"F0.wireOp",EDGE,"E4.5.1"),sQuery(id+"F0.wireOp",EDGE,"E4.6.0"),sQuery(id+"F0.wireOp",EDGE,"E4.6.1"),sQuery(id+"F0.wireOp",EDGE,"E4.7.0"),sQuery(id+"F0.wireOp",EDGE,"E4.7.1"),sQuery(id+"F0.wireOp",EDGE,"E4.8.0"),sQuery(id+"F0.wireOp",EDGE,"E4.8.1"),sQuery(id+"F0.wireOp",EDGE,"E4.9.0"),sQuery(id+"F0.wireOp",EDGE,"E4.9.1"),sQuery(id+"F0.wireOp",EDGE,"E4.10.0"),sQuery(id+"F0.wireOp",EDGE,"E4.10.1"),sQuery(id+"F0.wireOp",EDGE,"E4.11.0"),sQuery(id+"F0.wireOp",EDGE,"E4.11.1"),sQuery(id+"F0.wireOp",EDGE,"E4.12.0"),sQuery(id+"F0.wireOp",EDGE,"E4.12.1"),sQuery(id+"F0.wireOp",EDGE,"E4.13.0"),sQuery(id+"F0.wireOp",EDGE,"E4.13.1"),sQuery(id+"F0.wireOp",EDGE,"E4.14.0"),sQuery(id+"F0.wireOp",EDGE,"E4.14.1"),sQuery(id+"F0.wireOp",EDGE,"E4.15.0"),sQuery(id+"F0.wireOp",EDGE,"E4.15.1"),sQuery(id+"F0.wireOp",EDGE,"E4.16.0"),sQuery(id+"F0.wireOp",EDGE,"E4.16.1"),sQuery(id+"F0.wireOp",EDGE,"E4.17.0"),sQuery(id+"F0.wireOp",EDGE,"E4.17.1"),sQuery(id+"F0.wireOp",EDGE,"E4.18.0"),sQuery(id+"F0.wireOp",EDGE,"E4.18.1"),sQuery(id+"F0.wireOp",EDGE,"E4.19.0"),sQuery(id+"F0.wireOp",EDGE,"E4.19.1"),sQuery(id+"F0.wireOp",EDGE,"E4.20.0"),sQuery(id+"F0.wireOp",EDGE,"E4.20.1"),sQuery(id+"F0.wireOp",EDGE,"E4.21.0"),sQuery(id+"F0.wireOp",EDGE,"E4.21.1"),sQuery(id+"F0.wireOp",EDGE,"E4.22.0"),sQuery(id+"F0.wireOp",EDGE,"E4.22.1"),sQuery(id+"F0.wireOp",EDGE,"E4.23.0"),sQuery(id+"F0.wireOp",EDGE,"E4.23.1"),sQuery(id+"F0.wireOp",EDGE,"E4.24.0"),sQuery(id+"F0.wireOp",EDGE,"E4.24.1"),sQuery(id+"F0.wireOp",EDGE,"E4.25.0"),sQuery(id+"F0.wireOp",EDGE,"E4.25.1"),sQuery(id+"F0.wireOp",EDGE,"E4.26.0"),sQuery(id+"F0.wireOp",EDGE,"E4.26.1"),sQuery(id+"F0.wireOp",EDGE,"E4.27.0"),sQuery(id+"F0.wireOp",EDGE,"E4.27.1"),sQuery(id+"F0.wireOp",EDGE,"E4.28.0"),sQuery(id+"F0.wireOp",EDGE,"E4.28.1"),sQuery(id+"F0.wireOp",EDGE,"E4.29.0"),sQuery(id+"F0.wireOp",EDGE,"E4.29.1")])],"isStart":true}),makeQuery(id+"F5.opExtrude","SWEPT_FACE",FACE,{"disambiguationData":[OSD([sQuery(id+"F4.wireOp",EDGE,"E40.bottom")])]})]});
            var Q10;
            Q10=makeQuery(id+"F5.boolean.opBoolean","INTERSECT",EDGE,{"derivedFrom":[makeQuery(id+"F1.opExtrude","CAP_FACE",FACE,{"disambiguationData":[OSD([sQuery(id+"F0.wireOp",EDGE,"E0"),sQuery(id+"F0.wireOp",EDGE,"E2"),sQuery(id+"F0.wireOp",EDGE,"E3"),sQuery(id+"F0.wireOp",EDGE,"E4.1.0"),sQuery(id+"F0.wireOp",EDGE,"E4.1.1"),sQuery(id+"F0.wireOp",EDGE,"E4.2.0"),sQuery(id+"F0.wireOp",EDGE,"E4.2.1"),sQuery(id+"F0.wireOp",EDGE,"E4.3.0"),sQuery(id+"F0.wireOp",EDGE,"E4.3.1"),sQuery(id+"F0.wireOp",EDGE,"E4.4.0"),sQuery(id+"F0.wireOp",EDGE,"E4.4.1"),sQuery(id+"F0.wireOp",EDGE,"E4.5.0"),sQuery(id+"F0.wireOp",EDGE,"E4.5.1"),sQuery(id+"F0.wireOp",EDGE,"E4.6.0"),sQuery(id+"F0.wireOp",EDGE,"E4.6.1"),sQuery(id+"F0.wireOp",EDGE,"E4.7.0"),sQuery(id+"F0.wireOp",EDGE,"E4.7.1"),sQuery(id+"F0.wireOp",EDGE,"E4.8.0"),sQuery(id+"F0.wireOp",EDGE,"E4.8.1"),sQuery(id+"F0.wireOp",EDGE,"E4.9.0"),sQuery(id+"F0.wireOp",EDGE,"E4.9.1"),sQuery(id+"F0.wireOp",EDGE,"E4.10.0"),sQuery(id+"F0.wireOp",EDGE,"E4.10.1"),sQuery(id+"F0.wireOp",EDGE,"E4.11.0"),sQuery(id+"F0.wireOp",EDGE,"E4.11.1"),sQuery(id+"F0.wireOp",EDGE,"E4.12.0"),sQuery(id+"F0.wireOp",EDGE,"E4.12.1"),sQuery(id+"F0.wireOp",EDGE,"E4.13.0"),sQuery(id+"F0.wireOp",EDGE,"E4.13.1"),sQuery(id+"F0.wireOp",EDGE,"E4.14.0"),sQuery(id+"F0.wireOp",EDGE,"E4.14.1"),sQuery(id+"F0.wireOp",EDGE,"E4.15.0"),sQuery(id+"F0.wireOp",EDGE,"E4.15.1"),sQuery(id+"F0.wireOp",EDGE,"E4.16.0"),sQuery(id+"F0.wireOp",EDGE,"E4.16.1"),sQuery(id+"F0.wireOp",EDGE,"E4.17.0"),sQuery(id+"F0.wireOp",EDGE,"E4.17.1"),sQuery(id+"F0.wireOp",EDGE,"E4.18.0"),sQuery(id+"F0.wireOp",EDGE,"E4.18.1"),sQuery(id+"F0.wireOp",EDGE,"E4.19.0"),sQuery(id+"F0.wireOp",EDGE,"E4.19.1"),sQuery(id+"F0.wireOp",EDGE,"E4.20.0"),sQuery(id+"F0.wireOp",EDGE,"E4.20.1"),sQuery(id+"F0.wireOp",EDGE,"E4.21.0"),sQuery(id+"F0.wireOp",EDGE,"E4.21.1"),sQuery(id+"F0.wireOp",EDGE,"E4.22.0"),sQuery(id+"F0.wireOp",EDGE,"E4.22.1"),sQuery(id+"F0.wireOp",EDGE,"E4.23.0"),sQuery(id+"F0.wireOp",EDGE,"E4.23.1"),sQuery(id+"F0.wireOp",EDGE,"E4.24.0"),sQuery(id+"F0.wireOp",EDGE,"E4.24.1"),sQuery(id+"F0.wireOp",EDGE,"E4.25.0"),sQuery(id+"F0.wireOp",EDGE,"E4.25.1"),sQuery(id+"F0.wireOp",EDGE,"E4.26.0"),sQuery(id+"F0.wireOp",EDGE,"E4.26.1"),sQuery(id+"F0.wireOp",EDGE,"E4.27.0"),sQuery(id+"F0.wireOp",EDGE,"E4.27.1"),sQuery(id+"F0.wireOp",EDGE,"E4.28.0"),sQuery(id+"F0.wireOp",EDGE,"E4.28.1"),sQuery(id+"F0.wireOp",EDGE,"E4.29.0"),sQuery(id+"F0.wireOp",EDGE,"E4.29.1")])],"isStart":true}),makeQuery(id+"F5.opExtrude","SWEPT_FACE",FACE,{"disambiguationData":[OSD([sQuery(id+"F4.wireOp",EDGE,"E40.top")])]})]});
            var Q11;
            Q11=makeQuery(id+"F5.boolean.opBoolean","INTERSECT",EDGE,{"derivedFrom":[makeQuery(id+"F1.opExtrude","CAP_FACE",FACE,{"disambiguationData":[OSD([sQuery(id+"F0.wireOp",EDGE,"E0"),sQuery(id+"F0.wireOp",EDGE,"E2"),sQuery(id+"F0.wireOp",EDGE,"E3"),sQuery(id+"F0.wireOp",EDGE,"E4.1.0"),sQuery(id+"F0.wireOp",EDGE,"E4.1.1"),sQuery(id+"F0.wireOp",EDGE,"E4.2.0"),sQuery(id+"F0.wireOp",EDGE,"E4.2.1"),sQuery(id+"F0.wireOp",EDGE,"E4.3.0"),sQuery(id+"F0.wireOp",EDGE,"E4.3.1"),sQuery(id+"F0.wireOp",EDGE,"E4.4.0"),sQuery(id+"F0.wireOp",EDGE,"E4.4.1"),sQuery(id+"F0.wireOp",EDGE,"E4.5.0"),sQuery(id+"F0.wireOp",EDGE,"E4.5.1"),sQuery(id+"F0.wireOp",EDGE,"E4.6.0"),sQuery(id+"F0.wireOp",EDGE,"E4.6.1"),sQuery(id+"F0.wireOp",EDGE,"E4.7.0"),sQuery(id+"F0.wireOp",EDGE,"E4.7.1"),sQuery(id+"F0.wireOp",EDGE,"E4.8.0"),sQuery(id+"F0.wireOp",EDGE,"E4.8.1"),sQuery(id+"F0.wireOp",EDGE,"E4.9.0"),sQuery(id+"F0.wireOp",EDGE,"E4.9.1"),sQuery(id+"F0.wireOp",EDGE,"E4.10.0"),sQuery(id+"F0.wireOp",EDGE,"E4.10.1"),sQuery(id+"F0.wireOp",EDGE,"E4.11.0"),sQuery(id+"F0.wireOp",EDGE,"E4.11.1"),sQuery(id+"F0.wireOp",EDGE,"E4.12.0"),sQuery(id+"F0.wireOp",EDGE,"E4.12.1"),sQuery(id+"F0.wireOp",EDGE,"E4.13.0"),sQuery(id+"F0.wireOp",EDGE,"E4.13.1"),sQuery(id+"F0.wireOp",EDGE,"E4.14.0"),sQuery(id+"F0.wireOp",EDGE,"E4.14.1"),sQuery(id+"F0.wireOp",EDGE,"E4.15.0"),sQuery(id+"F0.wireOp",EDGE,"E4.15.1"),sQuery(id+"F0.wireOp",EDGE,"E4.16.0"),sQuery(id+"F0.wireOp",EDGE,"E4.16.1"),sQuery(id+"F0.wireOp",EDGE,"E4.17.0"),sQuery(id+"F0.wireOp",EDGE,"E4.17.1"),sQuery(id+"F0.wireOp",EDGE,"E4.18.0"),sQuery(id+"F0.wireOp",EDGE,"E4.18.1"),sQuery(id+"F0.wireOp",EDGE,"E4.19.0"),sQuery(id+"F0.wireOp",EDGE,"E4.19.1"),sQuery(id+"F0.wireOp",EDGE,"E4.20.0"),sQuery(id+"F0.wireOp",EDGE,"E4.20.1"),sQuery(id+"F0.wireOp",EDGE,"E4.21.0"),sQuery(id+"F0.wireOp",EDGE,"E4.21.1"),sQuery(id+"F0.wireOp",EDGE,"E4.22.0"),sQuery(id+"F0.wireOp",EDGE,"E4.22.1"),sQuery(id+"F0.wireOp",EDGE,"E4.23.0"),sQuery(id+"F0.wireOp",EDGE,"E4.23.1"),sQuery(id+"F0.wireOp",EDGE,"E4.24.0"),sQuery(id+"F0.wireOp",EDGE,"E4.24.1"),sQuery(id+"F0.wireOp",EDGE,"E4.25.0"),sQuery(id+"F0.wireOp",EDGE,"E4.25.1"),sQuery(id+"F0.wireOp",EDGE,"E4.26.0"),sQuery(id+"F0.wireOp",EDGE,"E4.26.1"),sQuery(id+"F0.wireOp",EDGE,"E4.27.0"),sQuery(id+"F0.wireOp",EDGE,"E4.27.1"),sQuery(id+"F0.wireOp",EDGE,"E4.28.0"),sQuery(id+"F0.wireOp",EDGE,"E4.28.1"),sQuery(id+"F0.wireOp",EDGE,"E4.29.0"),sQuery(id+"F0.wireOp",EDGE,"E4.29.1")])],"isStart":true}),makeQuery(id+"F5.opExtrude","SWEPT_FACE",FACE,{"disambiguationData":[OSD([sQuery(id+"F4.wireOp",EDGE,"E40.right")])]})]});
            var Q12;
            Q12=makeQuery(id+"F5.boolean.opBoolean","INTERSECT",EDGE,{"derivedFrom":[makeQuery(id+"F1.opExtrude","CAP_FACE",FACE,{"disambiguationData":[OSD([sQuery(id+"F0.wireOp",EDGE,"E0"),sQuery(id+"F0.wireOp",EDGE,"E2"),sQuery(id+"F0.wireOp",EDGE,"E3"),sQuery(id+"F0.wireOp",EDGE,"E4.1.0"),sQuery(id+"F0.wireOp",EDGE,"E4.1.1"),sQuery(id+"F0.wireOp",EDGE,"E4.2.0"),sQuery(id+"F0.wireOp",EDGE,"E4.2.1"),sQuery(id+"F0.wireOp",EDGE,"E4.3.0"),sQuery(id+"F0.wireOp",EDGE,"E4.3.1"),sQuery(id+"F0.wireOp",EDGE,"E4.4.0"),sQuery(id+"F0.wireOp",EDGE,"E4.4.1"),sQuery(id+"F0.wireOp",EDGE,"E4.5.0"),sQuery(id+"F0.wireOp",EDGE,"E4.5.1"),sQuery(id+"F0.wireOp",EDGE,"E4.6.0"),sQuery(id+"F0.wireOp",EDGE,"E4.6.1"),sQuery(id+"F0.wireOp",EDGE,"E4.7.0"),sQuery(id+"F0.wireOp",EDGE,"E4.7.1"),sQuery(id+"F0.wireOp",EDGE,"E4.8.0"),sQuery(id+"F0.wireOp",EDGE,"E4.8.1"),sQuery(id+"F0.wireOp",EDGE,"E4.9.0"),sQuery(id+"F0.wireOp",EDGE,"E4.9.1"),sQuery(id+"F0.wireOp",EDGE,"E4.10.0"),sQuery(id+"F0.wireOp",EDGE,"E4.10.1"),sQuery(id+"F0.wireOp",EDGE,"E4.11.0"),sQuery(id+"F0.wireOp",EDGE,"E4.11.1"),sQuery(id+"F0.wireOp",EDGE,"E4.12.0"),sQuery(id+"F0.wireOp",EDGE,"E4.12.1"),sQuery(id+"F0.wireOp",EDGE,"E4.13.0"),sQuery(id+"F0.wireOp",EDGE,"E4.13.1"),sQuery(id+"F0.wireOp",EDGE,"E4.14.0"),sQuery(id+"F0.wireOp",EDGE,"E4.14.1"),sQuery(id+"F0.wireOp",EDGE,"E4.15.0"),sQuery(id+"F0.wireOp",EDGE,"E4.15.1"),sQuery(id+"F0.wireOp",EDGE,"E4.16.0"),sQuery(id+"F0.wireOp",EDGE,"E4.16.1"),sQuery(id+"F0.wireOp",EDGE,"E4.17.0"),sQuery(id+"F0.wireOp",EDGE,"E4.17.1"),sQuery(id+"F0.wireOp",EDGE,"E4.18.0"),sQuery(id+"F0.wireOp",EDGE,"E4.18.1"),sQuery(id+"F0.wireOp",EDGE,"E4.19.0"),sQuery(id+"F0.wireOp",EDGE,"E4.19.1"),sQuery(id+"F0.wireOp",EDGE,"E4.20.0"),sQuery(id+"F0.wireOp",EDGE,"E4.20.1"),sQuery(id+"F0.wireOp",EDGE,"E4.21.0"),sQuery(id+"F0.wireOp",EDGE,"E4.21.1"),sQuery(id+"F0.wireOp",EDGE,"E4.22.0"),sQuery(id+"F0.wireOp",EDGE,"E4.22.1"),sQuery(id+"F0.wireOp",EDGE,"E4.23.0"),sQuery(id+"F0.wireOp",EDGE,"E4.23.1"),sQuery(id+"F0.wireOp",EDGE,"E4.24.0"),sQuery(id+"F0.wireOp",EDGE,"E4.24.1"),sQuery(id+"F0.wireOp",EDGE,"E4.25.0"),sQuery(id+"F0.wireOp",EDGE,"E4.25.1"),sQuery(id+"F0.wireOp",EDGE,"E4.26.0"),sQuery(id+"F0.wireOp",EDGE,"E4.26.1"),sQuery(id+"F0.wireOp",EDGE,"E4.27.0"),sQuery(id+"F0.wireOp",EDGE,"E4.27.1"),sQuery(id+"F0.wireOp",EDGE,"E4.28.0"),sQuery(id+"F0.wireOp",EDGE,"E4.28.1"),sQuery(id+"F0.wireOp",EDGE,"E4.29.0"),sQuery(id+"F0.wireOp",EDGE,"E4.29.1")])],"isStart":true}),makeQuery(id+"F5.opExtrude","SWEPT_FACE",FACE,{"disambiguationData":[OSD([sQuery(id+"F4.wireOp",EDGE,"E39.top")])]})]});
            var Q13;
            Q13=makeQuery(id+"F5.boolean.opBoolean","INTERSECT",EDGE,{"derivedFrom":[makeQuery(id+"F1.opExtrude","CAP_FACE",FACE,{"disambiguationData":[OSD([sQuery(id+"F0.wireOp",EDGE,"E0"),sQuery(id+"F0.wireOp",EDGE,"E2"),sQuery(id+"F0.wireOp",EDGE,"E3"),sQuery(id+"F0.wireOp",EDGE,"E4.1.0"),sQuery(id+"F0.wireOp",EDGE,"E4.1.1"),sQuery(id+"F0.wireOp",EDGE,"E4.2.0"),sQuery(id+"F0.wireOp",EDGE,"E4.2.1"),sQuery(id+"F0.wireOp",EDGE,"E4.3.0"),sQuery(id+"F0.wireOp",EDGE,"E4.3.1"),sQuery(id+"F0.wireOp",EDGE,"E4.4.0"),sQuery(id+"F0.wireOp",EDGE,"E4.4.1"),sQuery(id+"F0.wireOp",EDGE,"E4.5.0"),sQuery(id+"F0.wireOp",EDGE,"E4.5.1"),sQuery(id+"F0.wireOp",EDGE,"E4.6.0"),sQuery(id+"F0.wireOp",EDGE,"E4.6.1"),sQuery(id+"F0.wireOp",EDGE,"E4.7.0"),sQuery(id+"F0.wireOp",EDGE,"E4.7.1"),sQuery(id+"F0.wireOp",EDGE,"E4.8.0"),sQuery(id+"F0.wireOp",EDGE,"E4.8.1"),sQuery(id+"F0.wireOp",EDGE,"E4.9.0"),sQuery(id+"F0.wireOp",EDGE,"E4.9.1"),sQuery(id+"F0.wireOp",EDGE,"E4.10.0"),sQuery(id+"F0.wireOp",EDGE,"E4.10.1"),sQuery(id+"F0.wireOp",EDGE,"E4.11.0"),sQuery(id+"F0.wireOp",EDGE,"E4.11.1"),sQuery(id+"F0.wireOp",EDGE,"E4.12.0"),sQuery(id+"F0.wireOp",EDGE,"E4.12.1"),sQuery(id+"F0.wireOp",EDGE,"E4.13.0"),sQuery(id+"F0.wireOp",EDGE,"E4.13.1"),sQuery(id+"F0.wireOp",EDGE,"E4.14.0"),sQuery(id+"F0.wireOp",EDGE,"E4.14.1"),sQuery(id+"F0.wireOp",EDGE,"E4.15.0"),sQuery(id+"F0.wireOp",EDGE,"E4.15.1"),sQuery(id+"F0.wireOp",EDGE,"E4.16.0"),sQuery(id+"F0.wireOp",EDGE,"E4.16.1"),sQuery(id+"F0.wireOp",EDGE,"E4.17.0"),sQuery(id+"F0.wireOp",EDGE,"E4.17.1"),sQuery(id+"F0.wireOp",EDGE,"E4.18.0"),sQuery(id+"F0.wireOp",EDGE,"E4.18.1"),sQuery(id+"F0.wireOp",EDGE,"E4.19.0"),sQuery(id+"F0.wireOp",EDGE,"E4.19.1"),sQuery(id+"F0.wireOp",EDGE,"E4.20.0"),sQuery(id+"F0.wireOp",EDGE,"E4.20.1"),sQuery(id+"F0.wireOp",EDGE,"E4.21.0"),sQuery(id+"F0.wireOp",EDGE,"E4.21.1"),sQuery(id+"F0.wireOp",EDGE,"E4.22.0"),sQuery(id+"F0.wireOp",EDGE,"E4.22.1"),sQuery(id+"F0.wireOp",EDGE,"E4.23.0"),sQuery(id+"F0.wireOp",EDGE,"E4.23.1"),sQuery(id+"F0.wireOp",EDGE,"E4.24.0"),sQuery(id+"F0.wireOp",EDGE,"E4.24.1"),sQuery(id+"F0.wireOp",EDGE,"E4.25.0"),sQuery(id+"F0.wireOp",EDGE,"E4.25.1"),sQuery(id+"F0.wireOp",EDGE,"E4.26.0"),sQuery(id+"F0.wireOp",EDGE,"E4.26.1"),sQuery(id+"F0.wireOp",EDGE,"E4.27.0"),sQuery(id+"F0.wireOp",EDGE,"E4.27.1"),sQuery(id+"F0.wireOp",EDGE,"E4.28.0"),sQuery(id+"F0.wireOp",EDGE,"E4.28.1"),sQuery(id+"F0.wireOp",EDGE,"E4.29.0"),sQuery(id+"F0.wireOp",EDGE,"E4.29.1")])],"isStart":true}),makeQuery(id+"F5.opExtrude","SWEPT_FACE",FACE,{"disambiguationData":[OSD([sQuery(id+"F4.wireOp",EDGE,"E39.right")])]})]});
            var Q14;
            Q14=makeQuery(id+"F5.boolean.opBoolean","INTERSECT",EDGE,{"derivedFrom":[makeQuery(id+"F1.opExtrude","CAP_FACE",FACE,{"disambiguationData":[OSD([sQuery(id+"F0.wireOp",EDGE,"E0"),sQuery(id+"F0.wireOp",EDGE,"E2"),sQuery(id+"F0.wireOp",EDGE,"E3"),sQuery(id+"F0.wireOp",EDGE,"E4.1.0"),sQuery(id+"F0.wireOp",EDGE,"E4.1.1"),sQuery(id+"F0.wireOp",EDGE,"E4.2.0"),sQuery(id+"F0.wireOp",EDGE,"E4.2.1"),sQuery(id+"F0.wireOp",EDGE,"E4.3.0"),sQuery(id+"F0.wireOp",EDGE,"E4.3.1"),sQuery(id+"F0.wireOp",EDGE,"E4.4.0"),sQuery(id+"F0.wireOp",EDGE,"E4.4.1"),sQuery(id+"F0.wireOp",EDGE,"E4.5.0"),sQuery(id+"F0.wireOp",EDGE,"E4.5.1"),sQuery(id+"F0.wireOp",EDGE,"E4.6.0"),sQuery(id+"F0.wireOp",EDGE,"E4.6.1"),sQuery(id+"F0.wireOp",EDGE,"E4.7.0"),sQuery(id+"F0.wireOp",EDGE,"E4.7.1"),sQuery(id+"F0.wireOp",EDGE,"E4.8.0"),sQuery(id+"F0.wireOp",EDGE,"E4.8.1"),sQuery(id+"F0.wireOp",EDGE,"E4.9.0"),sQuery(id+"F0.wireOp",EDGE,"E4.9.1"),sQuery(id+"F0.wireOp",EDGE,"E4.10.0"),sQuery(id+"F0.wireOp",EDGE,"E4.10.1"),sQuery(id+"F0.wireOp",EDGE,"E4.11.0"),sQuery(id+"F0.wireOp",EDGE,"E4.11.1"),sQuery(id+"F0.wireOp",EDGE,"E4.12.0"),sQuery(id+"F0.wireOp",EDGE,"E4.12.1"),sQuery(id+"F0.wireOp",EDGE,"E4.13.0"),sQuery(id+"F0.wireOp",EDGE,"E4.13.1"),sQuery(id+"F0.wireOp",EDGE,"E4.14.0"),sQuery(id+"F0.wireOp",EDGE,"E4.14.1"),sQuery(id+"F0.wireOp",EDGE,"E4.15.0"),sQuery(id+"F0.wireOp",EDGE,"E4.15.1"),sQuery(id+"F0.wireOp",EDGE,"E4.16.0"),sQuery(id+"F0.wireOp",EDGE,"E4.16.1"),sQuery(id+"F0.wireOp",EDGE,"E4.17.0"),sQuery(id+"F0.wireOp",EDGE,"E4.17.1"),sQuery(id+"F0.wireOp",EDGE,"E4.18.0"),sQuery(id+"F0.wireOp",EDGE,"E4.18.1"),sQuery(id+"F0.wireOp",EDGE,"E4.19.0"),sQuery(id+"F0.wireOp",EDGE,"E4.19.1"),sQuery(id+"F0.wireOp",EDGE,"E4.20.0"),sQuery(id+"F0.wireOp",EDGE,"E4.20.1"),sQuery(id+"F0.wireOp",EDGE,"E4.21.0"),sQuery(id+"F0.wireOp",EDGE,"E4.21.1"),sQuery(id+"F0.wireOp",EDGE,"E4.22.0"),sQuery(id+"F0.wireOp",EDGE,"E4.22.1"),sQuery(id+"F0.wireOp",EDGE,"E4.23.0"),sQuery(id+"F0.wireOp",EDGE,"E4.23.1"),sQuery(id+"F0.wireOp",EDGE,"E4.24.0"),sQuery(id+"F0.wireOp",EDGE,"E4.24.1"),sQuery(id+"F0.wireOp",EDGE,"E4.25.0"),sQuery(id+"F0.wireOp",EDGE,"E4.25.1"),sQuery(id+"F0.wireOp",EDGE,"E4.26.0"),sQuery(id+"F0.wireOp",EDGE,"E4.26.1"),sQuery(id+"F0.wireOp",EDGE,"E4.27.0"),sQuery(id+"F0.wireOp",EDGE,"E4.27.1"),sQuery(id+"F0.wireOp",EDGE,"E4.28.0"),sQuery(id+"F0.wireOp",EDGE,"E4.28.1"),sQuery(id+"F0.wireOp",EDGE,"E4.29.0"),sQuery(id+"F0.wireOp",EDGE,"E4.29.1")])],"isStart":true}),makeQuery(id+"F5.opExtrude","SWEPT_FACE",FACE,{"disambiguationData":[OSD([sQuery(id+"F4.wireOp",EDGE,"E39.bottom")])]})]});
            var Q15;
            Q15=makeQuery(id+"F5.boolean.opBoolean","INTERSECT",EDGE,{"derivedFrom":[makeQuery(id+"F1.opExtrude","CAP_FACE",FACE,{"disambiguationData":[OSD([sQuery(id+"F0.wireOp",EDGE,"E0"),sQuery(id+"F0.wireOp",EDGE,"E2"),sQuery(id+"F0.wireOp",EDGE,"E3"),sQuery(id+"F0.wireOp",EDGE,"E4.1.0"),sQuery(id+"F0.wireOp",EDGE,"E4.1.1"),sQuery(id+"F0.wireOp",EDGE,"E4.2.0"),sQuery(id+"F0.wireOp",EDGE,"E4.2.1"),sQuery(id+"F0.wireOp",EDGE,"E4.3.0"),sQuery(id+"F0.wireOp",EDGE,"E4.3.1"),sQuery(id+"F0.wireOp",EDGE,"E4.4.0"),sQuery(id+"F0.wireOp",EDGE,"E4.4.1"),sQuery(id+"F0.wireOp",EDGE,"E4.5.0"),sQuery(id+"F0.wireOp",EDGE,"E4.5.1"),sQuery(id+"F0.wireOp",EDGE,"E4.6.0"),sQuery(id+"F0.wireOp",EDGE,"E4.6.1"),sQuery(id+"F0.wireOp",EDGE,"E4.7.0"),sQuery(id+"F0.wireOp",EDGE,"E4.7.1"),sQuery(id+"F0.wireOp",EDGE,"E4.8.0"),sQuery(id+"F0.wireOp",EDGE,"E4.8.1"),sQuery(id+"F0.wireOp",EDGE,"E4.9.0"),sQuery(id+"F0.wireOp",EDGE,"E4.9.1"),sQuery(id+"F0.wireOp",EDGE,"E4.10.0"),sQuery(id+"F0.wireOp",EDGE,"E4.10.1"),sQuery(id+"F0.wireOp",EDGE,"E4.11.0"),sQuery(id+"F0.wireOp",EDGE,"E4.11.1"),sQuery(id+"F0.wireOp",EDGE,"E4.12.0"),sQuery(id+"F0.wireOp",EDGE,"E4.12.1"),sQuery(id+"F0.wireOp",EDGE,"E4.13.0"),sQuery(id+"F0.wireOp",EDGE,"E4.13.1"),sQuery(id+"F0.wireOp",EDGE,"E4.14.0"),sQuery(id+"F0.wireOp",EDGE,"E4.14.1"),sQuery(id+"F0.wireOp",EDGE,"E4.15.0"),sQuery(id+"F0.wireOp",EDGE,"E4.15.1"),sQuery(id+"F0.wireOp",EDGE,"E4.16.0"),sQuery(id+"F0.wireOp",EDGE,"E4.16.1"),sQuery(id+"F0.wireOp",EDGE,"E4.17.0"),sQuery(id+"F0.wireOp",EDGE,"E4.17.1"),sQuery(id+"F0.wireOp",EDGE,"E4.18.0"),sQuery(id+"F0.wireOp",EDGE,"E4.18.1"),sQuery(id+"F0.wireOp",EDGE,"E4.19.0"),sQuery(id+"F0.wireOp",EDGE,"E4.19.1"),sQuery(id+"F0.wireOp",EDGE,"E4.20.0"),sQuery(id+"F0.wireOp",EDGE,"E4.20.1"),sQuery(id+"F0.wireOp",EDGE,"E4.21.0"),sQuery(id+"F0.wireOp",EDGE,"E4.21.1"),sQuery(id+"F0.wireOp",EDGE,"E4.22.0"),sQuery(id+"F0.wireOp",EDGE,"E4.22.1"),sQuery(id+"F0.wireOp",EDGE,"E4.23.0"),sQuery(id+"F0.wireOp",EDGE,"E4.23.1"),sQuery(id+"F0.wireOp",EDGE,"E4.24.0"),sQuery(id+"F0.wireOp",EDGE,"E4.24.1"),sQuery(id+"F0.wireOp",EDGE,"E4.25.0"),sQuery(id+"F0.wireOp",EDGE,"E4.25.1"),sQuery(id+"F0.wireOp",EDGE,"E4.26.0"),sQuery(id+"F0.wireOp",EDGE,"E4.26.1"),sQuery(id+"F0.wireOp",EDGE,"E4.27.0"),sQuery(id+"F0.wireOp",EDGE,"E4.27.1"),sQuery(id+"F0.wireOp",EDGE,"E4.28.0"),sQuery(id+"F0.wireOp",EDGE,"E4.28.1"),sQuery(id+"F0.wireOp",EDGE,"E4.29.0"),sQuery(id+"F0.wireOp",EDGE,"E4.29.1")])],"isStart":true}),makeQuery(id+"F5.opExtrude","SWEPT_FACE",FACE,{"disambiguationData":[OSD([sQuery(id+"F4.wireOp",EDGE,"E39.left")])]})]});
            chamfer(context, id + "F9", {"entities" : qUnion([Q0, Q1, Q2, Q3, Q4, Q5, Q6, Q7, Q8, Q9, Q10, Q11, Q12, Q13, Q14, Q15]), "width" : 1 * mm, "tangentPropagation" : true});
        }
    });
